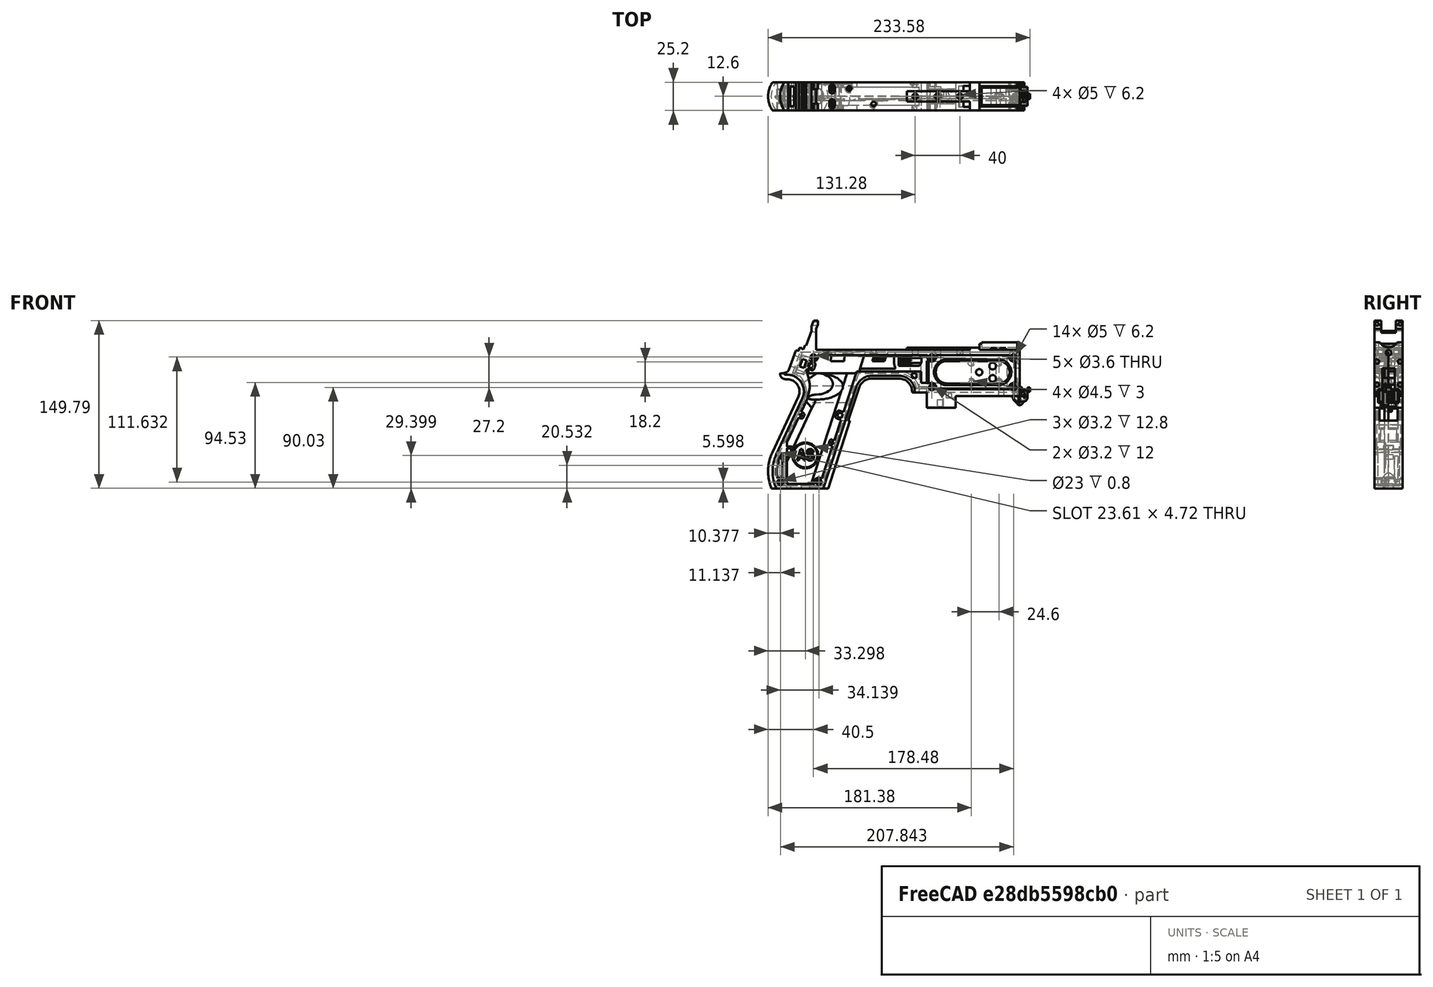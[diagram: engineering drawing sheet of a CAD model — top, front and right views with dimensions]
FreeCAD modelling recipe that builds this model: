
FCSTD DOCUMENT  (FreeCAD 1.0R39319 (Git))
Label: PICON-OF_ver_37
License: All rights reserved
LicenseURL: https://en.wikipedia.org/wiki/All_rights_reserved
objects: Sketcher::SketchObject×107, Part::Extrusion×50, Part::Cut×39, PartDesign::Pad×29, PartDesign::Pocket×18, PartDesign::Chamfer×15, PartDesign::Body×10, PartDesign::Fillet×6, PartDesign::SubtractivePipe×4, Part::Part2DObjectPython×4, PartDesign::SubtractiveLoft×4, PartDesign::Plane×2, PartDesign::SubShapeBinder×2, Part::Sweep×1, PartDesign::ShapeBinder×1, Part::MultiFuse×1, Mesh::Feature×1
note: 552 computed .brp shape members not serialized (recipe doc carries the construction recipe); baked Part::Feature solids carry a one-line shape summary decoded from their .brp

FEATURE [Sketcher::SketchObject] Sketch  label="corpo principale"
  ArcFitTolerance = 1e-06
  AttacherType = Attacher::AttachEngine3D
  AttachmentSupport = -> [XZ_Plane]
  FullyConstrained = true
  MakeInternals = false
  MapMode = 5
  Placement = pos=(0,0,0) rot=(1,0,0;1.5708rad)
  sketch-geometry (65):
    g0: LineSegment StartX=0 StartY=0 StartZ=0 EndX=-57.2 EndY=0 EndZ=0
    g1: LineSegment StartX=-57.2 StartY=0 StartZ=0 EndX=-57.2 EndY=-10.4 EndZ=0
    g2: LineSegment StartX=-57.2 StartY=-10.4 StartZ=0 EndX=-82.8 EndY=-10.4 EndZ=0
    g3: LineSegment StartX=-82.8 StartY=-10.4 StartZ=0 EndX=-82.8 EndY=3.2 EndZ=0
    g4: LineSegment StartX=-82.8 StartY=3.2 StartZ=0 EndX=-93.6 EndY=3.2 EndZ=0
    g5: LineSegment StartX=-93.6 StartY=3.2 StartZ=0 EndX=-93.6 EndY=4 EndZ=0
    g6: LineSegment StartX=-107.6 StartY=18 StartZ=0 EndX=-132.428 EndY=18 EndZ=0
    g7: LineSegment StartX=-145.743 StartY=8.32624 StartZ=0 EndX=-175.232 EndY=-82.4316 EndZ=0
    g8: LineSegment StartX=-175.232 StartY=-82.4316 StartZ=0 EndX=-217.232 EndY=-82.4316 EndZ=0
    g9: LineSegment StartX=-217.232 StartY=-52.1862 StartZ=0 EndX=-193.988 EndY=-2.33927 EndZ=0
    g10: LineSegment StartX=-206.196 StartY=23.0857 StartZ=0 EndX=-199.861 EndY=40.4914 EndZ=0
    g11: LineSegment StartX=-199.861 StartY=40.4914 StartZ=0 EndX=-197.061 EndY=40.4914 EndZ=0
    g12: LineSegment StartX=-197.061 StartY=40.4914 StartZ=0 EndX=-197.061 EndY=42.8914 EndZ=0
    g13: LineSegment StartX=-197.061 StartY=42.8914 StartZ=0 EndX=-194.261 EndY=42.8914 EndZ=0
    g14: LineSegment StartX=-194.261 StartY=42.8914 StartZ=0 EndX=-194.535 EndY=42.1397 EndZ=0
    g15: LineSegment StartX=-194.535 StartY=42.1397 StartZ=0 EndX=-193.031 EndY=41.5924 EndZ=0
    g16: LineSegment StartX=-193.031 StartY=41.5924 StartZ=0 EndX=-191.663 EndY=45.3512 EndZ=0
    g17: LineSegment StartX=-191.663 StartY=45.3512 StartZ=0 EndX=-190.536 EndY=44.9408 EndZ=0
    g18: LineSegment StartX=-190.536 StartY=44.9408 StartZ=0 EndX=-185.747 EndY=58.0965 EndZ=0
    g19: LineSegment StartX=-185.747 StartY=58.0965 StartZ=0 EndX=-185.747 EndY=62.0965 EndZ=0
    g20: LineSegment StartX=-185.747 StartY=62.0965 StartZ=0 EndX=-183.832 EndY=67.3588 EndZ=0
    g21: LineSegment StartX=-183.832 StartY=67.3588 StartZ=0 EndX=-180.232 EndY=67.3588 EndZ=0
    g22: LineSegment StartX=-180.232 StartY=67.3588 StartZ=0 EndX=-180.232 EndY=63.7588 EndZ=0
    g23: LineSegment StartX=-180.232 StartY=63.7588 StartZ=0 EndX=-181.6 EndY=60 EndZ=0
    g24: LineSegment StartX=-181.6 StartY=60 StartZ=0 EndX=-181.6 EndY=41.2 EndZ=0
    g25: LineSegment StartX=-181.6 StartY=41.2 StartZ=0 EndX=-100.8 EndY=41.2 EndZ=0
    g26: LineSegment StartX=-36 StartY=43.2 StartZ=0 EndX=-36 EndY=41.2 EndZ=0
    g27: LineSegment StartX=0 StartY=48 StartZ=0 EndX=0 EndY=0 EndZ=0
    g28: LineSegment StartX=-209.901 StartY=19.85 StartZ=0 EndX=-209.901 EndY=20.1 EndZ=0
    g29: LineSegment StartX=-208.001 StartY=22 StartZ=0 EndX=-207.747 EndY=22 EndZ=0
    g30: LineSegment StartX=-207.583 StartY=19 StartZ=0 EndX=-209.051 EndY=19 EndZ=0
    g31: ArcOfCircle CenterX=-208.001 CenterY=20.1 CenterZ=0 NormalX=0 NormalY=0 NormalZ=1 AngleXU=0 Radius=1.9 StartAngle=1.5708 EndAngle=3.14159
    g32: GeomPoint [constr] X=-209.901 Y=22 Z=0
    g33: ArcOfCircle CenterX=-209.051 CenterY=19.85 CenterZ=0 NormalX=0 NormalY=0 NormalZ=1 AngleXU=0 Radius=0.85 StartAngle=3.14159 EndAngle=4.71239
    g34: GeomPoint [constr] X=-209.901 Y=19 Z=0
    g35: ArcOfCircle CenterX=-207.747 CenterY=23.65 CenterZ=0 NormalX=0 NormalY=0 NormalZ=1 AngleXU=0 Radius=1.65 StartAngle=4.71239 EndAngle=5.93412
    g36: GeomPoint [constr] X=-206.591 Y=22 Z=0
    g37: LineSegment StartX=-4 StartY=6 StartZ=0 EndX=-4 EndY=36.4 EndZ=0
    g38: LineSegment StartX=-4 StartY=36.4 StartZ=0 EndX=-185.2 EndY=36.4 EndZ=0
    g39: LineSegment StartX=-185.2 StartY=36.4 StartZ=0 EndX=-190.441 EndY=22 EndZ=0
    g40: LineSegment StartX=-214.575 StartY=-78.4316 StartZ=0 EndX=-178.142 EndY=-78.4316 EndZ=0
    g41: LineSegment StartX=-178.142 StartY=-78.4316 StartZ=0 EndX=-145.51 EndY=22 EndZ=0
    g42: LineSegment StartX=-145.51 StartY=22 StartZ=0 EndX=-87.91 EndY=22 EndZ=0
    g43: LineSegment StartX=-87.91 StartY=22 StartZ=0 EndX=-87.91 EndY=11.6 EndZ=0
    g44: LineSegment StartX=-87.91 StartY=11.6 StartZ=0 EndX=-80.11 EndY=11.6 EndZ=0
    g45: LineSegment StartX=-80.11 StartY=11.6 StartZ=0 EndX=-80.11 EndY=6 EndZ=0
    g46: LineSegment StartX=-80.11 StartY=6 StartZ=0 EndX=-4 EndY=6 EndZ=0
    g47: LineSegment StartX=-190.363 StartY=-4.02975 StartZ=0 EndX=-213.607 EndY=-53.8767 EndZ=0
    g48: ArcOfCircle CenterX=-132.428 CenterY=4 CenterZ=0 NormalX=0 NormalY=0 NormalZ=1 AngleXU=0 Radius=14 StartAngle=1.5708 EndAngle=2.82743
    g49: GeomPoint [constr] X=-142.6 Y=18 Z=0
    g50: ArcOfCircle CenterX=-107.6 CenterY=4 CenterZ=0 NormalX=0 NormalY=0 NormalZ=1 AngleXU=0 Radius=14 StartAngle=0 EndAngle=1.5708
    g51: GeomPoint [constr] X=-93.6 Y=18 Z=0
    g52: ArcOfCircle CenterX=-184.801 CenterY=-67.3089 CenterZ=0 NormalX=0 NormalY=0 NormalZ=1 AngleXU=0 Radius=35.7833 StartAngle=2.70526 EndAngle=3.57792
    g53: ArcOfCircle CenterX=-207.583 CenterY=4 CenterZ=0 NormalX=0 NormalY=0 NormalZ=1 AngleXU=0 Radius=15 StartAngle=5.84685 EndAngle=7.85398
    g54: LineSegment [constr] StartX=-213.607 StartY=-53.8767 StartZ=0 EndX=-217.232 EndY=-52.1862 EndZ=0
    g55: ArcOfCircle CenterX=-184.801 CenterY=-67.3089 CenterZ=0 NormalX=0 NormalY=0 NormalZ=1 AngleXU=0 Radius=31.7833 StartAngle=2.70526 EndAngle=3.49911
    g56: ArcOfCircle CenterX=-218.095 CenterY=8.90192 CenterZ=0 NormalX=0 NormalY=0 NormalZ=1 AngleXU=0 Radius=30.5989 StartAngle=5.84685 EndAngle=6.72553
    g57: LineSegment StartX=-44.6 StartY=43.2 StartZ=0 EndX=-36 EndY=43.2 EndZ=0
    g58: LineSegment StartX=-100.8 StartY=41.2 StartZ=0 EndX=-44.6 EndY=41.2 EndZ=0
    g59: LineSegment StartX=-44.6 StartY=41.2 StartZ=0 EndX=-44.6 EndY=43.2 EndZ=0
    g60: LineSegment StartX=-2.4 StartY=48 StartZ=0 EndX=0 EndY=48 EndZ=0
    g61: LineSegment StartX=-36 StartY=41.2 StartZ=0 EndX=-2.4 EndY=41.2 EndZ=0
    g62: LineSegment StartX=-2.4 StartY=41.2 StartZ=0 EndX=-2.4 EndY=48 EndZ=0
    g63: LineSegment [constr] StartX=-181.6 StartY=36.4 StartZ=0 EndX=-152.209 EndY=36.4 EndZ=0
    g64: LineSegment [constr] StartX=-181.6 StartY=36.4 StartZ=0 EndX=-130.41 EndY=36.4 EndZ=0
  constraints (183):
    c: Coincident(g-1,g0)
    c: PointOnObject(g0,g-1)
    c: Coincident(g0,g1)
    c: Vertical(g1)
    c: Coincident(g1,g2)
    c: Horizontal(g2)
    c: Coincident(g2,g3)
    c: Vertical(g3)
    c: Coincident(g3,g4)
    c: Coincident(g4,g5)
    c: Vertical(g5)
    c: Horizontal(g6)
    c: Coincident(g7,g8)
    c: Horizontal(g8)
    c: Coincident(g10,g11)
    c: Horizontal(g11)
    c: Coincident(g11,g12)
    c: Vertical(g12)
    c: Coincident(g12,g13)
    c: Horizontal(g13)
    c: Coincident(g13,g14)
    c: Coincident(g14,g15)
    c: Coincident(g15,g16)
    c: Coincident(g16,g17)
    c: Coincident(g17,g18)
    c: Coincident(g18,g19)
    c: Vertical(g19)
    c: Coincident(g19,g20)
    c: Coincident(g20,g21)
    c: Horizontal(g21)
    c: Coincident(g21,g22)
    c: Vertical(g22)
    c: Coincident(g22,g23)
    c: Coincident(g23,g24)
    c: Vertical(g24)
    c: Coincident(g24,g25)
    c: Horizontal(g25)
    c: Coincident(g57,g26)
    c: Vertical(g26)
    c: Coincident(g26,g61)
    c: PointOnObject(g60,g-2)
    c: Coincident(g60,g27)
    c: Coincident(g27,g0)
    c: DistanceY(g27,g27) = 48
    c: DistanceY(g1,g1) = 10.4
    c: DistanceX(g0,g0) = 57.2
    c: DistanceX(g2,g2) = 25.6
    c: Horizontal(g4)
    c: DistanceY(g3,g3) = 13.6
    c: DistanceX(g4,g4) = 10.8
    c: DistanceY(g5,g51) = 14.8
    c: DistanceX(g49,g51) = 49
    c: Distance(g7,g49) = 105.6
    c: DistanceX(g61,g60) = 36
    c: DistanceX(g25,g25) = 80.8
    c: DistanceY(g24,g24) = 18.8
    c: DistanceY(g22,g22) = 3.6
    c: Distance(g23) = 4
    c: Angle(g-1,g23) = 1.22173
    c: DistanceX(g21,g21) = 3.6
    c: Distance(g20) = 5.6
    c: Angle(g-1,g20) = 1.22173
    c: DistanceY(g19,g19) = 4
    c: Distance(g18) = 14
    c: Angle(g-1,g18) = 1.22173
    c: Distance(g17) = 1.2
    c: Distance(g16) = 4
    c: Angle(g16) = 1.22173
    c: Perpendicular(g18,g17)
    c: Distance(g15) = 1.6
    c: Perpendicular(g16,g15)
    c: Distance(g14) = 0.8
    c: DistanceX(g13,g13) = 2.8
    c: Perpendicular(g15,g14)
    c: DistanceY(g12,g12) = 2.4
    c: DistanceX(g11,g11) = 2.8
    c: Distance(g9) = 55
    c: Angle(g9,g-1) = 2.00713
    c: Horizontal(g29)
    c: Vertical(g28)
    c: Horizontal(g30)
    c: PointOnObject(g32,g29)
    c: PointOnObject(g32,g28)
    c: Tangent(g29,g31) = 1.5708
    c: Tangent(g28,g31) = 1.5708
    c: PointOnObject(g34,g28)
    c: PointOnObject(g34,g30)
    c: Tangent(g28,g33) = 1.5708
    c: Tangent(g30,g33) = 1.5708
    c: PointOnObject(g36,g29)
    c: PointOnObject(g36,g10)
    c: Tangent(g29,g35) = -1.5708
    c: Tangent(g10,g35) = -1.5708
    c: Angle(g-1,g10) = 1.22173
    c: Radius(g35) = 1.65
    c: Vertical(g37)
    c: Coincident(g37,g38)
    c: Horizontal(g38)
    c: Coincident(g38,g39)
    c: Horizontal(g40)
    c: Coincident(g40,g41)
    c: Coincident(g41,g42)
    c: Horizontal(g42)
    c: Coincident(g42,g43)
    c: Vertical(g43)
    c: Coincident(g43,g44)
    c: Horizontal(g44)
    c: Coincident(g44,g45)
    c: Vertical(g45)
    c: Coincident(g45,g46)
    c: Coincident(g46,g37)
    c: Horizontal(g46)
    c: DistanceY(g0,g37) = 6
    c: DistanceX(g37,g0) = 4
    c: DistanceY(g37,g25) = 4.8
    c: DistanceX(g38,g38) = 181.2
    c: DistanceX(g42,g42) = 57.6
    c: DistanceY(g49,g41) = 4
    c: DistanceX(g41,g49) = 2.91
    c: DistanceY(g43,g43) = 10.4
    c: DistanceX(g44,g44) = 7.8
    c: DistanceY(g7,g40) = 4
    c: Distance(g47) = 55
    c: Angle(g-1,g39) = 1.22173
    c: PointOnObject(g49,g7)
    c: PointOnObject(g49,g6)
    c: Tangent(g7,g48) = -1.5708
    c: Tangent(g6,g48) = -1.5708
    c: PointOnObject(g51,g5)
    c: PointOnObject(g51,g6)
    c: Tangent(g5,g50) = -1.5708
    c: Tangent(g6,g50) = -1.5708
    c: Radius(g50) = 14
    c: Radius(g48) = 14
    c: DistanceX(g8,g8) = 42
    c: Angle(g7,g-1) = 1.88496
    c: Parallel(g41,g7)
    c: Parallel(g47,g9)
    c: Coincident(g52,g8)
    c: Tangent(g52,g9) = 1.5708
    c: DistanceX(g9,g8) = 0
    c: Tangent(g53,g9) = -1.5708
    c: Tangent(g53,g30) = -1.5708
    c: Diameter(g53) = 30
    c: DistanceY(g53,g0) = -4
    c: Coincident(g54,g47)
    c: Distance(g54) = 4
    c: Coincident(g54,g9)
    c: Coincident(g55,g40)
    c: Tangent(g55,g47) = -1.5708
    c: Coincident(g52,g55)
    c: Coincident(g56,g39)
    c: Tangent(g56,g47) = 1.5708
    c: Horizontal(g57)
    c: DistanceX(g57,g57) = 8.6
    c: Coincident(g58,g25)
    c: Horizontal(g58)
    c: Coincident(g59,g58)
    c: Vertical(g59)
    c: DistanceY(g58,g57) = 2
    c: DistanceX(g58,g58) = 56.2
    c: Coincident(g59,g57)
    c: DistanceY(g41,g36) = 0
    c: DistanceY(g36,g39) = 0
    c: DistanceY(g28,g28) = 0.25
    c: DistanceX(g30,g36) = 2.46
    c: DistanceX(g28,g29) = 1.9
    c: Coincident(g62,g60)
    c: Horizontal(g60)
    c: DistanceX(g62,g27) = 2.4
    c: Coincident(g61,g62)
    c: DistanceY(g26,g26) = 2
    c: Vertical(g62)
    c: DistanceY(g61,g60) = 6.8
    c: Horizontal(g61)
    c: Distance(g63) = 29.391
    c: PointOnObject(g63,g38)
    c: PointOnObject(g63,g38)
    c: Distance(g64) = 51.19
    c: PointOnObject(g64,g38)
    c: PointOnObject(g64,g38)
    c: DistanceX(g24,g63) = 0
    c: DistanceX(g24,g64) = 0
FEATURE [Part::Extrusion] Extrude  label="Extrude corpo principale"
  Base = -> Sketch
  Dir = (0,-1,2e-16)
  DirMode = 2
  FaceMakerClass = Part::FaceMakerBullseye
  FaceMakerMode = 3
  LengthFwd = 25.2
  LengthRev = 12.6
  Solid = true
  Symmetric = true
FEATURE [Sketcher::SketchObject] Sketch002  label="scavo grilletto"
  ArcFitTolerance = 1e-06
  AttachmentSupport = -> [XZ_Plane]
  ExternalGeometry = -> [Sketch]
  FullyConstrained = true
  MakeInternals = false
  MapMode = 5
  Placement = pos=(0,0,0) rot=(1,0,0;1.5708rad)
  sketch-geometry (4):
    g0: LineSegment StartX=-89.51 StartY=22 StartZ=0 EndX=-152.71 EndY=22 EndZ=0
    g1: LineSegment StartX=-152.71 StartY=22 StartZ=0 EndX=-167.006 EndY=-22 EndZ=0
    g2: LineSegment StartX=-167.006 StartY=-22 StartZ=0 EndX=-89.51 EndY=-22 EndZ=0
    g3: LineSegment StartX=-89.51 StartY=-22 StartZ=0 EndX=-89.51 EndY=22 EndZ=0
  constraints (12):
    c: Horizontal(g0)
    c: Coincident(g0,g1)
    c: Coincident(g1,g2)
    c: Horizontal(g2)
    c: Coincident(g2,g3)
    c: Coincident(g3,g0)
    c: Vertical(g3)
    c: Angle(g1,g0) = 1.88496
    c: DistanceY(g3,g3) = 44
    c: DistanceX(g0,g0) = 63.2
    c: DistanceX(g0,g-3) = 1.6
    c: DistanceY(g-3,g0) = 0
FEATURE [Sketcher::SketchObject] Sketch004  label="traiettoria arrotondamento impugnatura anteriore"
  ArcFitTolerance = 1e-06
  AttachmentSupport = -> [XZ_Plane]
  ExternalGeometry = -> [Sketch]
  FullyConstrained = true
  MakeInternals = false
  MapMode = 5
  Placement = pos=(0,0,0) rot=(1,0,0;1.5708rad)
  sketch-geometry (13):
    g0: LineSegment StartX=-175.232 StartY=-82.4316 StartZ=0 EndX=-145.743 EndY=8.32624 EndZ=0
    g1: LineSegment StartX=-93.6 StartY=3.2 StartZ=0 EndX=-93.6 EndY=4 EndZ=0
    g2: LineSegment StartX=-132.428 StartY=18 StartZ=0 EndX=-107.6 EndY=18 EndZ=0
    g3: ArcOfCircle CenterX=-132.428 CenterY=4 CenterZ=0 NormalX=0 NormalY=0 NormalZ=1 AngleXU=0 Radius=14 StartAngle=1.5708 EndAngle=2.82743
    g4: ArcOfCircle CenterX=-107.6 CenterY=4 CenterZ=0 NormalX=0 NormalY=0 NormalZ=1 AngleXU=0 Radius=14 StartAngle=0 EndAngle=1.5708
    g5: LineSegment StartX=-175.232 StartY=-82.4316 StartZ=0 EndX=-217.232 EndY=-82.4316 EndZ=0
    g6: LineSegment StartX=-217.232 StartY=-52.1862 StartZ=0 EndX=-193.988 EndY=-2.33927 EndZ=0
    g7: LineSegment StartX=-209.051 StartY=19 StartZ=0 EndX=-207.583 EndY=19 EndZ=0
    g8: LineSegment StartX=-209.901 StartY=20.1 StartZ=0 EndX=-209.901 EndY=19.85 EndZ=0
    g9: ArcOfCircle CenterX=-184.801 CenterY=-67.3089 CenterZ=0 NormalX=0 NormalY=0 NormalZ=1 AngleXU=0 Radius=35.7833 StartAngle=2.70526 EndAngle=3.57792
    g10: ArcOfCircle CenterX=-207.583 CenterY=4 CenterZ=0 NormalX=0 NormalY=0 NormalZ=1 AngleXU=0 Radius=15 StartAngle=5.84685 EndAngle=7.85398
    g11: ArcOfCircle CenterX=-209.051 CenterY=19.85 CenterZ=0 NormalX=0 NormalY=0 NormalZ=1 AngleXU=0 Radius=0.85 StartAngle=3.14159 EndAngle=4.71239
    g12: ArcOfCircle CenterX=-208.001 CenterY=20.1 CenterZ=0 NormalX=0 NormalY=0 NormalZ=1 AngleXU=0 Radius=1.9 StartAngle=1.5708 EndAngle=3.14159
  constraints (26):
    c: Coincident(g0,g-3)
    c: Coincident(g0,g-6)
    c: Coincident(g1,g-8)
    c: Coincident(g1,g-7)
    c: Coincident(g2,g-5)
    c: Coincident(g2,g-4)
    c: Coincident(g3,g2)
    c: Tangent(g3,g0) = 1.5708
    c: Coincident(g4,g1)
    c: Tangent(g4,g2) = 1.5708
    c: Coincident(g5,g0)
    c: Coincident(g5,g-9)
    c: Coincident(g6,g-12)
    c: Coincident(g6,g-11)
    c: Coincident(g7,g-15)
    c: Coincident(g7,g-14)
    c: Coincident(g8,g-16)
    c: Coincident(g8,g-17)
    c: Tangent(g9,g6) = 1.5708
    c: Coincident(g9,g5)
    c: Coincident(g10,g7)
    c: Tangent(g10,g6) = -1.5708
    c: Tangent(g11,g7) = -1.5708
    c: Coincident(g11,g8)
    c: Tangent(g12,g8) = -1.5708
    c: Coincident(g12,g-17)
FEATURE [PartDesign::Plane] DatumPlane  label="Piano per disegno arrotondamento impugnatura"
  AttachmentSupport = -> [Sketch]
  Length = 68.5841
  MapMode = 7
  Placement = pos=(-145.743,1.8e-15,8.32624) rot=(0.154555,0.154555,0.97582;1.59527rad)
  ResizeMode = 0
  Width = 191.269
FEATURE [Sketcher::SketchObject] Sketch005  label="forma arrotondamento impugnatura anteriore"
  ArcFitTolerance = 1e-06
  AttachmentSupport = -> [DatumPlane]
  FullyConstrained = true
  MakeInternals = false
  MapMode = 5
  Placement = pos=(-145.743,1.8e-15,8.32624) rot=(0.154555,0.154555,0.97582;1.59527rad)
  sketch-geometry (5):
    g0: GeomPoint [constr] X=0 Y=-4 Z=0
    g1: GeomPoint [constr] X=-12.6 Y=7.1e-15 Z=0
    g2: GeomPoint [constr] X=12.6 Y=4.97e-14 Z=0
    g3: LineSegment StartX=-12.6 StartY=7.1e-15 StartZ=0 EndX=12.6 EndY=4.97e-14 EndZ=0
    g4: ArcOfCircle CenterX=-3.88e-14 CenterY=17.845 CenterZ=0 NormalX=0 NormalY=0 NormalZ=1 AngleXU=0 Radius=21.845 StartAngle=4.09759 EndAngle=5.32718
  constraints (11):
    c: DistanceY(g0,g-1) = 4
    c: DistanceX(g-1,g0) = 0
    c: DistanceX(g1,g-1) = 12.6
    c: DistanceX(g-1,g2) = 12.6
    c: DistanceY(g-1,g2) = 0
    c: DistanceY(g-1,g1) = 0
    c: Coincident(g3,g1)
    c: Coincident(g3,g2)
    c: Coincident(g4,g1)
    c: Coincident(g4,g2)
    c: PointOnObject(g0,g4)
FEATURE [Part::Sweep] Sweep  label="Sweep impugnatura"
  Frenet = true
  Sections = -> [Sketch005]
  Solid = true
  Spine = -> Sketch [Edge32,Edge33,Edge34,Edge35,Edge36,Edge37,Edge38,Edge39,Edge40,Edge41,Edge42,Edge43,Edge44]
  Transition = 1
FEATURE [Sketcher::SketchObject] Sketch008  label="buchi e pulizie varie"
  ArcFitTolerance = 1e-06
  AttachmentSupport = -> [XZ_Plane]
  ExternalGeometry = -> [Sketch]
  FullyConstrained = true
  MakeInternals = false
  MapMode = 5
  Placement = pos=(0,0,0) rot=(1,0,0;1.5708rad)
  sketch-geometry (26):
    g0: LineSegment StartX=-96.278 StartY=20.155 StartZ=0 EndX=-92.278 EndY=20.155 EndZ=0
    g1: LineSegment StartX=-92.278 StartY=20.155 StartZ=0 EndX=-92.278 EndY=16.155 EndZ=0
    g2: LineSegment StartX=-92.278 StartY=16.155 StartZ=0 EndX=-96.278 EndY=16.155 EndZ=0
    g3: LineSegment StartX=-96.278 StartY=16.155 StartZ=0 EndX=-96.278 EndY=20.155 EndZ=0
    g4: LineSegment StartX=-222.232 StartY=-82.4316 StartZ=0 EndX=-170.232 EndY=-82.4316 EndZ=0
    g5: LineSegment StartX=-170.232 StartY=-82.4316 StartZ=0 EndX=-170.232 EndY=-86.4316 EndZ=0
    g6: LineSegment StartX=-170.232 StartY=-86.4316 StartZ=0 EndX=-222.232 EndY=-86.4316 EndZ=0
    g7: LineSegment StartX=-222.232 StartY=-86.4316 StartZ=0 EndX=-222.232 EndY=-82.4316 EndZ=0
    g8: LineSegment StartX=-213.901 StartY=20.1 StartZ=0 EndX=-213.901 EndY=26 EndZ=0
    g9: LineSegment StartX=-213.901 StartY=26 StartZ=0 EndX=-206.196 EndY=26 EndZ=0
    g10: LineSegment StartX=-17.4 StartY=42.8 StartZ=0 EndX=-12.4 EndY=42.8 EndZ=0
    g11: LineSegment StartX=-12.4 StartY=42.8 StartZ=0 EndX=-12.4 EndY=41.2 EndZ=0
    g12: LineSegment StartX=-12.4 StartY=41.2 StartZ=0 EndX=-17.4 EndY=41.2 EndZ=0
    g13: LineSegment StartX=-17.4 StartY=41.2 StartZ=0 EndX=-17.4 EndY=42.8 EndZ=0
    g14: LineSegment StartX=-25.9 StartY=42.8 StartZ=0 EndX=-20.9 EndY=42.8 EndZ=0
    g15: LineSegment StartX=-20.9 StartY=42.8 StartZ=0 EndX=-20.9 EndY=41.2 EndZ=0
    g16: LineSegment StartX=-20.9 StartY=41.2 StartZ=0 EndX=-25.9 EndY=41.2 EndZ=0
    g17: LineSegment StartX=-25.9 StartY=41.2 StartZ=0 EndX=-25.9 EndY=42.8 EndZ=0
    g18: GeomPoint [constr] X=-206.196 Y=23.0857 Z=0
    g19: GeomPoint [constr] X=-213.901 Y=20.1 Z=0
    g20: BSplineCurve PolesCount=4 KnotsCount=2 Degree=3 IsPeriodic=0
    g21-g24: Circle [constr] x4 (B-spline internal-alignment scaffolding for g20; pole/knot coordinates omitted)
    g25: LineSegment StartX=-206.196 StartY=26 StartZ=0 EndX=-206.196 EndY=23.0857 EndZ=0
  constraints (73):
    c: Horizontal(g0)
    c: Coincident(g1,g0)
    c: Vertical(g1)
    c: Coincident(g2,g1)
    c: Horizontal(g2)
    c: Coincident(g3,g2)
    c: Coincident(g3,g0)
    c: Vertical(g3)
    c: DistanceX(g0,g-4) = 4.368
    c: DistanceY(g0,g-4) = 1.845
    c: DistanceY(g1,g1) = 4
    c: DistanceX(g2,g2) = 4
    c: Horizontal(g4)
    c: Coincident(g5,g4)
    c: Vertical(g5)
    c: Coincident(g6,g5)
    c: Horizontal(g6)
    c: Coincident(g7,g6)
    c: Coincident(g7,g4)
    c: Vertical(g7)
    c: DistanceY(g7,g7) = 4
    c: DistanceX(g4,g-5) = 5
    c: DistanceX(g-5,g4) = 5
    c: DistanceY(g4,g-5) = 0
    c: Coincident(g9,g8)
    c: Parallel(g9,g-6)
    c: DistanceX(g8,g-8) = 4
    c: Horizontal(g10)
    c: Coincident(g11,g10)
    c: Vertical(g11)
    c: Coincident(g12,g11)
    c: Horizontal(g12)
    c: Coincident(g13,g12)
    c: Coincident(g13,g10)
    c: Vertical(g13)
    c: Horizontal(g14)
    c: Coincident(g15,g14)
    c: Vertical(g15)
    c: Coincident(g16,g15)
    c: Horizontal(g16)
    c: Coincident(g17,g16)
    c: Coincident(g17,g14)
    c: Vertical(g17)
    c: DistanceY(g11,g10) = 1.6
    c: DistanceX(g10,g10) = 5
    c: DistanceY(g15,g14) = 1.6
    c: DistanceX(g14,g14) = 5
    c: DistanceX(g15,g12) = 3.5
    c: DistanceX(g11,g-9) = 10
    c: DistanceY(g-9,g11) = 0
    c: DistanceY(g-9,g15) = 0
    c: Perpendicular(g8,g9)
    c: DistanceY(g-7,g9) = 4
    c: DistanceY(g8,g-8) = 0
    c: InternalAlignment(g18,g20)
    c: InternalAlignment(g19,g20)
    c: InternalAlignment(g21,g20)
    c: Weight(g21) = 1
    c: InternalAlignment(g22,g20)
    c: Equal(g22,g21)
    c: InternalAlignment(g23,g20)
    c: Equal(g23,g21)
    c: InternalAlignment(g24,g20)
    c: Equal(g24,g21)
    c: Coincident(g18,g-12)
    c: Coincident(g19,g8)
    c: Coincident(g25,g9)
    c: Coincident(g25,g20)
    c: Vertical(g25)
    c: DistanceY(g20,g23) = 0
    c: DistanceY(g22,g18) = 2.26
    c: DistanceX(g22,g18) = 0.93
    c: DistanceX(g20,g23) = 2.9
FEATURE [Part::Extrusion] Extrude004  label="Extrude Buchi e pulizie varie"
  Base = -> Sketch008
  Dir = (0,-1,2e-16)
  DirMode = 2
  FaceMakerClass = Part::FaceMakerBullseye
  FaceMakerMode = 3
  LengthFwd = 25.2
  LengthRev = 0
  Solid = true
  Symmetric = true
FEATURE [Sketcher::SketchObject] Sketch009  label="rinforzi"
  ArcFitTolerance = 1e-06
  AttachmentSupport = -> [XZ_Plane]
  ExternalGeometry = -> [Sketch]
  FullyConstrained = true
  MakeInternals = false
  MapMode = 5
  Placement = pos=(0,0,0) rot=(1,0,0;1.5708rad)
  sketch-geometry (9):
    g0: LineSegment StartX=-87.91 StartY=22 StartZ=0 EndX=-87.91 EndY=36.4 EndZ=0
    g1: LineSegment StartX=-87.91 StartY=36.4 StartZ=0 EndX=-97.91 EndY=36.4 EndZ=0
    g2: LineSegment StartX=-97.91 StartY=36.4 StartZ=0 EndX=-97.91 EndY=22 EndZ=0
    g3: LineSegment StartX=-97.91 StartY=22 StartZ=0 EndX=-87.91 EndY=22 EndZ=0
    g4: LineSegment StartX=-149.713 StartY=9.06563 StartZ=0 EndX=-154.586 EndY=-5.93437 EndZ=0
    g5: LineSegment StartX=-154.586 StartY=-5.93437 StartZ=0 EndX=-191.863 EndY=-5.93437 EndZ=0
    g6: LineSegment StartX=-191.863 StartY=-5.93437 StartZ=0 EndX=-191.863 EndY=9.06563 EndZ=0
    g7: LineSegment StartX=-191.863 StartY=9.06563 StartZ=0 EndX=-149.713 EndY=9.06563 EndZ=0
    g8: LineSegment [constr] StartX=-145.51 StartY=22 StartZ=0 EndX=-149.713 EndY=9.06563 EndZ=0
  constraints (25):
    c: Vertical(g0)
    c: Coincident(g1,g0)
    c: Horizontal(g1)
    c: Coincident(g2,g1)
    c: Vertical(g2)
    c: Coincident(g3,g2)
    c: Coincident(g3,g0)
    c: Horizontal(g3)
    c: Coincident(g0,g-4)
    c: DistanceX(g3,g3) = 10
    c: DistanceY(g0,g-3) = 0
    c: Coincident(g5,g4)
    c: Horizontal(g5)
    c: Coincident(g6,g5)
    c: Vertical(g6)
    c: Coincident(g7,g6)
    c: Coincident(g7,g4)
    c: Horizontal(g7)
    c: Distance(g8) = 13.6
    c: Parallel(g-6,g8)
    c: Coincident(g-6,g8)
    c: Parallel(g4,g-6)
    c: DistanceY(g4,g4) = 15
    c: Coincident(g4,g8)
    c: DistanceX(g-5,g5) = -1.5
FEATURE [Part::Extrusion] Extrude001  label="Extrude scavo grilletto"
  Base = -> Sketch002
  Dir = (0,-1,2e-16)
  DirMode = 2
  FaceMakerClass = Part::FaceMakerBullseye
  FaceMakerMode = 3
  LengthFwd = 16
  LengthRev = 0
  Solid = true
  Symmetric = true
FEATURE [Part::Extrusion] Extrude005  label="Extrude Rinforzi"
  Base = -> Sketch009
  Dir = (0,-1,2e-16)
  DirMode = 2
  FaceMakerClass = Part::FaceMakerBullseye
  FaceMakerMode = 3
  LengthFwd = 2
  LengthRev = 0
  Placement = pos=(0,12.6,0) rot=(0,0,1;0rad)
  Solid = true
  Symmetric = false
FEATURE [PartDesign::ShapeBinder] CopyCut
  TraceSupport = false
FEATURE [PartDesign::Plane] DatumPlane001
  AttachmentSupport = -> [CopyCut]
  Length = 60
  MapMode = 5
  Placement = pos=(0,12.6,0) rot=(0,0.707107,0.707107;3.14159rad)
  ResizeMode = 0
  Width = 60
FEATURE [Sketcher::SketchObject] Sketch010  label="buco neopixel"
  ArcFitTolerance = 1e-06
  AttachmentSupport = -> [XZ_Plane]
  ExternalGeometry = -> [Sketch]
  FullyConstrained = true
  MakeInternals = false
  MapMode = 5
  Placement = pos=(0,0,0) rot=(1,0,0;1.5708rad)
  sketch-geometry (5):
    g0: LineSegment [constr] StartX=-199.861 StartY=40.4914 StartZ=0 EndX=-201.368 EndY=36.3521 EndZ=0
    g1: LineSegment StartX=-201.368 StartY=36.3521 StartZ=0 EndX=-204.932 EndY=26.5605 EndZ=0
    g2: LineSegment StartX=-201.368 StartY=36.3521 StartZ=0 EndX=-180.2 EndY=28.6477 EndZ=0
    g3: LineSegment StartX=-180.2 StartY=28.6477 StartZ=0 EndX=-183.764 EndY=18.8561 EndZ=0
    g4: LineSegment StartX=-183.764 StartY=18.8561 StartZ=0 EndX=-204.932 EndY=26.5605 EndZ=0
  constraints (14):
    c: Parallel(g0,g-3)
    c: Distance(g0) = 4.405
    c: Coincident(g0,g-3)
    c: Coincident(g2,g1)
    c: Coincident(g3,g2)
    c: Coincident(g4,g3)
    c: Coincident(g4,g1)
    c: Parallel(g1,g-3)
    c: Distance(g1) = 10.42
    c: Coincident(g1,g0)
    c: Parallel(g2,g4)
    c: Perpendicular(g1,g2)
    c: DistanceX(g-4,g2) = 5
    c: Parallel(g3,g1)
FEATURE [Part::Extrusion] Extrude006  label="Extrude buco neopixel"
  Base = -> Sketch010
  Dir = (0,-1,2e-16)
  DirMode = 2
  FaceMakerClass = Part::FaceMakerBullseye
  FaceMakerMode = 3
  LengthFwd = 17.2
  LengthRev = 0
  Solid = true
  Symmetric = true
FEATURE [Sketcher::SketchObject] Sketch011  label="fermo grilletto"
  ArcFitTolerance = 1e-06
  AttachmentSupport = -> [XZ_Plane]
  ExternalGeometry = -> [Sketch]
  FullyConstrained = true
  MakeInternals = false
  MapMode = 5
  Placement = pos=(0,0,0) rot=(1,0,0;1.5708rad)
  sketch-geometry (18):
    g0: LineSegment [constr] StartX=-145.51 StartY=22 StartZ=0 EndX=-157.347 EndY=-14.4293 EndZ=0
    g1: LineSegment [constr] StartX=-157.347 StartY=-14.4293 StartZ=0 EndX=-157.841 EndY=-15.951 EndZ=0
    g2: LineSegment StartX=-161.151 StartY=-13.1932 StartZ=0 EndX=-155.825 EndY=-14.9237 EndZ=0
    g3: LineSegment StartX=-163.167 StartY=-14.2205 StartZ=0 EndX=-164.403 EndY=-18.0247 EndZ=0
    g4: LineSegment StartX=-163.376 StartY=-20.0408 StartZ=0 EndX=-158.05 EndY=-21.7713 EndZ=0
    g5: LineSegment StartX=-158.05 StartY=-21.7713 StartZ=0 EndX=-155.825 EndY=-14.9237 EndZ=0
    g6: LineSegment StartX=-161.645 StartY=-14.7149 StartZ=0 EndX=-157.841 EndY=-15.951 EndZ=0
    g7: LineSegment StartX=-157.841 StartY=-15.951 StartZ=0 EndX=-159.077 EndY=-19.7552 EndZ=0
    g8: LineSegment StartX=-159.077 StartY=-19.7552 StartZ=0 EndX=-162.881 EndY=-18.5191 EndZ=0
    g9: LineSegment StartX=-162.881 StartY=-18.5191 StartZ=0 EndX=-161.645 EndY=-14.7149 EndZ=0
    g10: LineSegment [constr] StartX=-161.645 StartY=-14.7149 StartZ=0 EndX=-161.151 EndY=-13.1932 EndZ=0
    g11: LineSegment [constr] StartX=-159.077 StartY=-19.7552 StartZ=0 EndX=-157.555 EndY=-20.2496 EndZ=0
    g12: LineSegment [constr] StartX=-159.077 StartY=-19.7552 StartZ=0 EndX=-159.572 EndY=-21.2769 EndZ=0
    g13: LineSegment [constr] StartX=-161.645 StartY=-14.7149 StartZ=0 EndX=-163.167 EndY=-14.2205 EndZ=0
    g14: ArcOfCircle CenterX=-161.645 CenterY=-14.7149 CenterZ=0 NormalX=0 NormalY=0 NormalZ=1 AngleXU=0 Radius=1.6 StartAngle=1.25664 EndAngle=2.82743
    g15: GeomPoint [constr] X=-162.673 Y=-12.6988 Z=0
    g16: ArcOfCircle CenterX=-162.881 CenterY=-18.5191 CenterZ=0 NormalX=0 NormalY=0 NormalZ=1 AngleXU=0 Radius=1.6 StartAngle=2.82743 EndAngle=4.39823
    g17: GeomPoint [constr] X=-164.897 Y=-19.5464 Z=0
  constraints (48):
    c: Parallel(g0,g-3)
    c: Distance(g0) = 38.304
    c: Coincident(g0,g-3)
    c: Parallel(g1,g-3)
    c: Distance(g1) = 1.6
    c: Coincident(g1,g0)
    c: Coincident(g5,g4)
    c: Coincident(g5,g2)
    c: Coincident(g7,g6)
    c: Coincident(g8,g7)
    c: Coincident(g9,g8)
    c: Coincident(g9,g6)
    c: Parallel(g7,g-3)
    c: Parallel(g9,g7)
    c: Perpendicular(g6,g7)
    c: Parallel(g6,g8)
    c: Distance(g6) = 4
    c: Distance(g9) = 4
    c: Parallel(g5,g7)
    c: Parallel(g9,g3)
    c: Parallel(g2,g6)
    c: Parallel(g4,g8)
    c: Parallel(g13,g6)
    c: Parallel(g10,g9)
    c: Parallel(g11,g8)
    c: Parallel(g12,g7)
    c: Distance(g10) = 1.6
    c: Distance(g13) = 1.6
    c: Distance(g12) = 1.6
    c: Distance(g11) = 1.6
    c: Coincident(g10,g6)
    c: Coincident(g13,g6)
    c: Coincident(g12,g7)
    c: Coincident(g11,g7)
    c: Distance(g10,g15) = 1.6
    c: Distance(g15,g13) = 1.6
    c: Distance(g4,g12) = 1.6
    c: Distance(g4,g11) = 1.6
    c: PointOnObject(g15,g2)
    c: Tangent(g3,g14) = -1.5708
    c: Tangent(g2,g14) = 1.5708
    c: PointOnObject(g17,g4)
    c: PointOnObject(g17,g3)
    c: Tangent(g4,g16) = -1.5708
    c: Tangent(g3,g16) = -1.5708
    c: Equal(g16,g14)
    c: Coincident(g16,g8)
    c: Coincident(g6,g1)
FEATURE [Part::Extrusion] Extrude007  label="Extrude fermo grilletto"
  Base = -> Sketch011
  Dir = (0,-1,2e-16)
  DirMode = 2
  FaceMakerClass = Part::FaceMakerBullseye
  FaceMakerMode = 3
  LengthFwd = 25.2
  LengthRev = 0
  Solid = true
  Symmetric = true
FEATURE [Sketcher::SketchObject] Sketch012  label="buco oled"
  ArcFitTolerance = 1e-06
  AttachmentSupport = -> [XZ_Plane]
  ExternalGeometry = -> [Sketch]
  FullyConstrained = true
  MakeInternals = false
  MapMode = 5
  Placement = pos=(0,0,0) rot=(1,0,0;1.5708rad)
  sketch-geometry (4):
    g0: LineSegment StartX=-185.747 StartY=58.0965 StartZ=0 EndX=-180.232 EndY=56.0891 EndZ=0
    g1: LineSegment StartX=-185.747 StartY=58.0965 StartZ=0 EndX=-185.747 EndY=67.3588 EndZ=0
    g2: LineSegment StartX=-185.747 StartY=67.3588 StartZ=0 EndX=-180.232 EndY=67.3588 EndZ=0
    g3: LineSegment StartX=-180.232 StartY=67.3588 StartZ=0 EndX=-180.232 EndY=56.0891 EndZ=0
  constraints (10):
    c: Coincident(g1,g0)
    c: Coincident(g2,g1)
    c: Coincident(g3,g2)
    c: Coincident(g3,g0)
    c: Parallel(g1,g-5)
    c: Perpendicular(g-3,g0)
    c: Parallel(g2,g-6)
    c: Parallel(g3,g-4)
    c: Coincident(g0,g-5)
    c: Coincident(g2,g-6)
FEATURE [Part::Extrusion] Extrude008  label="Extrude buco oled"
  Base = -> Sketch012
  Dir = (0,-1,2e-16)
  DirMode = 2
  FaceMakerClass = Part::FaceMakerBullseye
  FaceMakerMode = 3
  LengthFwd = 12.8
  LengthRev = 0
  Solid = true
  Symmetric = true
FEATURE [Sketcher::SketchObject] Sketch013  label="buco pompa"
  ArcFitTolerance = 1e-06
  AttachmentSupport = -> [XZ_Plane]
  ExternalGeometry = -> [Sketch]
  FullyConstrained = true
  MakeInternals = false
  MapMode = 5
  Placement = pos=(0,0,0) rot=(1,0,0;1.5708rad)
  sketch-geometry (8):
    g0: LineSegment StartX=-82.8 StartY=-10.4 StartZ=0 EndX=-82.8 EndY=-9.6 EndZ=0
    g1: LineSegment StartX=-82.8 StartY=-9.6 StartZ=0 EndX=-67.9 EndY=-9.6 EndZ=0
    g2: LineSegment StartX=-67.9 StartY=-9.6 StartZ=0 EndX=-67.9 EndY=6 EndZ=0
    g3: LineSegment StartX=-67.9 StartY=6 StartZ=0 EndX=-65.9 EndY=6 EndZ=0
    g4: LineSegment StartX=-65.9 StartY=6 StartZ=0 EndX=-65.9 EndY=-1.7 EndZ=0
    g5: LineSegment StartX=-65.9 StartY=-1.7 StartZ=0 EndX=-57.2 EndY=-1.7 EndZ=0
    g6: LineSegment StartX=-57.2 StartY=-1.7 StartZ=0 EndX=-57.2 EndY=-10.4 EndZ=0
    g7: LineSegment StartX=-57.2 StartY=-10.4 StartZ=0 EndX=-82.8 EndY=-10.4 EndZ=0
  constraints (22):
    c: Vertical(g0)
    c: Coincident(g1,g0)
    c: Horizontal(g1)
    c: Coincident(g2,g1)
    c: Vertical(g2)
    c: Coincident(g3,g2)
    c: Horizontal(g3)
    c: Coincident(g4,g3)
    c: Vertical(g4)
    c: Coincident(g5,g4)
    c: Horizontal(g5)
    c: Coincident(g6,g5)
    c: Vertical(g6)
    c: Coincident(g7,g6)
    c: Coincident(g7,g0)
    c: DistanceY(g0,g0) = 0.8
    c: DistanceY(g6,g6) = 8.7
    c: DistanceX(g1,g1) = 14.9
    c: DistanceX(g3,g3) = 2
    c: Coincident(g0,g-4)
    c: DistanceY(g2,g-6) = 0
    c: Coincident(g6,g-5)
FEATURE [Part::Extrusion] Extrude009  label="Extrude buco pompa"
  Base = -> Sketch013
  Dir = (0,-1,2e-16)
  DirMode = 2
  FaceMakerClass = Part::FaceMakerBullseye
  FaceMakerMode = 3
  LengthFwd = 13.2
  LengthRev = 0
  Solid = true
  Symmetric = true
FEATURE [Sketcher::SketchObject] Sketch014  label="buco frontale"
  ArcFitTolerance = 1e-06
  AttachmentSupport = -> [XZ_Plane]
  ExternalGeometry = -> [Sketch]
  FullyConstrained = true
  MakeInternals = false
  MapMode = 5
  Placement = pos=(0,0,0) rot=(1,0,0;1.5708rad)
  sketch-geometry (10):
    g0: LineSegment StartX=0 StartY=0 StartZ=0 EndX=0 EndY=24.671 EndZ=0
    g1: LineSegment StartX=0 StartY=24.671 StartZ=0 EndX=-4 EndY=24.671 EndZ=0
    g2: LineSegment StartX=-4 StartY=24.671 StartZ=0 EndX=-4 EndY=16 EndZ=0
    g3: LineSegment StartX=-4 StartY=16 StartZ=0 EndX=-2.4 EndY=16 EndZ=0
    g4: LineSegment StartX=-2.4 StartY=16 StartZ=0 EndX=-2.4 EndY=10 EndZ=0
    g5: LineSegment StartX=-2.4 StartY=10 StartZ=0 EndX=-12 EndY=10 EndZ=0
    g6: LineSegment StartX=-12 StartY=10 StartZ=0 EndX=-12 EndY=6 EndZ=0
    g7: LineSegment StartX=-12 StartY=6 StartZ=0 EndX=-2.4 EndY=6 EndZ=0
    g8: LineSegment StartX=-2.4 StartY=6 StartZ=0 EndX=-2.4 EndY=0 EndZ=0
    g9: LineSegment StartX=-2.4 StartY=0 StartZ=0 EndX=0 EndY=0 EndZ=0
  constraints (29):
    c: Vertical(g0)
    c: Coincident(g1,g0)
    c: Horizontal(g1)
    c: Coincident(g2,g1)
    c: Vertical(g2)
    c: Coincident(g3,g2)
    c: Horizontal(g3)
    c: Coincident(g4,g3)
    c: Vertical(g4)
    c: Coincident(g5,g4)
    c: Horizontal(g5)
    c: Coincident(g6,g5)
    c: Vertical(g6)
    c: Coincident(g7,g6)
    c: Coincident(g8,g7)
    c: Vertical(g8)
    c: Coincident(g9,g8)
    c: Coincident(g9,g0)
    c: Horizontal(g9)
    c: DistanceY(g0,g0) = 24.671
    c: Horizontal(g7)
    c: DistanceY(g6,g6) = 4
    c: DistanceY(g4,g4) = 6
    c: DistanceX(g9,g9) = 2.4
    c: Coincident(g0,g-1)
    c: DistanceY(g-3,g7) = 0
    c: DistanceX(g8,g4) = 0
    c: DistanceX(g-3,g1) = 0
    c: DistanceX(g6,g-3) = 8
FEATURE [Part::Extrusion] Extrude010  label="Extrude buco frontale"
  Base = -> Sketch014
  Dir = (0,-1,2e-16)
  DirMode = 2
  FaceMakerClass = Part::FaceMakerBullseye
  FaceMakerMode = 3
  LengthFwd = 11.2
  LengthRev = 0
  Solid = true
  Symmetric = true
FEATURE [Sketcher::SketchObject] Sketch015  label="guida rail"
  ArcFitTolerance = 1e-06
  AttachmentSupport = -> [XZ_Plane]
  ExternalGeometry = -> [Sketch]
  FullyConstrained = true
  MakeInternals = false
  MapMode = 5
  Placement = pos=(0,0,0) rot=(1,0,0;1.5708rad)
  sketch-geometry (4):
    g0: LineSegment StartX=-100.8 StartY=43.2 StartZ=0 EndX=-44.6 EndY=43.2 EndZ=0
    g1: LineSegment StartX=-44.6 StartY=43.2 StartZ=0 EndX=-44.6 EndY=41.2 EndZ=0
    g2: LineSegment StartX=-44.6 StartY=41.2 StartZ=0 EndX=-100.8 EndY=41.2 EndZ=0
    g3: LineSegment StartX=-100.8 StartY=41.2 StartZ=0 EndX=-100.8 EndY=43.2 EndZ=0
  constraints (9):
    c: Horizontal(g0)
    c: Coincident(g1,g0)
    c: Coincident(g2,g1)
    c: Coincident(g3,g2)
    c: Coincident(g3,g0)
    c: Vertical(g3)
    c: Coincident(g2,g-3)
    c: Coincident(g1,g-3)
    c: Coincident(g0,g-4)
FEATURE [Part::Extrusion] Extrude011  label="Extrude guida rail"
  Base = -> Sketch015
  Dir = (0,-1,2e-16)
  DirMode = 2
  FaceMakerClass = Part::FaceMakerBullseye
  FaceMakerMode = 3
  LengthFwd = 9
  LengthRev = 0
  Solid = true
  Symmetric = true
FEATURE [Sketcher::SketchObject] Sketch016  label="guide per coperture laterali"
  ArcFitTolerance = 1e-06
  AttachmentSupport = -> [XZ_Plane]
  ExternalGeometry = -> [Sketch]
  FullyConstrained = true
  MakeInternals = false
  MapMode = 5
  Placement = pos=(0,0,0) rot=(1,0,0;1.5708rad)
  sketch-geometry (14):
    g0: Circle CenterX=-5.6 CenterY=7.6 CenterZ=0 NormalX=0 NormalY=0 NormalZ=1 AngleXU=0 Radius=1.6
    g1: Circle CenterX=-5.6 CenterY=7.6 CenterZ=0 NormalX=0 NormalY=0 NormalZ=1 AngleXU=0 Radius=4
    g2: Circle CenterX=-5.6 CenterY=34.8 CenterZ=0 NormalX=0 NormalY=0 NormalZ=1 AngleXU=0 Radius=1.6
    g3: Circle CenterX=-5.6 CenterY=34.8 CenterZ=0 NormalX=0 NormalY=0 NormalZ=1 AngleXU=0 Radius=4
    g4: Circle CenterX=-184.08 CenterY=34.8 CenterZ=0 NormalX=0 NormalY=0 NormalZ=1 AngleXU=0 Radius=1.6
    g5: Circle CenterX=-184.08 CenterY=34.8 CenterZ=0 NormalX=0 NormalY=0 NormalZ=1 AngleXU=0 Radius=4
    g6: Circle CenterX=-179.305 CenterY=-76.8316 CenterZ=0 NormalX=0 NormalY=0 NormalZ=1 AngleXU=0 Radius=1.6
    g7: Circle CenterX=-179.305 CenterY=-76.8316 CenterZ=0 NormalX=0 NormalY=0 NormalZ=1 AngleXU=0 Radius=4
    g8: Circle CenterX=-213.443 CenterY=-76.8316 CenterZ=0 NormalX=0 NormalY=0 NormalZ=1 AngleXU=0 Radius=1.6
    g9: Circle CenterX=-213.443 CenterY=-76.8316 CenterZ=0 NormalX=0 NormalY=0 NormalZ=1 AngleXU=0 Radius=4
    g10: Circle CenterX=-78.51 CenterY=7.6 CenterZ=0 NormalX=0 NormalY=0 NormalZ=1 AngleXU=0 Radius=1.6
    g11: Circle CenterX=-78.51 CenterY=7.6 CenterZ=0 NormalX=0 NormalY=0 NormalZ=1 AngleXU=0 Radius=4
    g12: Circle CenterX=-78.51 CenterY=34.8 CenterZ=0 NormalX=0 NormalY=0 NormalZ=1 AngleXU=0 Radius=1.6
    g13: Circle CenterX=-78.51 CenterY=34.8 CenterZ=0 NormalX=0 NormalY=0 NormalZ=1 AngleXU=0 Radius=4
  constraints (35):
    c: Diameter(g0) = 3.2
    c: Diameter(g1) = 8
    c: Coincident(g0,g1)
    c: Diameter(g2) = 3.2
    c: Diameter(g3) = 8
    c: Coincident(g3,g2)
    c: Tangent(g2,g-7)
    c: Diameter(g4) = 3.2
    c: Diameter(g5) = 8
    c: Coincident(g5,g4)
    c: Tangent(g4,g-7)
    c: Tangent(g4,g-8)
    c: Diameter(g6) = 3.2
    c: Diameter(g7) = 8
    c: Coincident(g7,g6)
    c: Tangent(g6,g-9)
    c: Tangent(g6,g-10)
    c: Diameter(g8) = 3.2
    c: Diameter(g9) = 8
    c: Coincident(g9,g8)
    c: Tangent(g8,g-10)
    c: Tangent(g8,g-11)
    c: Diameter(g10) = 3.2
    c: Diameter(g11) = 8
    c: Diameter(g12) = 3.2
    c: Diameter(g13) = 8
    c: Coincident(g12,g13)
    c: Coincident(g10,g11)
    c: Tangent(g12,g-7)
    c: DistanceX(g12,g10) = 0
    c: Tangent(g2,g-6)
    c: Tangent(g0,g-6)
    c: Tangent(g0,g-3)
    c: Tangent(g10,g-3)
    c: Tangent(g10,g-4)
FEATURE [Part::Extrusion] Extrude012  label="extrude guide per coperture laterali"
  Base = -> Sketch016
  Dir = (0,-1,2e-16)
  DirMode = 2
  FaceMakerClass = Part::FaceMakerBullseye
  FaceMakerMode = 3
  LengthFwd = 25.2
  LengthRev = 0
  Solid = true
  Symmetric = true
FEATURE [Sketcher::SketchObject] Sketch017  label="supporto CAM"
  ArcFitTolerance = 1e-06
  AttachmentSupport = -> [XZ_Plane]
  ExternalGeometry = -> [Sketch]
  FullyConstrained = true
  MakeInternals = false
  MapMode = 5
  Placement = pos=(0,0,0) rot=(1,0,0;1.5708rad)
  sketch-geometry (6):
    g0: LineSegment StartX=-2.4 StartY=48 StartZ=0 EndX=-2.4 EndY=41.2 EndZ=0
    g1: LineSegment StartX=-2.4 StartY=48 StartZ=0 EndX=-34 EndY=48 EndZ=0
    g2: LineSegment StartX=-34 StartY=48 StartZ=0 EndX=-34 EndY=46.72 EndZ=0
    g3: LineSegment StartX=-34 StartY=46.72 StartZ=0 EndX=-36 EndY=46.72 EndZ=0
    g4: LineSegment StartX=-36 StartY=46.72 StartZ=0 EndX=-36 EndY=41.2 EndZ=0
    g5: LineSegment StartX=-36 StartY=41.2 StartZ=0 EndX=-2.4 EndY=41.2 EndZ=0
  constraints (15):
    c: Coincident(g1,g0)
    c: Horizontal(g1)
    c: Coincident(g2,g1)
    c: Vertical(g2)
    c: Coincident(g3,g2)
    c: Horizontal(g3)
    c: Coincident(g4,g3)
    c: Coincident(g5,g4)
    c: DistanceX(g1,g0) = 31.6
    c: Coincident(g5,g0)
    c: Vertical(g4)
    c: DistanceY(g2,g1) = 1.28
    c: Coincident(g0,g-3)
    c: Coincident(g0,g-3)
    c: Coincident(g4,g-4)
FEATURE [Part::Extrusion] Extrude013  label="Extrude supporto CAM"
  Base = -> Sketch017
  Dir = (0,-1,2e-16)
  DirMode = 2
  FaceMakerClass = Part::FaceMakerBullseye
  FaceMakerMode = 3
  LengthFwd = 17.8
  LengthRev = 0
  Solid = true
  Symmetric = true
FEATURE [Sketcher::SketchObject] Sketch018  label="Scavo CAM"
  ArcFitTolerance = 1e-06
  AttachmentSupport = -> [YZ_Plane]
  ExternalGeometry = -> [Sketch]
  FullyConstrained = true
  MakeInternals = false
  MapMode = 5
  Placement = pos=(0,0,0) rot=(0.57735,0.57735,0.57735;2.0944rad)
  sketch-geometry (4):
    g0: LineSegment StartX=-7.73 StartY=48 StartZ=0 EndX=7.73 EndY=48 EndZ=0
    g1: LineSegment [constr] StartX=1.07e-14 StartY=48 StartZ=0 EndX=0 EndY=43.5155 EndZ=0
    g2: ArcOfCircle CenterX=9e-15 CenterY=52.42 CenterZ=0 NormalX=0 NormalY=0 NormalZ=1 AngleXU=0 Radius=8.90445 StartAngle=3.66102 EndAngle=5.76376
    g3: Circle [constr] CenterX=9e-15 CenterY=52.42 CenterZ=0 NormalX=0 NormalY=0 NormalZ=1 AngleXU=0 Radius=8.9
  constraints (13):
    c: Horizontal(g0)
    c: DistanceY(g-3,g0) = 0
    c: DistanceX(g0,g0) = 15.46
    c: DistanceX(g0,g-3) = 7.73
    c: DistanceX(g-3) = 0
    c: Coincident(g1,g-3)
    c: PointOnObject(g1,g-2)
    c: Coincident(g2,g0)
    c: Coincident(g2,g0)
    c: PointOnObject(g1,g2)
    c: Diameter(g3) = 17.8
    c: DistanceY(g1,g3) = 4.42
    c: Coincident(g2,g3)
FEATURE [Part::Extrusion] Extrude014  label="Extrude Scavo CAM"
  Base = -> Sketch018
  Dir = (1,0,0)
  DirMode = 2
  FaceMakerClass = Part::FaceMakerBullseye
  FaceMakerMode = 3
  LengthFwd = -34
  LengthRev = 0
  Solid = true
  Symmetric = false
FEATURE [Sketcher::SketchObject] Sketch019  label="scavo rumble"
  ArcFitTolerance = 1e-06
  AttachmentSupport = -> [XZ_Plane]
  ExternalGeometry = -> [Sketch]
  FullyConstrained = true
  MakeInternals = false
  MapMode = 5
  Placement = pos=(0,0,0) rot=(1,0,0;1.5708rad)
  sketch-geometry (6):
    g0: LineSegment StartX=-164.575 StartY=-24.3786 StartZ=0 EndX=-159.439 EndY=-26.0473 EndZ=0
    g1: LineSegment StartX=-159.439 StartY=-26.0473 StartZ=0 EndX=-166.547 EndY=-47.9216 EndZ=0
    g2: LineSegment StartX=-166.547 StartY=-47.9216 StartZ=0 EndX=-171.682 EndY=-46.2529 EndZ=0
    g3: LineSegment StartX=-171.682 StartY=-46.2529 StartZ=0 EndX=-164.575 EndY=-24.3786 EndZ=0
    g4: LineSegment [constr] StartX=-145.51 StartY=22 StartZ=0 EndX=-160.961 EndY=-25.5528 EndZ=0
    g5: LineSegment [constr] StartX=-159.439 StartY=-26.0473 StartZ=0 EndX=-160.961 EndY=-25.5528 EndZ=0
  constraints (17):
    c: Coincident(g1,g0)
    c: Coincident(g2,g1)
    c: Coincident(g3,g2)
    c: Coincident(g3,g0)
    c: Parallel(g3,g-3)
    c: Parallel(g3,g1)
    c: Perpendicular(g3,g0)
    c: Perpendicular(g2,g3)
    c: Distance(g2,g0) = 23
    c: Parallel(g4,g-3)
    c: Distance(g4) = 50
    c: Coincident(g4,g-3)
    c: Parallel(g5,g0)
    c: Distance(g5) = 1.6
    c: Coincident(g5,g0)
    c: Distance(g5,g0) = 3.8
    c: Coincident(g5,g4)
FEATURE [Part::Extrusion] Extrude015  label="scavo rumble001"
  Base = -> Sketch019
  Dir = (0,-1,2e-16)
  DirMode = 2
  FaceMakerClass = Part::FaceMakerBullseye
  FaceMakerMode = 3
  LengthFwd = 21
  LengthRev = 0
  Solid = true
  Symmetric = true
FEATURE [Sketcher::SketchObject] Sketch020  label="fermo rumble"
  ArcFitTolerance = 1e-06
  AttachmentSupport = -> [XZ_Plane]
  ExternalGeometry = -> [Sketch019,Sketch]
  FullyConstrained = true
  MakeInternals = false
  MapMode = 5
  Placement = pos=(0,0,0) rot=(1,0,0;1.5708rad)
  sketch-geometry (16):
    g0: LineSegment [constr] StartX=-166.709 StartY=-43.2425 StartZ=0 EndX=-168.068 EndY=-47.4271 EndZ=0
    g1: LineSegment [constr] StartX=-168.068 StartY=-47.4271 StartZ=0 EndX=-166.547 EndY=-47.9216 EndZ=0
    g2: LineSegment StartX=-168.121 StartY=-40.4703 StartZ=0 EndX=-166.029 EndY=-41.1502 EndZ=0
    g3: LineSegment StartX=-166.029 StartY=-41.1502 StartZ=0 EndX=-166.709 EndY=-43.2425 EndZ=0
    g4: LineSegment StartX=-166.709 StartY=-43.2425 StartZ=0 EndX=-168.801 EndY=-42.5626 EndZ=0
    g5: LineSegment StartX=-168.801 StartY=-42.5626 StartZ=0 EndX=-168.121 EndY=-40.4703 EndZ=0
    g6: LineSegment StartX=-167.627 StartY=-38.9486 StartZ=0 EndX=-164.203 EndY=-40.0611 EndZ=0
    g7: LineSegment StartX=-164.203 StartY=-40.0611 StartZ=0 EndX=-165.81 EndY=-45.0066 EndZ=0
    g8: LineSegment StartX=-165.81 StartY=-45.0066 StartZ=0 EndX=-169.234 EndY=-43.8941 EndZ=0
    g9: LineSegment StartX=-170.261 StartY=-41.878 StartZ=0 EndX=-169.643 EndY=-39.9759 EndZ=0
    g10: LineSegment [constr] StartX=-169.643 StartY=-39.9759 StartZ=0 EndX=-169.148 EndY=-38.4542 EndZ=0
    g11: LineSegment [constr] StartX=-169.148 StartY=-38.4542 StartZ=0 EndX=-167.627 EndY=-38.9486 EndZ=0
    g12: ArcOfCircle CenterX=-168.739 CenterY=-42.3724 CenterZ=0 NormalX=0 NormalY=0 NormalZ=1 AngleXU=0 Radius=1.6 StartAngle=2.82743 EndAngle=4.39823
    g13: GeomPoint [constr] X=-170.755 Y=-43.3997 Z=0
    g14: ArcOfCircle CenterX=-168.121 CenterY=-40.4703 CenterZ=0 NormalX=0 NormalY=0 NormalZ=1 AngleXU=0 Radius=1.6 StartAngle=1.25664 EndAngle=2.82743
    g15: GeomPoint [constr] X=-169.148 Y=-38.4542 Z=0
  constraints (42):
    c: Parallel(g0,g-4)
    c: Distance(g0) = 4.4
    c: Coincident(g1,g0)
    c: Perpendicular(g0,g1)
    c: Distance(g1) = 1.6
    c: Coincident(g1,g-5)
    c: Coincident(g3,g2)
    c: Coincident(g4,g3)
    c: Coincident(g5,g4)
    c: Coincident(g5,g2)
    c: Parallel(g3,g-4)
    c: Parallel(g3,g5)
    c: Perpendicular(g2,g3)
    c: Parallel(g4,g2)
    c: Distance(g2) = 2.2
    c: Distance(g3) = 2.2
    c: Coincident(g7,g6)
    c: Coincident(g8,g7)
    c: Parallel(g7,g-4)
    c: Parallel(g7,g9)
    c: Perpendicular(g6,g7)
    c: Parallel(g6,g8)
    c: Distance(g6,g15) = 5.2
    c: Distance(g7) = 5.2
    c: Coincident(g11,g10)
    c: Parallel(g10,g9)
    c: Parallel(g11,g6)
    c: Distance(g10) = 1.6
    c: Distance(g11) = 1.6
    c: Coincident(g10,g15)
    c: Distance(g11,g2) = 1.6
    c: Distance(g2,g10) = 1.6
    c: PointOnObject(g13,g8)
    c: PointOnObject(g13,g9)
    c: Tangent(g8,g12) = 1.5708
    c: Tangent(g9,g12) = 1.5708
    c: PointOnObject(g15,g9)
    c: Tangent(g6,g14) = 1.5708
    c: Tangent(g9,g14) = 1.5708
    c: Equal(g12,g14)
    c: Coincident(g6,g11)
    c: Coincident(g3,g0)
FEATURE [Part::Extrusion] Extrude016  label="Extrude fermo rumble"
  Base = -> Sketch020
  Dir = (0,-1,2e-16)
  DirMode = 2
  FaceMakerClass = Part::FaceMakerBullseye
  FaceMakerMode = 3
  LengthFwd = 25.2
  LengthRev = 0
  Solid = true
  Symmetric = true
FEATURE [Sketcher::SketchObject] Sketch021  label="perno fermo rumble001"
  ArcFitTolerance = 1e-06
  AttachmentSupport = -> [XZ_Plane001]
  FullyConstrained = true
  MakeInternals = false
  MapMode = 5
  Placement = pos=(0,0,0) rot=(1,0,0;1.5708rad)
  sketch-geometry (16):
    g0: LineSegment StartX=0 StartY=0.45 StartZ=0 EndX=0 EndY=1.55 EndZ=0
    g1: LineSegment StartX=0.45 StartY=2 StartZ=0 EndX=1.55 EndY=2 EndZ=0
    g2: LineSegment StartX=2 StartY=1.55 StartZ=0 EndX=2 EndY=0.45 EndZ=0
    g3: LineSegment StartX=1.55 StartY=0 StartZ=0 EndX=0.45 EndY=0 EndZ=0
    g4: ArcOfCircle [constr] CenterX=0.45 CenterY=1.55 CenterZ=0 NormalX=0 NormalY=0 NormalZ=1 AngleXU=0 Radius=0.45 StartAngle=1.5708 EndAngle=3.14159
    g5: GeomPoint [constr] X=0 Y=2 Z=0
    g6: LineSegment StartX=0.45 StartY=2 StartZ=0 EndX=0 EndY=1.55 EndZ=0
    g7: ArcOfCircle [constr] CenterX=1.55 CenterY=1.55 CenterZ=0 NormalX=0 NormalY=0 NormalZ=1 AngleXU=0 Radius=0.45 StartAngle=0 EndAngle=1.5708
    g8: GeomPoint [constr] X=2 Y=2 Z=0
    g9: LineSegment StartX=2 StartY=1.55 StartZ=0 EndX=1.55 EndY=2 EndZ=0
    g10: ArcOfCircle [constr] CenterX=1.55 CenterY=0.45 CenterZ=0 NormalX=0 NormalY=0 NormalZ=1 AngleXU=0 Radius=0.45 StartAngle=4.71239 EndAngle=6.28319
    g11: GeomPoint [constr] X=2 Y=0 Z=0
    g12: LineSegment StartX=1.55 StartY=0 StartZ=0 EndX=2 EndY=0.45 EndZ=0
    g13: ArcOfCircle [constr] CenterX=0.45 CenterY=0.45 CenterZ=0 NormalX=0 NormalY=0 NormalZ=1 AngleXU=0 Radius=0.45 StartAngle=3.14159 EndAngle=4.71239
    g14: GeomPoint [constr] X=0 Y=0 Z=0
    g15: LineSegment StartX=0 StartY=0.45 StartZ=0 EndX=0.45 EndY=0 EndZ=0
  constraints (35):
    c: Coincident(g14,g-1)
    c: PointOnObject(g5,g-2)
    c: Horizontal(g1)
    c: Vertical(g2)
    c: Horizontal(g3)
    c: DistanceX(g5,g8) = 2
    c: DistanceY(g11,g8) = 2
    c: PointOnObject(g5,g0)
    c: PointOnObject(g5,g1)
    c: Tangent(g0,g4) = 1.5708
    c: Tangent(g1,g4) = 1.5708
    c: Coincident(g6,g0)
    c: Coincident(g6,g1)
    c: PointOnObject(g8,g2)
    c: PointOnObject(g8,g1)
    c: Tangent(g2,g7) = 1.5708
    c: Tangent(g1,g7) = 1.5708
    c: Coincident(g9,g2)
    c: Coincident(g9,g1)
    c: PointOnObject(g11,g2)
    c: PointOnObject(g11,g3)
    c: Tangent(g2,g10) = 1.5708
    c: Tangent(g3,g10) = 1.5708
    c: Coincident(g12,g2)
    c: Coincident(g12,g3)
    c: PointOnObject(g14,g0)
    c: PointOnObject(g14,g3)
    c: Tangent(g0,g13) = 1.5708
    c: Tangent(g3,g13) = 1.5708
    c: Coincident(g15,g0)
    c: Coincident(g15,g3)
    c: Equal(g6,g9)
    c: Equal(g9,g12)
    c: Equal(g12,g15)
    c: DistanceX(g14,g3) = 0.45
FEATURE [Sketcher::SketchObject] Sketch022  label="fori per M3x5(OD)x6(L)"
  ArcFitTolerance = 1e-06
  AttachmentSupport = -> [XZ_Plane]
  ExternalGeometry = -> [Sketch016]
  FullyConstrained = true
  MakeInternals = false
  MapMode = 5
  Placement = pos=(0,0,0) rot=(1,0,0;1.5708rad)
  sketch-geometry (7):
    g0: Circle CenterX=-5.6 CenterY=34.8 CenterZ=0 NormalX=0 NormalY=0 NormalZ=1 AngleXU=0 Radius=2.5
    g1: Circle CenterX=-5.6 CenterY=7.6 CenterZ=0 NormalX=0 NormalY=0 NormalZ=1 AngleXU=0 Radius=2.5
    g2: Circle CenterX=-78.51 CenterY=34.8 CenterZ=0 NormalX=0 NormalY=0 NormalZ=1 AngleXU=0 Radius=2.5
    g3: Circle CenterX=-78.51 CenterY=7.6 CenterZ=0 NormalX=0 NormalY=0 NormalZ=1 AngleXU=0 Radius=2.5
    g4: Circle CenterX=-184.08 CenterY=34.8 CenterZ=0 NormalX=0 NormalY=0 NormalZ=1 AngleXU=0 Radius=2.5
    g5: Circle CenterX=-179.305 CenterY=-76.8316 CenterZ=0 NormalX=0 NormalY=0 NormalZ=1 AngleXU=0 Radius=2.5
    g6: Circle CenterX=-213.443 CenterY=-76.8316 CenterZ=0 NormalX=0 NormalY=0 NormalZ=1 AngleXU=0 Radius=2.5
  constraints (14):
    c: Diameter(g0) = 5
    c: Diameter(g1) = 5
    c: Diameter(g2) = 5
    c: Diameter(g3) = 5
    c: Diameter(g4) = 5
    c: Diameter(g5) = 5
    c: Diameter(g6) = 5
    c: Coincident(g0,g-8)
    c: Coincident(g1,g-9)
    c: Coincident(g2,g-6)
    c: Coincident(g3,g-7)
    c: Coincident(g4,g-5)
    c: Coincident(g5,g-4)
    c: Coincident(g6,g-3)
FEATURE [Part::Extrusion] Extrude018  label="Extrude fori M3x5x6 - dx"
  Base = -> Sketch022
  Dir = (0,-1,2e-16)
  DirMode = 2
  FaceMakerClass = Part::FaceMakerBullseye
  FaceMakerMode = 3
  LengthFwd = 6.2
  LengthRev = 0
  Placement = pos=(0,-9.5,0) rot=(0,0,1;0rad)
  Solid = true
  Symmetric = true
FEATURE [Part::Extrusion] Extrude019  label="Extrude fori M3x5x6 - sx"
  Base = -> Sketch022
  Dir = (0,-1,2e-16)
  DirMode = 2
  FaceMakerClass = Part::FaceMakerBullseye
  FaceMakerMode = 3
  LengthFwd = 6.2
  LengthRev = 0
  Placement = pos=(0,9.5,0) rot=(0,0,1;0rad)
  Solid = true
  Symmetric = true
FEATURE [Sketcher::SketchObject] Sketch023  label="foro anteriore M3x5x6"
  ArcFitTolerance = 1e-06
  AttachmentSupport = -> [YZ_Plane]
  FullyConstrained = true
  MakeInternals = false
  MapMode = 5
  Placement = pos=(0,0,0) rot=(0.57735,0.57735,0.57735;2.0944rad)
  sketch-geometry (2):
    g0: LineSegment [constr] StartX=0 StartY=0 StartZ=0 EndX=0 EndY=38.6 EndZ=0
    g1: Circle CenterX=0 CenterY=38.6 CenterZ=0 NormalX=0 NormalY=0 NormalZ=1 AngleXU=0 Radius=2.5
  constraints (5):
    c: Coincident(g0,g-1)
    c: PointOnObject(g0,g-2)
    c: DistanceY(g0,g0) = 38.6
    c: Diameter(g1) = 5
    c: Coincident(g1,g0)
FEATURE [Part::Extrusion] Extrude020  label="Extrude foro anteriore M3x5x6"
  Base = -> Sketch023
  Dir = (1,0,0)
  DirMode = 2
  FaceMakerClass = Part::FaceMakerBullseye
  FaceMakerMode = 3
  LengthFwd = -6.2
  LengthRev = 0
  Solid = true
  Symmetric = false
FEATURE [Sketcher::SketchObject] Sketch024  label="fori per viti frontale"
  ArcFitTolerance = 1e-06
  AttachmentSupport = -> [YZ_Plane]
  FullyConstrained = true
  MakeInternals = false
  MapMode = 5
  Placement = pos=(0,0,0) rot=(0.57735,0.57735,0.57735;2.0944rad)
  sketch-geometry (9):
    g0: LineSegment [constr] StartX=-10.3 StartY=30.721 StartZ=0 EndX=10.3 EndY=30.721 EndZ=0
    g1: LineSegment [constr] StartX=10.3 StartY=30.721 StartZ=0 EndX=10.3 EndY=10.121 EndZ=0
    g2: LineSegment [constr] StartX=10.3 StartY=10.121 StartZ=0 EndX=-10.3 EndY=10.121 EndZ=0
    g3: LineSegment [constr] StartX=-10.3 StartY=10.121 StartZ=0 EndX=-10.3 EndY=30.721 EndZ=0
    g4: LineSegment [constr] StartX=0 StartY=0 StartZ=0 EndX=0 EndY=10.121 EndZ=0
    g5: Circle CenterX=-10.3 CenterY=30.721 CenterZ=0 NormalX=0 NormalY=0 NormalZ=1 AngleXU=0 Radius=2
    g6: Circle CenterX=10.3 CenterY=30.721 CenterZ=0 NormalX=0 NormalY=0 NormalZ=1 AngleXU=0 Radius=2
    g7: Circle CenterX=-10.3 CenterY=10.121 CenterZ=0 NormalX=0 NormalY=0 NormalZ=1 AngleXU=0 Radius=2
    g8: Circle CenterX=10.3 CenterY=10.121 CenterZ=0 NormalX=0 NormalY=0 NormalZ=1 AngleXU=0 Radius=2
  constraints (22):
    c: Horizontal(g0)
    c: Coincident(g1,g0)
    c: Vertical(g1)
    c: Coincident(g2,g1)
    c: Horizontal(g2)
    c: Coincident(g3,g2)
    c: Coincident(g3,g0)
    c: Vertical(g3)
    c: DistanceX(g0,g0) = 20.6
    c: DistanceY(g3,g3) = 20.6
    c: Coincident(g4,g-1)
    c: PointOnObject(g4,g-2)
    c: DistanceY(g4,g4) = 10.121
    c: Symmetric(g2,g2,g4)
    c: Diameter(g5) = 4
    c: Diameter(g6) = 4
    c: Diameter(g7) = 4
    c: Diameter(g8) = 4
    c: Coincident(g5,g0)
    c: Coincident(g6,g0)
    c: Coincident(g7,g2)
    c: Coincident(g8,g1)
FEATURE [Part::Extrusion] Extrude021  label="Extrude fori per viti frontale"
  Base = -> Sketch024
  Dir = (1,0,0)
  DirMode = 2
  FaceMakerClass = Part::FaceMakerBullseye
  FaceMakerMode = 3
  LengthFwd = -2.4
  LengthRev = 0
  Solid = true
  Symmetric = false
FEATURE [Sketcher::SketchObject] Sketch025  label="foro per filo CAM"
  ArcFitTolerance = 1e-06
  AttachmentSupport = -> [XZ_Plane]
  ExternalGeometry = -> [Sketch]
  FullyConstrained = true
  MakeInternals = false
  MapMode = 5
  Placement = pos=(0,0,0) rot=(1,0,0;1.5708rad)
  sketch-geometry (4):
    g0: LineSegment StartX=-44.6 StartY=41.2 StartZ=0 EndX=-44.6 EndY=36.4 EndZ=0
    g1: LineSegment StartX=-44.6 StartY=36.4 StartZ=0 EndX=-54.6 EndY=36.4 EndZ=0
    g2: LineSegment StartX=-54.6 StartY=36.4 StartZ=0 EndX=-50.4 EndY=41.2 EndZ=0
    g3: LineSegment StartX=-50.4 StartY=41.2 StartZ=0 EndX=-44.6 EndY=41.2 EndZ=0
  constraints (11):
    c: Vertical(g0)
    c: Coincident(g1,g0)
    c: Horizontal(g1)
    c: Coincident(g2,g1)
    c: Coincident(g3,g2)
    c: Coincident(g3,g0)
    c: Horizontal(g3)
    c: Coincident(g0,g-3)
    c: DistanceY(g0,g-4) = 0
    c: DistanceX(g3,g3) = 5.8
    c: DistanceX(g1,g1) = 10
FEATURE [Part::Extrusion] Extrude022  label="Extrude foro per filo CAM dx"
  Base = -> Sketch025
  Dir = (0,-1,2e-16)
  DirMode = 2
  FaceMakerClass = Part::FaceMakerBullseye
  FaceMakerMode = 3
  LengthFwd = 4.9
  LengthRev = 0
  Placement = pos=(0,6.95,0) rot=(0,0,1;0rad)
  Solid = true
  Symmetric = true
FEATURE [Part::Extrusion] Extrude023  label="Extrude foro per filo CAM sx"
  Base = -> Sketch025
  Dir = (0,-1,2e-16)
  DirMode = 2
  FaceMakerClass = Part::FaceMakerBullseye
  FaceMakerMode = 3
  LengthFwd = 4.9
  LengthRev = 0
  Placement = pos=(0,-6.95,0) rot=(0,0,1;0rad)
  Solid = true
  Symmetric = true
FEATURE [Sketcher::SketchObject] Sketch026  label="foro sotto anteriore M3x5x6"
  ArcFitTolerance = 1e-06
  AttachmentSupport = -> [XY_Plane]
  FullyConstrained = true
  MakeInternals = false
  MapMode = 5
  sketch-geometry (2):
    g0: LineSegment [constr] StartX=0 StartY=0 StartZ=0 EndX=-16.5 EndY=0 EndZ=0
    g1: Circle CenterX=-16.5 CenterY=0 CenterZ=0 NormalX=0 NormalY=0 NormalZ=1 AngleXU=0 Radius=2.5
  constraints (5):
    c: Distance(g0) = 16.5
    c: Coincident(g0,g-1)
    c: PointOnObject(g0,g-1)
    c: Diameter(g1) = 5
    c: Coincident(g0,g1)
FEATURE [Sketcher::SketchObject] Sketch027  label="foro sotto posteriore M3x5x6"
  ArcFitTolerance = 1e-06
  AttachmentSupport = -> [XY_Plane]
  ExternalGeometry = -> [Sketch]
  FullyConstrained = true
  MakeInternals = false
  MapMode = 5
  sketch-geometry (2):
    g0: LineSegment [constr] StartX=-82.8 StartY=2e-16 StartZ=0 EndX=-71.3 EndY=2e-16 EndZ=0
    g1: Circle CenterX=-71.3 CenterY=2e-16 CenterZ=0 NormalX=0 NormalY=0 NormalZ=1 AngleXU=0 Radius=2.5
  constraints (5):
    c: Distance(g0) = 11.5
    c: Coincident(g0,g-3)
    c: PointOnObject(g0,g-3)
    c: Diameter(g1) = 5
    c: Coincident(g1,g0)
FEATURE [Sketcher::SketchObject] Sketch029  label="fori sotto impugnatura"
  ArcFitTolerance = 1e-06
  AttachmentSupport = -> [XY_Plane]
  ExternalGeometry = -> [Sketch]
  FullyConstrained = true
  MakeInternals = false
  MapMode = 5
  sketch-geometry (15):
    g0: LineSegment [constr] StartX=-175.232 StartY=-1.83e-14 StartZ=0 EndX=-191.232 EndY=0 EndZ=0
    g1: Circle CenterX=-191.232 CenterY=0 CenterZ=0 NormalX=0 NormalY=0 NormalZ=1 AngleXU=0 Radius=3.95
    g2: LineSegment [constr] StartX=-175.232 StartY=-1.83e-14 StartZ=0 EndX=-204.275 EndY=0 EndZ=0
    g3: LineSegment StartX=-204.275 StartY=3.525 StartZ=0 EndX=-204.275 EndY=-3.525 EndZ=0
    g4: LineSegment StartX=-205.4 StartY=-4.65 StartZ=0 EndX=-206.65 EndY=-4.65 EndZ=0
    g5: LineSegment StartX=-207.775 StartY=-3.525 StartZ=0 EndX=-207.775 EndY=3.525 EndZ=0
    g6: LineSegment StartX=-206.65 StartY=4.65 StartZ=0 EndX=-205.4 EndY=4.65 EndZ=0
    g7: ArcOfCircle CenterX=-206.65 CenterY=3.525 CenterZ=0 NormalX=0 NormalY=0 NormalZ=1 AngleXU=0 Radius=1.125 StartAngle=1.5708 EndAngle=3.14159
    g8: GeomPoint [constr] X=-207.775 Y=4.65 Z=0
    g9: ArcOfCircle CenterX=-205.4 CenterY=3.525 CenterZ=0 NormalX=0 NormalY=0 NormalZ=1 AngleXU=0 Radius=1.125 StartAngle=0 EndAngle=1.5708
    g10: GeomPoint [constr] X=-204.275 Y=4.65 Z=0
    g11: ArcOfCircle CenterX=-205.4 CenterY=-3.525 CenterZ=0 NormalX=0 NormalY=0 NormalZ=1 AngleXU=0 Radius=1.125 StartAngle=4.71239 EndAngle=6.28319
    g12: GeomPoint [constr] X=-204.275 Y=-4.65 Z=0
    g13: ArcOfCircle CenterX=-206.65 CenterY=-3.525 CenterZ=0 NormalX=0 NormalY=0 NormalZ=1 AngleXU=0 Radius=1.125 StartAngle=3.14159 EndAngle=4.71239
    g14: GeomPoint [constr] X=-207.775 Y=-4.65 Z=0
  constraints (35):
    c: Distance(g0) = 16
    c: Coincident(g0,g-3)
    c: PointOnObject(g0,g-1)
    c: Diameter(g1) = 7.9
    c: Coincident(g1,g0)
    c: Coincident(g2,g0)
    c: PointOnObject(g2,g-1)
    c: Vertical(g3)
    c: Horizontal(g4)
    c: Vertical(g5)
    c: Horizontal(g6)
    c: DistanceY(g12,g10) = 9.3
    c: DistanceX(g8,g10) = 3.5
    c: Symmetric(g10,g12,g2)
    c: PointOnObject(g8,g5)
    c: PointOnObject(g8,g6)
    c: Tangent(g5,g7) = 1.5708
    c: Tangent(g6,g7) = 1.5708
    c: PointOnObject(g10,g3)
    c: PointOnObject(g10,g6)
    c: Tangent(g3,g9) = 1.5708
    c: Tangent(g6,g9) = 1.5708
    c: PointOnObject(g12,g3)
    c: PointOnObject(g12,g4)
    c: Tangent(g3,g11) = 1.5708
    c: Tangent(g4,g11) = 1.5708
    c: PointOnObject(g14,g4)
    c: PointOnObject(g14,g5)
    c: Tangent(g4,g13) = 1.5708
    c: Tangent(g5,g13) = 1.5708
    c: Equal(g7,g9)
    c: Equal(g9,g11)
    c: Equal(g11,g13)
    c: DistanceX(g6,g6) = 1.25
    c: DistanceX(g-5,g5) = 6.8
FEATURE [Sketcher::SketchObject] Sketch030  label="fori superiori per solenoide e oled"
  ArcFitTolerance = 1e-06
  AttachmentSupport = -> [XY_Plane]
  ExternalGeometry = -> [Sketch]
  FullyConstrained = true
  MakeInternals = false
  MapMode = 5
  sketch-geometry (33):
    g0: LineSegment [constr] StartX=-181.6 StartY=1.12e-14 StartZ=0 EndX=-169.91 EndY=0 EndZ=0
    g1: LineSegment [constr] StartX=-169.91 StartY=0 StartZ=0 EndX=-169.91 EndY=-2.6 EndZ=0
    g2: LineSegment [constr] StartX=-169.91 StartY=0 StartZ=0 EndX=-169.91 EndY=2.6 EndZ=0
    g3: LineSegment StartX=-169.91 StartY=4.975 StartZ=0 EndX=-169.91 EndY=8.225 EndZ=0
    g4: LineSegment StartX=-167.535 StartY=10.6 StartZ=0 EndX=-167.285 EndY=10.6 EndZ=0
    g5: LineSegment StartX=-164.91 StartY=8.225 StartZ=0 EndX=-164.91 EndY=4.975 EndZ=0
    g6: LineSegment StartX=-167.285 StartY=2.6 StartZ=0 EndX=-167.535 EndY=2.6 EndZ=0
    g7: LineSegment StartX=-169.91 StartY=-4.975 StartZ=0 EndX=-169.91 EndY=-8.225 EndZ=0
    g8: LineSegment StartX=-167.535 StartY=-10.6 StartZ=0 EndX=-167.285 EndY=-10.6 EndZ=0
    g9: LineSegment StartX=-164.91 StartY=-8.225 StartZ=0 EndX=-164.91 EndY=-4.975 EndZ=0
    g10: LineSegment StartX=-167.285 StartY=-2.6 StartZ=0 EndX=-167.535 EndY=-2.6 EndZ=0
    g11: ArcOfCircle CenterX=-167.535 CenterY=8.225 CenterZ=0 NormalX=0 NormalY=0 NormalZ=1 AngleXU=0 Radius=2.375 StartAngle=1.5708 EndAngle=3.14159
    g12: GeomPoint [constr] X=-169.91 Y=10.6 Z=0
    g13: ArcOfCircle CenterX=-167.285 CenterY=8.225 CenterZ=0 NormalX=0 NormalY=0 NormalZ=1 AngleXU=0 Radius=2.375 StartAngle=0 EndAngle=1.5708
    g14: GeomPoint [constr] X=-164.91 Y=10.6 Z=0
    g15: ArcOfCircle CenterX=-167.285 CenterY=4.975 CenterZ=0 NormalX=0 NormalY=0 NormalZ=1 AngleXU=0 Radius=2.375 StartAngle=4.71239 EndAngle=6.28319
    g16: GeomPoint [constr] X=-164.91 Y=2.6 Z=0
    g17: ArcOfCircle CenterX=-167.535 CenterY=4.975 CenterZ=0 NormalX=0 NormalY=0 NormalZ=1 AngleXU=0 Radius=2.375 StartAngle=3.14159 EndAngle=4.71239
    g18: GeomPoint [constr] X=-169.91 Y=2.6 Z=0
    g19: ArcOfCircle CenterX=-167.535 CenterY=-4.975 CenterZ=0 NormalX=0 NormalY=0 NormalZ=1 AngleXU=0 Radius=2.375 StartAngle=1.5708 EndAngle=3.14159
    g20: GeomPoint [constr] X=-169.91 Y=-2.6 Z=0
    g21: ArcOfCircle CenterX=-167.285 CenterY=-4.975 CenterZ=0 NormalX=0 NormalY=0 NormalZ=1 AngleXU=0 Radius=2.375 StartAngle=0 EndAngle=1.5708
    g22: GeomPoint [constr] X=-164.91 Y=-2.6 Z=0
    g23: ArcOfCircle CenterX=-167.285 CenterY=-8.225 CenterZ=0 NormalX=0 NormalY=0 NormalZ=1 AngleXU=0 Radius=2.375 StartAngle=4.71239 EndAngle=6.28319
    g24: GeomPoint [constr] X=-164.91 Y=-10.6 Z=0
    g25: ArcOfCircle CenterX=-167.535 CenterY=-8.225 CenterZ=0 NormalX=0 NormalY=0 NormalZ=1 AngleXU=0 Radius=2.375 StartAngle=3.14159 EndAngle=4.71239
    g26: GeomPoint [constr] X=-169.91 Y=-10.6 Z=0
    g27: LineSegment [constr] StartX=-181.6 StartY=1.12e-14 StartZ=0 EndX=-152.209 EndY=0 EndZ=0
    g28: LineSegment [constr] StartX=-181.6 StartY=1.12e-14 StartZ=0 EndX=-130.41 EndY=0 EndZ=0
    g29: LineSegment [constr] StartX=-152.209 StartY=0 StartZ=0 EndX=-152.209 EndY=6.95 EndZ=0
    g30: LineSegment [constr] StartX=-130.41 StartY=0 StartZ=0 EndX=-130.41 EndY=-6.95 EndZ=0
    g31: Circle CenterX=-152.209 CenterY=6.95 CenterZ=0 NormalX=0 NormalY=0 NormalZ=1 AngleXU=0 Radius=2.1
    g32: Circle CenterX=-130.41 CenterY=-6.95 CenterZ=0 NormalX=0 NormalY=0 NormalZ=1 AngleXU=0 Radius=2.1
  constraints (79):
    c: Distance(g0) = 11.69
    c: PointOnObject(g0,g-1)
    c: Coincident(g-4,g0)
    c: Distance(g1) = 2.6
    c: Coincident(g1,g0)
    c: Vertical(g1)
    c: Distance(g2) = 2.6
    c: Coincident(g2,g0)
    c: Vertical(g2)
    c: Distance(g18,g12) = 8
    c: Coincident(g18,g2)
    c: Vertical(g3)
    c: Distance(g14,g12) = 5
    c: Horizontal(g4)
    c: Distance(g16,g14) = 8
    c: Vertical(g5)
    c: Distance(g26,g20) = 8
    c: Coincident(g20,g1)
    c: Vertical(g7)
    c: Distance(g26,g24) = 5
    c: Horizontal(g8)
    c: Distance(g24,g22) = 8
    c: Vertical(g9)
    c: PointOnObject(g12,g3)
    c: PointOnObject(g12,g4)
    c: Tangent(g3,g11) = 1.5708
    c: Tangent(g4,g11) = 1.5708
    c: PointOnObject(g14,g5)
    c: PointOnObject(g14,g4)
    c: Tangent(g5,g13) = 1.5708
    c: Tangent(g4,g13) = 1.5708
    c: PointOnObject(g16,g5)
    c: PointOnObject(g16,g6)
    c: Tangent(g5,g15) = 1.5708
    c: Tangent(g6,g15) = 1.5708
    c: PointOnObject(g18,g3)
    c: PointOnObject(g18,g6)
    c: Tangent(g3,g17) = 1.5708
    c: Tangent(g6,g17) = 1.5708
    c: Equal(g11,g13)
    c: Equal(g13,g15)
    c: Equal(g15,g17)
    c: DistanceX(g4,g4) = 0.25
    c: PointOnObject(g20,g7)
    c: PointOnObject(g20,g10)
    c: Tangent(g7,g19) = -1.5708
    c: Tangent(g10,g19) = -1.5708
    c: PointOnObject(g22,g9)
    c: PointOnObject(g22,g10)
    c: Tangent(g9,g21) = -1.5708
    c: Tangent(g10,g21) = -1.5708
    c: PointOnObject(g24,g9)
    c: PointOnObject(g24,g8)
    c: Tangent(g9,g23) = -1.5708
    c: Tangent(g8,g23) = -1.5708
    c: PointOnObject(g26,g8)
    c: PointOnObject(g26,g7)
    c: Tangent(g8,g25) = -1.5708
    c: Tangent(g7,g25) = -1.5708
    c: Equal(g19,g21)
    c: Equal(g21,g23)
    c: Equal(g23,g25)
    c: DistanceX(g10,g10) = 0.25
    c: Distance(g27) = 29.391
    c: Coincident(g27,g0)
    c: PointOnObject(g27,g-1)
    c: Distance(g28) = 51.19
    c: Coincident(g28,g0)
    c: PointOnObject(g28,g-1)
    c: Distance(g29) = 6.95
    c: Coincident(g29,g27)
    c: Vertical(g29)
    c: Distance(g30) = 6.95
    c: Coincident(g30,g28)
    c: Vertical(g30)
    c: Diameter(g31) = 4.2
    c: Diameter(g32) = 4.2
    c: Coincident(g32,g30)
    c: Coincident(g31,g29)
FEATURE [Sketcher::SketchObject] Sketch031  label="fori inferiori switch pompa"
  ArcFitTolerance = 1e-06
  AttachmentSupport = -> [XY_Plane]
  ExternalGeometry = -> [Sketch]
  FullyConstrained = true
  MakeInternals = false
  MapMode = 5
  sketch-geometry (4):
    g0: LineSegment [constr] StartX=-57.2 StartY=1.9e-15 StartZ=0 EndX=-62.45 EndY=1.9e-15 EndZ=0
    g1: LineSegment [constr] StartX=-62.45 StartY=3.25 StartZ=0 EndX=-62.45 EndY=-3.25 EndZ=0
    g2: Circle CenterX=-62.45 CenterY=3.25 CenterZ=0 NormalX=0 NormalY=0 NormalZ=1 AngleXU=0 Radius=1.6
    g3: Circle CenterX=-62.45 CenterY=-3.25 CenterZ=0 NormalX=0 NormalY=0 NormalZ=1 AngleXU=0 Radius=1.6
  constraints (10):
    c: Distance(g0) = 5.25
    c: Coincident(g0,g-3)
    c: PointOnObject(g0,g-3)
    c: Vertical(g1)
    c: DistanceY(g1,g1) = 6.5
    c: Symmetric(g1,g1,g0)
    c: Diameter(g2) = 3.2
    c: Diameter(g3) = 3.2
    c: Coincident(g2,g1)
    c: Coincident(g3,g1)
FEATURE [Sketcher::SketchObject] Sketch032  label="spazio per PILA 18650"
  ArcFitTolerance = 1e-06
  AttachmentSupport = -> [XY_Plane]
  ExternalGeometry = -> [Sketch]
  FullyConstrained = true
  MakeInternals = false
  MapMode = 5
  sketch-geometry (2):
    g0: LineSegment [constr] StartX=-178.142 StartY=-1.74e-14 StartZ=0 EndX=-190.142 EndY=-1.83e-14 EndZ=0
    g1: Circle CenterX=-190.142 CenterY=-1.83e-14 CenterZ=0 NormalX=0 NormalY=0 NormalZ=1 AngleXU=0 Radius=9.25
  constraints (5):
    c: Distance(g0) = 12
    c: Coincident(g0,g-3)
    c: PointOnObject(g0,g-4)
    c: Diameter(g1) = 18.5
    c: Coincident(g1,g0)
FEATURE [Part::Extrusion] Extrude030  label="Extrude spazio per PILA 18650"
  Base = -> Sketch032
  Dir = (0,0,1)
  DirLink = -> Sketch [Edge45]
  DirMode = 2
  FaceMakerClass = Part::FaceMakerBullseye
  FaceMakerMode = 3
  LengthFwd = 68
  LengthRev = 0
  Placement = pos=(6,0,-72.7) rot=(0,0,1;0rad)
  Solid = true
  Symmetric = false
FEATURE [Sketcher::SketchObject] Sketch033  label="fermo per scheda micro"
  ArcFitTolerance = 1e-06
  AttachmentSupport = -> [XZ_Plane]
  ExternalGeometry = -> [Sketch]
  FullyConstrained = true
  MakeInternals = false
  MapMode = 5
  Placement = pos=(0,0,0) rot=(1,0,0;1.5708rad)
  sketch-geometry (12):
    g0: LineSegment StartX=-11.6 StartY=6 StartZ=0 EndX=-4 EndY=6 EndZ=0
    g1: LineSegment StartX=-4 StartY=6 StartZ=0 EndX=-4 EndY=36.4 EndZ=0
    g2: LineSegment StartX=-4 StartY=36.4 StartZ=0 EndX=-11.6 EndY=36.4 EndZ=0
    g3: LineSegment StartX=-11.6 StartY=36.4 StartZ=0 EndX=-11.6 EndY=6 EndZ=0
    g4: LineSegment StartX=-80.11 StartY=11.6 StartZ=0 EndX=-70.51 EndY=11.6 EndZ=0
    g5: LineSegment StartX=-70.51 StartY=11.6 StartZ=0 EndX=-70.51 EndY=6 EndZ=0
    g6: LineSegment StartX=-70.51 StartY=6 StartZ=0 EndX=-80.11 EndY=6 EndZ=0
    g7: LineSegment StartX=-80.11 StartY=6 StartZ=0 EndX=-80.11 EndY=11.6 EndZ=0
    g8: LineSegment StartX=-78.51 StartY=36.4 StartZ=0 EndX=-70.51 EndY=36.4 EndZ=0
    g9: LineSegment StartX=-70.51 StartY=36.4 StartZ=0 EndX=-70.51 EndY=30.8 EndZ=0
    g10: LineSegment StartX=-70.51 StartY=30.8 StartZ=0 EndX=-78.51 EndY=30.8 EndZ=0
    g11: LineSegment StartX=-78.51 StartY=30.8 StartZ=0 EndX=-78.51 EndY=36.4 EndZ=0
  constraints (33):
    c: Horizontal(g0)
    c: Coincident(g1,g0)
    c: Coincident(g2,g1)
    c: Horizontal(g2)
    c: Coincident(g3,g2)
    c: Coincident(g3,g0)
    c: Vertical(g3)
    c: DistanceX(g2,g2) = 7.6
    c: Coincident(g1,g-3)
    c: Coincident(g0,g-3)
    c: Horizontal(g4)
    c: Coincident(g5,g4)
    c: Vertical(g5)
    c: Coincident(g6,g5)
    c: Horizontal(g6)
    c: Coincident(g7,g6)
    c: Coincident(g7,g4)
    c: Vertical(g7)
    c: DistanceY(g5,g5) = 5.6
    c: DistanceX(g4,g4) = 9.6
    c: Coincident(g9,g8)
    c: Vertical(g9)
    c: Coincident(g10,g9)
    c: Horizontal(g10)
    c: Coincident(g11,g10)
    c: Coincident(g11,g8)
    c: Vertical(g11)
    c: DistanceY(g9,g9) = 5.6
    c: DistanceX(g10,g10) = 8
    c: Coincident(g4,g-4)
    c: DistanceX(g4,g10) = 1.6
    c: Horizontal(g8)
    c: DistanceY(g8,g1) = 0
FEATURE [Sketcher::SketchObject] Sketch034  label="buchi guida rail"
  ArcFitTolerance = 1e-06
  AttachmentSupport = -> [XY_Plane]
  ExternalGeometry = -> [Sketch]
  FullyConstrained = true
  MakeInternals = false
  MapMode = 5
  sketch-geometry (6):
    g0: LineSegment [constr] StartX=-100.8 StartY=9.1e-15 StartZ=0 EndX=-93.3 EndY=0 EndZ=0
    g1: LineSegment [constr] StartX=-93.3 StartY=0 StartZ=0 EndX=-73.3 EndY=0 EndZ=0
    g2: LineSegment [constr] StartX=-73.3 StartY=0 StartZ=0 EndX=-53.3 EndY=0 EndZ=0
    g3: Circle CenterX=-93.3 CenterY=0 CenterZ=0 NormalX=0 NormalY=0 NormalZ=1 AngleXU=0 Radius=2.5
    g4: Circle CenterX=-73.3 CenterY=0 CenterZ=0 NormalX=0 NormalY=0 NormalZ=1 AngleXU=0 Radius=2.5
    g5: Circle CenterX=-53.3 CenterY=0 CenterZ=0 NormalX=0 NormalY=0 NormalZ=1 AngleXU=0 Radius=2.5
  constraints (15):
    c: Distance(g0) = 7.5
    c: Coincident(g0,g-3)
    c: PointOnObject(g0,g-1)
    c: Distance(g1) = 20
    c: Coincident(g1,g0)
    c: PointOnObject(g1,g-1)
    c: Distance(g2) = 20
    c: Coincident(g2,g1)
    c: PointOnObject(g2,g-1)
    c: Diameter(g3) = 5
    c: Diameter(g4) = 5
    c: Diameter(g5) = 5
    c: Coincident(g3,g0)
    c: Coincident(g4,g1)
    c: Coincident(g5,g2)
FEATURE [Part::Extrusion] Extrude032  label="Extrude buchi guida rail"
  Base = -> Sketch034
  Dir = (0,0,1)
  DirMode = 2
  FaceMakerClass = Part::FaceMakerBullseye
  FaceMakerMode = 3
  LengthFwd = -6.2
  LengthRev = 0
  Placement = pos=(0,0,43.2) rot=(0,0,1;0rad)
  Solid = true
  Symmetric = false
FEATURE [Part::Extrusion] Extrude033  label="Extrude fori superiori per solenoide e oled001"
  Base = -> Sketch030
  Dir = (0,0,1)
  DirMode = 2
  FaceMakerClass = Part::FaceMakerBullseye
  FaceMakerMode = 3
  LengthFwd = -4.8
  LengthRev = 0
  Placement = pos=(0,0,41.2) rot=(0,0,1;0rad)
  Solid = true
  Symmetric = false
FEATURE [Part::Extrusion] Extrude034  label="Extrude fori sotto impugnatura001"
  Base = -> Sketch029
  Dir = (0,0,1)
  DirMode = 2
  FaceMakerClass = Part::FaceMakerBullseye
  FaceMakerMode = 3
  LengthFwd = 5
  LengthRev = 0
  Placement = pos=(0,0,-83) rot=(0,0,1;0rad)
  Solid = true
  Symmetric = false
FEATURE [Part::Extrusion] Extrude035  label="Extrude fori inferiori switch pompa001"
  Base = -> Sketch031
  Dir = (0,0,1)
  DirMode = 2
  FaceMakerClass = Part::FaceMakerBullseye
  FaceMakerMode = 3
  LengthFwd = 4
  LengthRev = 0
  Placement = pos=(0,0,-1.7) rot=(0,0,1;0rad)
  Solid = true
  Symmetric = false
FEATURE [Part::Extrusion] Extrude036  label="Extrude foro sotto posteriore M3x5x007"
  Base = -> Sketch027
  Dir = (0,0,1)
  DirMode = 2
  FaceMakerClass = Part::FaceMakerBullseye
  FaceMakerMode = 3
  LengthFwd = 6.2
  LengthRev = 0
  Placement = pos=(0,0,-9.6) rot=(0,0,1;0rad)
  Solid = true
  Symmetric = false
FEATURE [Part::Extrusion] Extrude037  label="Extrude foro sotto anteriore M3x5x007"
  Base = -> Sketch026
  Dir = (0,0,1)
  DirMode = 2
  FaceMakerClass = Part::FaceMakerBullseye
  FaceMakerMode = 3
  LengthFwd = 6.2
  LengthRev = 0
  Solid = true
  Symmetric = false
FEATURE [Sketcher::SketchObject] Sketch035  label="foro per fissaggio micro"
  ArcFitTolerance = 1e-06
  AttachmentSupport = -> [XZ_Plane]
  ExternalGeometry = -> [Sketch,Sketch033]
  FullyConstrained = true
  MakeInternals = false
  MapMode = 5
  Placement = pos=(0,0,0) rot=(1,0,0;1.5708rad)
  sketch-geometry (3):
    g0: Circle CenterX=-7.8 CenterY=21.2 CenterZ=0 NormalX=0 NormalY=0 NormalZ=1 AngleXU=0 Radius=1.6
    g1: GeomPoint [constr] X=-4 Y=21.2 Z=0
    g2: LineSegment [constr] StartX=-4 StartY=21.2 StartZ=0 EndX=-11.6 EndY=21.2 EndZ=0
  constraints (6):
    c: Diameter(g0) = 3.2
    c: Symmetric(g-3,g-3,g1)
    c: Coincident(g2,g1)
    c: Horizontal(g2)
    c: DistanceX(g-4,g2) = 0
    c: Symmetric(g2,g1,g0)
FEATURE [Part::Extrusion] Extrude038  label="Extrude foro per fissaggio micro"
  Base = -> Sketch035
  Dir = (0,-1,2e-16)
  DirMode = 2
  FaceMakerClass = Part::FaceMakerBullseye
  FaceMakerMode = 3
  LengthFwd = 3
  LengthRev = 0
  Placement = pos=(0,8.6,0) rot=(0,0,1;0rad)
  Solid = true
  Symmetric = false
FEATURE [Sketcher::SketchObject] Sketch036  label="supporto per alimentatore"
  ArcFitTolerance = 1e-06
  AttachmentSupport = -> [XZ_Plane]
  ExternalGeometry = -> [Sketch,Sketch016,Sketch022]
  FullyConstrained = true
  MakeInternals = false
  MapMode = 5
  Placement = pos=(0,0,0) rot=(1,0,0;1.5708rad)
  sketch-geometry (5):
    g0: LineSegment StartX=-211.843 StartY=-50.0944 StartZ=0 EndX=-211.843 EndY=-80.4316 EndZ=0
    g1: LineSegment StartX=-211.843 StartY=-50.0944 StartZ=0 EndX=-207.775 EndY=-41.3701 EndZ=0
    g2: LineSegment [constr] StartX=-209.443 StartY=-50.0944 StartZ=0 EndX=-209.443 EndY=-80.4316 EndZ=0
    g3: LineSegment StartX=-207.775 StartY=-41.3701 StartZ=0 EndX=-207.775 EndY=-80.4316 EndZ=0
    g4: LineSegment StartX=-211.843 StartY=-80.4316 StartZ=0 EndX=-207.775 EndY=-80.4316 EndZ=0
  constraints (15):
    c: Vertical(g0)
    c: Coincident(g1,g0)
    c: Vertical(g2)
    c: Tangent(g2,g-5)
    c: Coincident(g3,g1)
    c: Vertical(g3)
    c: DistanceY(g-3,g3) = -2
    c: Tangent(g1,g-8)
    c: DistanceY(g-3,g0) = -2
    c: Coincident(g4,g0)
    c: Coincident(g4,g3)
    c: Tangent(g0,g-6)
    c: DistanceY(g-3,g2) = -2
    c: DistanceY(g2,g0) = 0
    c: DistanceX(g-3,g3) = 6.8
FEATURE [Part::Extrusion] Extrude039  label="Extrude039 supporto alimentatore"
  Base = -> Sketch036
  Dir = (0,-1,2e-16)
  DirMode = 2
  FaceMakerClass = Part::FaceMakerBullseye
  FaceMakerMode = 3
  LengthFwd = 25.2
  LengthRev = 0
  Solid = true
  Symmetric = true
FEATURE [Sketcher::SketchObject] Sketch037  label="scavo per alimentatore"
  ArcFitTolerance = 1e-06
  AttachmentSupport = -> [XZ_Plane]
  ExternalGeometry = -> [Sketch036]
  FullyConstrained = true
  MakeInternals = false
  MapMode = 5
  Placement = pos=(0,0,0) rot=(1,0,0;1.5708rad)
  sketch-geometry (4):
    g0: LineSegment StartX=-209.575 StartY=-50.4316 StartZ=0 EndX=-209.575 EndY=-80.4316 EndZ=0
    g1: LineSegment StartX=-209.575 StartY=-50.4316 StartZ=0 EndX=-207.775 EndY=-50.4316 EndZ=0
    g2: LineSegment StartX=-207.775 StartY=-50.4316 StartZ=0 EndX=-207.775 EndY=-80.4316 EndZ=0
    g3: LineSegment StartX=-207.775 StartY=-80.4316 StartZ=0 EndX=-209.575 EndY=-80.4316 EndZ=0
  constraints (11):
    c: Vertical(g0)
    c: Coincident(g1,g0)
    c: Horizontal(g1)
    c: Coincident(g2,g1)
    c: Vertical(g2)
    c: Coincident(g3,g2)
    c: Coincident(g3,g0)
    c: Horizontal(g3)
    c: DistanceX(g1,g1) = 1.8
    c: Coincident(g2,g-3)
    c: DistanceY(g2,g2) = 30
FEATURE [Part::Extrusion] Extrude040  label="Extrude040 scavo alimentatore"
  Base = -> Sketch037
  Dir = (0,-1,2e-16)
  DirMode = 2
  FaceMakerClass = Part::FaceMakerBullseye
  FaceMakerMode = 3
  LengthFwd = 19.5
  LengthRev = 0
  Solid = true
  Symmetric = true
FEATURE [Part::Extrusion] Extrude031  label="Extrude fermo per scheda micro"
  Base = -> Sketch033
  Dir = (0,-1,2e-16)
  DirMode = 2
  FaceMakerClass = Part::FaceMakerBullseye
  FaceMakerMode = 3
  LengthFwd = 3
  LengthRev = 0
  Placement = pos=(0,8.6,0) rot=(0,0,1;0rad)
  Solid = true
  Symmetric = false
FEATURE [Sketcher::SketchObject] Sketch038  label="scavo driver solenoide"
  ArcFitTolerance = 1e-06
  AttachmentSupport = -> [XZ_Plane]
  ExternalGeometry = -> [Sketch,Sketch036]
  FullyConstrained = true
  MakeInternals = false
  MapMode = 5
  Placement = pos=(0,0,0) rot=(1,0,0;1.5708rad)
  sketch-geometry (7):
    g0: LineSegment StartX=-193.66 StartY=-11.0994 StartZ=0 EndX=-195.11 EndY=-10.4232 EndZ=0
    g1: LineSegment StartX=-195.11 StartY=-10.4232 StartZ=0 EndX=-209.225 EndY=-40.6939 EndZ=0
    g2: LineSegment StartX=-193.66 StartY=-11.0994 StartZ=0 EndX=-190.216 EndY=-12.7054 EndZ=0
    g3: LineSegment StartX=-190.216 StartY=-12.7054 StartZ=0 EndX=-204.331 EndY=-42.9761 EndZ=0
    g4: LineSegment StartX=-204.331 StartY=-42.9761 StartZ=0 EndX=-207.775 EndY=-41.3701 EndZ=0
    g5: LineSegment [constr] StartX=-209.225 StartY=-40.6939 StartZ=0 EndX=-207.775 EndY=-41.3701 EndZ=0
    g6: LineSegment StartX=-209.225 StartY=-40.6939 StartZ=0 EndX=-207.775 EndY=-41.3701 EndZ=0
  constraints (19):
    c: Coincident(g1,g0)
    c: Coincident(g3,g2)
    c: Coincident(g4,g3)
    c: Distance(g2) = 3.8
    c: Distance(g1) = 33.4
    c: Coincident(g5,g1)
    c: Distance(g5) = 1.6
    c: Coincident(g-4,g5)
    c: Perpendicular(g5,g-3)
    c: Parallel(g1,g-3)
    c: Perpendicular(g1,g0)
    c: Distance(g0) = 1.6
    c: Coincident(g6,g1)
    c: Coincident(g6,g5)
    c: Parallel(g3,g-3)
    c: Perpendicular(g3,g4)
    c: Perpendicular(g2,g3)
    c: Coincident(g2,g0)
    c: Coincident(g4,g5)
FEATURE [Part::Extrusion] Extrude041  label="Extrude scavo driver solenoide"
  Base = -> Sketch038
  Dir = (0,-1,2e-16)
  DirMode = 2
  FaceMakerClass = Part::FaceMakerBullseye
  FaceMakerMode = 3
  LengthFwd = 17
  LengthRev = 0
  Solid = true
  Symmetric = true
FEATURE [Sketcher::SketchObject] Sketch039  label="scavo per cavo usb per micro"
  ArcFitTolerance = 1e-06
  AttachmentSupport = -> [XZ_Plane]
  ExternalGeometry = -> [Sketch,Sketch016]
  FullyConstrained = true
  MakeInternals = false
  MapMode = 5
  Placement = pos=(0,0,0) rot=(1,0,0;1.5708rad)
  sketch-geometry (4):
    g0: LineSegment StartX=-82.51 StartY=36.4 StartZ=0 EndX=-74.51 EndY=36.4 EndZ=0
    g1: LineSegment StartX=-74.51 StartY=36.4 StartZ=0 EndX=-74.51 EndY=30.8 EndZ=0
    g2: LineSegment StartX=-74.51 StartY=30.8 StartZ=0 EndX=-82.51 EndY=30.8 EndZ=0
    g3: LineSegment StartX=-82.51 StartY=30.8 StartZ=0 EndX=-82.51 EndY=36.4 EndZ=0
  constraints (11):
    c: Coincident(g1,g0)
    c: Vertical(g1)
    c: Coincident(g2,g1)
    c: Horizontal(g2)
    c: Coincident(g3,g2)
    c: Coincident(g3,g0)
    c: Vertical(g3)
    c: Tangent(g0,g-3)
    c: Tangent(g2,g-4)
    c: Tangent(g3,g-4)
    c: Tangent(g1,g-4)
FEATURE [Part::Extrusion] Extrude042  label="Extrude scavo per cavo usb per micro"
  Base = -> Sketch039
  Dir = (0,-1,2e-16)
  DirMode = 2
  FaceMakerClass = Part::FaceMakerBullseye
  FaceMakerMode = 3
  LengthFwd = 11.2
  LengthRev = 0
  Solid = true
  Symmetric = true
FEATURE [Sketcher::SketchObject] Sketch040  label="scavo saldature alimentatore connettore 5v"
  ArcFitTolerance = 1e-06
  AttachmentSupport = -> [XZ_Plane]
  ExternalGeometry = -> [Sketch037]
  FullyConstrained = true
  MakeInternals = false
  MapMode = 5
  Placement = pos=(0,0,0) rot=(1,0,0;1.5708rad)
  sketch-geometry (4):
    g0: LineSegment StartX=-211.175 StartY=-52.4316 StartZ=0 EndX=-211.175 EndY=-56.4316 EndZ=0
    g1: LineSegment StartX=-211.175 StartY=-52.4316 StartZ=0 EndX=-209.575 EndY=-52.4316 EndZ=0
    g2: LineSegment StartX=-209.575 StartY=-52.4316 StartZ=0 EndX=-209.575 EndY=-56.4316 EndZ=0
    g3: LineSegment StartX=-209.575 StartY=-56.4316 StartZ=0 EndX=-211.175 EndY=-56.4316 EndZ=0
  constraints (11):
    c: Vertical(g0)
    c: Coincident(g1,g0)
    c: Horizontal(g1)
    c: Coincident(g2,g1)
    c: Coincident(g3,g2)
    c: Coincident(g3,g0)
    c: Horizontal(g3)
    c: DistanceX(g1,g1) = 1.6
    c: DistanceY(g2,g2) = 4
    c: Tangent(g2,g-3)
    c: DistanceY(g1,g-3) = 2
FEATURE [Part::Extrusion] Extrude043  label="Extrude scavo saldature alimentatore connettore 5v"
  Base = -> Sketch040
  Dir = (0,-1,2e-16)
  DirMode = 2
  FaceMakerClass = Part::FaceMakerBullseye
  FaceMakerMode = 3
  LengthFwd = 8
  LengthRev = 0
  Solid = true
  Symmetric = true
FEATURE [Sketcher::SketchObject] Sketch041  label="scavo saldature alimentatore connettore 5v verticali"
  ArcFitTolerance = 1e-06
  AttachmentSupport = -> [XZ_Plane]
  ExternalGeometry = -> [Sketch037]
  FullyConstrained = true
  MakeInternals = false
  MapMode = 5
  Placement = pos=(0,0,0) rot=(1,0,0;1.5708rad)
  sketch-geometry (4):
    g0: LineSegment StartX=-211.175 StartY=-53.6316 StartZ=0 EndX=-209.575 EndY=-53.6316 EndZ=0
    g1: LineSegment StartX=-209.575 StartY=-53.6316 StartZ=0 EndX=-209.575 EndY=-76.6316 EndZ=0
    g2: LineSegment StartX=-209.575 StartY=-76.6316 StartZ=0 EndX=-211.175 EndY=-76.6316 EndZ=0
    g3: LineSegment StartX=-211.175 StartY=-76.6316 StartZ=0 EndX=-211.175 EndY=-53.6316 EndZ=0
  constraints (11):
    c: Horizontal(g0)
    c: Coincident(g1,g0)
    c: Coincident(g2,g1)
    c: Horizontal(g2)
    c: Coincident(g3,g2)
    c: Coincident(g3,g0)
    c: Vertical(g3)
    c: DistanceY(g3,g3) = 23
    c: DistanceX(g0,g0) = 1.6
    c: Tangent(g1,g-3)
    c: DistanceY(g0,g-3) = 3.2
FEATURE [Part::Extrusion] Extrude044  label="Extrude scavo saldature alimentatore connettore 5v verticali"
  Base = -> Sketch041
  Dir = (0,-1,2e-16)
  DirMode = 2
  FaceMakerClass = Part::FaceMakerBullseye
  FaceMakerMode = 3
  LengthFwd = 3.2
  LengthRev = 0
  Placement = pos=(0,8.3,0) rot=(0,0,1;0rad)
  Solid = true
  Symmetric = false
FEATURE [Sketcher::SketchObject] Sketch042  label="fermi per driver solenoide e alimentatore"
  ArcFitTolerance = 1e-06
  AttachmentSupport = -> [XZ_Plane]
  ExternalGeometry = -> [Sketch036,Sketch037,Sketch,Sketch038]
  FullyConstrained = true
  MakeInternals = false
  MapMode = 5
  Placement = pos=(0,0,0) rot=(1,0,0;1.5708rad)
  sketch-geometry (27):
    g0: LineSegment StartX=-195.773 StartY=-15.631 StartZ=0 EndX=-196.702 EndY=-17.6249 EndZ=0
    g1: LineSegment StartX=-196.702 StartY=-17.6249 StartZ=0 EndX=-194.709 EndY=-18.5546 EndZ=0
    g2: LineSegment StartX=-194.709 StartY=-18.5546 StartZ=0 EndX=-193.779 EndY=-16.5607 EndZ=0
    g3: LineSegment StartX=-193.779 StartY=-16.5607 StartZ=0 EndX=-195.773 EndY=-15.631 EndZ=0
    g4: LineSegment StartX=-196.547 StartY=-13.5047 StartZ=0 EndX=-198.829 EndY=-18.3988 EndZ=0
    g5: LineSegment StartX=-198.829 StartY=-18.3988 StartZ=0 EndX=-195.385 EndY=-20.0047 EndZ=0
    g6: LineSegment StartX=-193.258 StartY=-19.2308 StartZ=0 EndX=-192.329 EndY=-17.2369 EndZ=0
    g7: LineSegment StartX=-193.103 StartY=-15.1106 StartZ=0 EndX=-196.547 EndY=-13.5047 EndZ=0
    g8: LineSegment [constr] StartX=-193.935 StartY=-20.6809 StartZ=0 EndX=-193.258 EndY=-19.2308 EndZ=0
    g9: LineSegment [constr] StartX=-193.935 StartY=-20.6809 StartZ=0 EndX=-195.385 EndY=-20.0047 EndZ=0
    g10: ArcOfCircle CenterX=-193.779 CenterY=-16.5607 CenterZ=0 NormalX=0 NormalY=0 NormalZ=1 AngleXU=0 Radius=1.6 StartAngle=5.84685 EndAngle=7.41765
    g11: GeomPoint [constr] X=-191.653 Y=-15.7868 Z=0
    g12: ArcOfCircle CenterX=-194.709 CenterY=-18.5546 CenterZ=0 NormalX=0 NormalY=0 NormalZ=1 AngleXU=0 Radius=1.6 StartAngle=4.27606 EndAngle=5.84685
    g13: GeomPoint [constr] X=-193.935 Y=-20.6809 Z=0
    g14: LineSegment StartX=-207.775 StartY=-46.8316 StartZ=0 EndX=-207.775 EndY=-50.8316 EndZ=0
    g15: LineSegment StartX=-207.775 StartY=-46.8316 StartZ=0 EndX=-203.775 EndY=-46.8316 EndZ=0
    g16: LineSegment StartX=-203.775 StartY=-46.8316 StartZ=0 EndX=-203.775 EndY=-50.8316 EndZ=0
    g17: LineSegment StartX=-207.775 StartY=-50.8316 StartZ=0 EndX=-203.775 EndY=-50.8316 EndZ=0
    g18: LineSegment StartX=-209.375 StartY=-52.4316 StartZ=0 EndX=-203.775 EndY=-52.4316 EndZ=0
    g19: LineSegment StartX=-202.175 StartY=-50.8316 StartZ=0 EndX=-202.175 EndY=-46.8316 EndZ=0
    g20: LineSegment StartX=-203.775 StartY=-45.2316 StartZ=0 EndX=-209.375 EndY=-45.2316 EndZ=0
    g21: LineSegment StartX=-209.375 StartY=-45.2316 StartZ=0 EndX=-209.375 EndY=-52.4316 EndZ=0
    g22: ArcOfCircle CenterX=-203.775 CenterY=-46.8316 CenterZ=0 NormalX=0 NormalY=0 NormalZ=1 AngleXU=0 Radius=1.6 StartAngle=1.8e-15 EndAngle=1.5708
    g23: GeomPoint [constr] X=-202.175 Y=-45.2316 Z=0
    g24: ArcOfCircle CenterX=-203.775 CenterY=-50.8316 CenterZ=0 NormalX=0 NormalY=0 NormalZ=1 AngleXU=0 Radius=1.6 StartAngle=4.71239 EndAngle=6.28319
    g25: GeomPoint [constr] X=-202.175 Y=-52.4316 Z=0
    g26: LineSegment [constr] StartX=-207.775 StartY=-50.4316 StartZ=0 EndX=-207.775 EndY=-50.8316 EndZ=0
  constraints (69):
    c: Coincident(g1,g0)
    c: Coincident(g2,g1)
    c: Coincident(g3,g2)
    c: Coincident(g3,g0)
    c: Parallel(g0,g2)
    c: Perpendicular(g3,g0)
    c: Perpendicular(g1,g0)
    c: Coincident(g5,g4)
    c: Coincident(g7,g4)
    c: Distance(g3) = 2.2
    c: Distance(g2) = 2.2
    c: Parallel(g6,g2)
    c: Parallel(g6,g4)
    c: Perpendicular(g5,g6)
    c: Perpendicular(g7,g6)
    c: Distance(g13,g11) = 5.4
    c: Distance(g5,g13) = 5.4
    c: Coincident(g9,g8)
    c: Distance(g8) = 1.6
    c: Distance(g9) = 1.6
    c: Perpendicular(g9,g8)
    c: Parallel(g8,g6)
    c: Coincident(g8,g13)
    c: Distance(g8,g1) = 1.6
    c: Distance(g9,g1) = 1.6
    c: Tangent(g0,g-5)
    c: Distance(g0,g-6) = 26.2
    c: PointOnObject(g11,g7)
    c: PointOnObject(g11,g6)
    c: Tangent(g7,g10) = -1.5708
    c: Tangent(g6,g10) = -1.5708
    c: PointOnObject(g13,g5)
    c: Tangent(g5,g12) = -1.5708
    c: Tangent(g6,g12) = -1.5708
    c: Equal(g10,g12)
    c: Coincident(g10,g2)
    c: Vertical(g14)
    c: Coincident(g15,g14)
    c: Horizontal(g15)
    c: Coincident(g16,g15)
    c: Vertical(g16)
    c: Coincident(g17,g14)
    c: Coincident(g17,g16)
    c: Horizontal(g17)
    c: Distance(g16) = 4
    c: Distance(g15) = 4
    c: Horizontal(g18)
    c: Vertical(g19)
    c: Horizontal(g20)
    c: Coincident(g21,g20)
    c: Coincident(g21,g18)
    c: Vertical(g21)
    c: Distance(g20,g23) = 7.2
    c: Distance(g25,g23) = 7.2
    c: DistanceY(g18,g14) = 1.6
    c: DistanceX(g18,g14) = 1.6
    c: PointOnObject(g23,g20)
    c: PointOnObject(g23,g19)
    c: Tangent(g20,g22) = -1.5708
    c: Tangent(g19,g22) = -1.5708
    c: PointOnObject(g25,g19)
    c: Tangent(g18,g24) = -1.5708
    c: Tangent(g19,g24) = -1.5708
    c: Equal(g22,g24)
    c: Coincident(g22,g15)
    c: Vertical(g26)
    c: Distance(g26) = 0.4
    c: Coincident(g26,g-4)
    c: Coincident(g14,g26)
FEATURE [Part::Extrusion] Extrude045  label="Extrude fermi per driver solenoide e alimentatore"
  Base = -> Sketch042
  Dir = (0,-1,2e-16)
  DirMode = 2
  FaceMakerClass = Part::FaceMakerBullseye
  FaceMakerMode = 3
  LengthFwd = 25.2
  LengthRev = 0
  Solid = true
  Symmetric = true
FEATURE [Sketcher::SketchObject] Sketch043  label="scavo pulizia fermo alimentatore"
  ArcFitTolerance = 1e-06
  AttachmentSupport = -> [XZ_Plane]
  ExternalGeometry = -> [Sketch042,Sketch036,Sketch037]
  FullyConstrained = true
  MakeInternals = false
  MapMode = 5
  Placement = pos=(0,0,0) rot=(1,0,0;1.5708rad)
  sketch-geometry (6):
    g0: LineSegment StartX=-209.375 StartY=-52.4316 StartZ=0 EndX=-209.375 EndY=-50.4316 EndZ=0
    g1: LineSegment StartX=-209.375 StartY=-50.4316 StartZ=0 EndX=-207.775 EndY=-50.4316 EndZ=0
    g2: LineSegment StartX=-207.775 StartY=-50.4316 StartZ=0 EndX=-207.775 EndY=-45.2316 EndZ=0
    g3: LineSegment StartX=-207.775 StartY=-45.2316 StartZ=0 EndX=-202.175 EndY=-45.2316 EndZ=0
    g4: LineSegment StartX=-202.175 StartY=-45.2316 StartZ=0 EndX=-202.175 EndY=-52.4316 EndZ=0
    g5: LineSegment StartX=-202.175 StartY=-52.4316 StartZ=0 EndX=-209.375 EndY=-52.4316 EndZ=0
  constraints (13):
    c: Vertical(g0)
    c: Coincident(g1,g0)
    c: Coincident(g2,g1)
    c: Coincident(g3,g2)
    c: Coincident(g4,g3)
    c: Coincident(g5,g4)
    c: Coincident(g5,g0)
    c: Horizontal(g5)
    c: Coincident(g0,g-6)
    c: Tangent(g1,g-8)
    c: Tangent(g2,g-4)
    c: Tangent(g3,g-7)
    c: Tangent(g4,g-3)
FEATURE [Part::Extrusion] Extrude046  label="Extrude scavo pulizia fermo alimentatore"
  Base = -> Sketch043
  Dir = (0,-1,2e-16)
  DirMode = 2
  FaceMakerClass = Part::FaceMakerBullseye
  FaceMakerMode = 3
  LengthFwd = 19.5
  LengthRev = 0
  Solid = true
  Symmetric = true
FEATURE [Sketcher::SketchObject] Sketch044  label="buchini per fissaggio oled"
  ArcFitTolerance = 1e-06
  AttachmentSupport = -> [YZ_Plane]
  ExternalGeometry = -> [Sketch]
  FullyConstrained = true
  MakeInternals = false
  MapMode = 5
  Placement = pos=(0,0,0) rot=(0.57735,0.57735,0.57735;2.0944rad)
  sketch-geometry (5):
    g0: LineSegment [constr] StartX=1.5e-14 StartY=67.3588 StartZ=0 EndX=0 EndY=64.3588 EndZ=0
    g1: LineSegment [constr] StartX=0 StartY=64.3588 StartZ=0 EndX=10.4 EndY=64.3588 EndZ=0
    g2: LineSegment [constr] StartX=0 StartY=64.3588 StartZ=0 EndX=-10.4 EndY=64.3588 EndZ=0
    g3: Circle CenterX=10.4 CenterY=64.3588 CenterZ=0 NormalX=0 NormalY=0 NormalZ=1 AngleXU=0 Radius=1.5
    g4: Circle CenterX=-10.4 CenterY=64.3588 CenterZ=0 NormalX=0 NormalY=0 NormalZ=1 AngleXU=0 Radius=1.5
  constraints (13):
    c: Distance(g0) = 3
    c: PointOnObject(g0,g-2)
    c: Coincident(g1,g0)
    c: Horizontal(g1)
    c: Coincident(g2,g0)
    c: Horizontal(g2)
    c: DistanceX(g1,g1) = 10.4
    c: Coincident(g3,g1)
    c: Diameter(g4) = 3
    c: Coincident(g4,g2)
    c: Coincident(g0,g-7)
    c: Equal(g1,g2)
    c: Equal(g4,g3)
FEATURE [Part::Extrusion] Extrude047  label="Extrude buchini per fissaggio oled"
  Base = -> Sketch044
  Dir = (1,0,0)
  DirMode = 2
  FaceMakerClass = Part::FaceMakerBullseye
  FaceMakerMode = 3
  LengthFwd = 10
  LengthRev = 0
  Placement = pos=(-186,0,0) rot=(0,0,1;0rad)
  Solid = true
  Symmetric = false
FEATURE [Sketcher::SketchObject] Sketch046  label="scavo 5x5 neopixel"
  ArcFitTolerance = 1e-06
  AttachmentSupport = -> [YZ_Plane002]
  FullyConstrained = true
  MakeInternals = false
  MapMode = 5
  Placement = pos=(0,0,0) rot=(0.57735,0.57735,0.57735;2.0944rad)
  sketch-geometry (4):
    g0: LineSegment StartX=-2.7 StartY=2.7 StartZ=0 EndX=2.7 EndY=2.7 EndZ=0
    g1: LineSegment StartX=2.7 StartY=2.7 StartZ=0 EndX=2.7 EndY=-2.7 EndZ=0
    g2: LineSegment StartX=2.7 StartY=-2.7 StartZ=0 EndX=-2.7 EndY=-2.7 EndZ=0
    g3: LineSegment StartX=-2.7 StartY=-2.7 StartZ=0 EndX=-2.7 EndY=2.7 EndZ=0
  constraints (11):
    c: Horizontal(g0)
    c: Coincident(g1,g0)
    c: Vertical(g1)
    c: Coincident(g2,g1)
    c: Horizontal(g2)
    c: Coincident(g3,g2)
    c: Coincident(g3,g0)
    c: Vertical(g3)
    c: DistanceX(g0,g0) = 5.4
    c: DistanceY(g1,g1) = 5.4
    c: Symmetric(g0,g1,g-1)
FEATURE [Sketcher::SketchObject] Sketch047  label="scavo 10x10 neopixel corpo"
  ArcFitTolerance = 1e-06
  AttachmentOffset = pos=(0,0,1) rot=(0,0,1;0rad)
  AttachmentSupport = -> [YZ_Plane002]
  FullyConstrained = true
  MakeInternals = false
  MapMode = 5
  Placement = pos=(1,0,0) rot=(0.57735,0.57735,0.57735;2.0944rad)
  sketch-geometry (4):
    g0: LineSegment StartX=-5 StartY=5.1 StartZ=0 EndX=5 EndY=5.1 EndZ=0
    g1: LineSegment StartX=5 StartY=5.1 StartZ=0 EndX=5 EndY=-5.1 EndZ=0
    g2: LineSegment StartX=5 StartY=-5.1 StartZ=0 EndX=-5 EndY=-5.1 EndZ=0
    g3: LineSegment StartX=-5 StartY=-5.1 StartZ=0 EndX=-5 EndY=5.1 EndZ=0
  constraints (11):
    c: Horizontal(g0)
    c: Coincident(g1,g0)
    c: Vertical(g1)
    c: Coincident(g2,g1)
    c: Horizontal(g2)
    c: Coincident(g3,g2)
    c: Coincident(g3,g0)
    c: Vertical(g3)
    c: DistanceX(g0,g0) = 10
    c: DistanceY(g1,g1) = 10.2
    c: Symmetric(g0,g2,g-1)
FEATURE [Sketcher::SketchObject] Sketch048  label="buco per perno blocco neopixel"
  ArcFitTolerance = 1e-06
  AttachmentSupport = -> [XZ_Plane002]
  FullyConstrained = true
  MakeInternals = false
  MapMode = 5
  Placement = pos=(0,0,0) rot=(1,0,0;1.5708rad)
  sketch-geometry (4):
    g0: LineSegment StartX=3 StartY=1.2 StartZ=0 EndX=3 EndY=-1.2 EndZ=0
    g1: LineSegment StartX=3 StartY=-1.2 StartZ=0 EndX=5.4 EndY=-1.2 EndZ=0
    g2: LineSegment StartX=5.4 StartY=-1.2 StartZ=0 EndX=5.4 EndY=1.2 EndZ=0
    g3: LineSegment StartX=5.4 StartY=1.2 StartZ=0 EndX=3 EndY=1.2 EndZ=0
  constraints (11):
    c: Coincident(g1,g0)
    c: Horizontal(g1)
    c: Coincident(g2,g1)
    c: Vertical(g2)
    c: Coincident(g3,g2)
    c: Coincident(g3,g0)
    c: Horizontal(g3)
    c: DistanceX(g1,g1) = 2.4
    c: DistanceY(g2,g2) = 2.4
    c: Symmetric(g0,g0,g-1)
    c: DistanceX(g-1,g0) = 3
FEATURE [Sketcher::SketchObject] Sketch045  label="blocco principale per neopixel"
  ArcFitTolerance = 1e-06
  AttachmentSupport = -> [XZ_Plane002]
  ExternalGeometry = -> [Sketch048]
  FullyConstrained = true
  MakeInternals = false
  MapMode = 5
  Placement = pos=(0,0,0) rot=(1,0,0;1.5708rad)
  sketch-geometry (6):
    g0: LineSegment StartX=0 StartY=5.1 StartZ=0 EndX=0 EndY=-5.1 EndZ=0
    g1: LineSegment StartX=0 StartY=-5.1 StartZ=0 EndX=3 EndY=-5.1 EndZ=0
    g2: LineSegment StartX=7 StartY=-1.1 StartZ=0 EndX=7 EndY=5.1 EndZ=0
    g3: LineSegment StartX=7 StartY=5.1 StartZ=0 EndX=0 EndY=5.1 EndZ=0
    g4: ArcOfCircle CenterX=3 CenterY=-1.1 CenterZ=0 NormalX=0 NormalY=0 NormalZ=1 AngleXU=0 Radius=4 StartAngle=4.71239 EndAngle=6.28319
    g5: GeomPoint [constr] X=7 Y=-5.1 Z=0
  constraints (15):
    c: Vertical(g0)
    c: Coincident(g1,g0)
    c: Horizontal(g1)
    c: Vertical(g2)
    c: Coincident(g3,g2)
    c: Coincident(g3,g0)
    c: Horizontal(g3)
    c: DistanceY(g0,g0) = 10.2
    c: Symmetric(g0,g0,g-1)
    c: DistanceX(g3,g3) = 7
    c: PointOnObject(g5,g2)
    c: PointOnObject(g5,g1)
    c: Tangent(g2,g4) = -1.5708
    c: Tangent(g1,g4) = -1.5708
    c: DistanceX(g-3,g1) = 0
FEATURE [Sketcher::SketchObject] Sketch049  label="rinforzi esterni per corpo neopoixel"
  ArcFitTolerance = 1e-06
  AttachmentSupport = -> [XZ_Plane002]
  ExternalGeometry = -> [Sketch045]
  FullyConstrained = true
  MakeInternals = false
  MapMode = 5
  Placement = pos=(0,0,0) rot=(1,0,0;1.5708rad)
  sketch-geometry (8):
    g0: LineSegment StartX=1 StartY=-4.1 StartZ=0 EndX=2 EndY=-4.1 EndZ=0
    g1: LineSegment StartX=2 StartY=-4.1 StartZ=0 EndX=2 EndY=-5.1 EndZ=0
    g2: LineSegment StartX=2 StartY=-5.1 StartZ=0 EndX=1 EndY=-5.1 EndZ=0
    g3: LineSegment StartX=1 StartY=-5.1 StartZ=0 EndX=1 EndY=-4.1 EndZ=0
    g4: LineSegment StartX=1 StartY=5.1 StartZ=0 EndX=2 EndY=5.1 EndZ=0
    g5: LineSegment StartX=2 StartY=5.1 StartZ=0 EndX=2 EndY=4.1 EndZ=0
    g6: LineSegment StartX=2 StartY=4.1 StartZ=0 EndX=1 EndY=4.1 EndZ=0
    g7: LineSegment StartX=1 StartY=4.1 StartZ=0 EndX=1 EndY=5.1 EndZ=0
  constraints (24):
    c: Horizontal(g0)
    c: Coincident(g1,g0)
    c: Vertical(g1)
    c: Coincident(g2,g1)
    c: Horizontal(g2)
    c: Coincident(g3,g2)
    c: Coincident(g3,g0)
    c: Vertical(g3)
    c: Horizontal(g4)
    c: Coincident(g5,g4)
    c: Vertical(g5)
    c: Coincident(g6,g5)
    c: Horizontal(g6)
    c: Coincident(g7,g6)
    c: Coincident(g7,g4)
    c: Vertical(g7)
    c: DistanceX(g4,g4) = 1
    c: DistanceY(g5,g5) = 1
    c: DistanceX(g0,g0) = 1
    c: DistanceY(g1,g1) = 1
    c: DistanceX(g-3,g4) = 1
    c: DistanceY(g-3,g4) = 0
    c: DistanceX(g-4,g2) = 1
    c: DistanceY(g2,g-4) = 0
FEATURE [Sketcher::SketchObject] Sketch052  label="scavo saldature driver solenoide"
  ArcFitTolerance = 1e-06
  AttachmentSupport = -> [XZ_Plane]
  ExternalGeometry = -> [Sketch038]
  FullyConstrained = true
  MakeInternals = false
  MapMode = 5
  Placement = pos=(0,0,0) rot=(1,0,0;1.5708rad)
  sketch-geometry (4):
    g0: LineSegment StartX=-196.56 StartY=-9.74706 StartZ=0 EndX=-198.25 EndY=-13.3723 EndZ=0
    g1: LineSegment StartX=-198.25 StartY=-13.3723 StartZ=0 EndX=-196.8 EndY=-14.0485 EndZ=0
    g2: LineSegment StartX=-196.8 StartY=-14.0485 StartZ=0 EndX=-195.11 EndY=-10.4232 EndZ=0
    g3: LineSegment StartX=-195.11 StartY=-10.4232 StartZ=0 EndX=-196.56 EndY=-9.74706 EndZ=0
  constraints (11):
    c: Coincident(g1,g0)
    c: Coincident(g2,g1)
    c: Coincident(g3,g2)
    c: Coincident(g3,g0)
    c: Parallel(g2,g0)
    c: Perpendicular(g2,g3)
    c: Perpendicular(g1,g2,g1) = 1.5708
    c: Parallel(g2,g-3)
    c: Distance(g2) = 4
    c: Distance(g3) = 1.6
    c: Coincident(g2,g-3)
FEATURE [Part::Extrusion] Extrude055  label="Extrude scavo saldature driver solenoide"
  Base = -> Sketch052
  Dir = (0,-1,2e-16)
  DirMode = 2
  FaceMakerClass = Part::FaceMakerBullseye
  FaceMakerMode = 3
  LengthFwd = 6
  LengthRev = 0
  Solid = true
  Symmetric = true
FEATURE [Sketcher::SketchObject] Sketch053  label="scavo saldature rumble"
  ArcFitTolerance = 1e-06
  AttachmentSupport = -> [XZ_Plane]
  ExternalGeometry = -> [Sketch019]
  FullyConstrained = true
  MakeInternals = false
  MapMode = 5
  Placement = pos=(0,0,0) rot=(1,0,0;1.5708rad)
  sketch-geometry (4):
    g0: LineSegment StartX=-165.31 StartY=-44.1173 StartZ=0 EndX=-166.547 EndY=-47.9216 EndZ=0
    g1: LineSegment StartX=-166.547 StartY=-47.9216 StartZ=0 EndX=-165.405 EndY=-48.2924 EndZ=0
    g2: LineSegment StartX=-165.405 StartY=-48.2924 StartZ=0 EndX=-164.169 EndY=-44.4881 EndZ=0
    g3: LineSegment StartX=-164.169 StartY=-44.4881 StartZ=0 EndX=-165.31 EndY=-44.1173 EndZ=0
  constraints (11):
    c: Coincident(g1,g0)
    c: Coincident(g2,g1)
    c: Coincident(g3,g2)
    c: Coincident(g3,g0)
    c: Parallel(g0,g2)
    c: Perpendicular(g3,g0)
    c: Perpendicular(g1,g0)
    c: Parallel(g0,g-3)
    c: Distance(g0) = 4
    c: Distance(g1) = 1.2
    c: Coincident(g0,g-3)
FEATURE [Part::Extrusion] Extrude056  label="Extrude scavo saldature rumble"
  Base = -> Sketch053
  Dir = (0,-1,2e-16)
  DirMode = 2
  FaceMakerClass = Part::FaceMakerBullseye
  FaceMakerMode = 3
  LengthFwd = 8.4
  LengthRev = 0
  Solid = true
  Symmetric = true
FEATURE [Sketcher::SketchObject] Sketch054  label="scavo saldature alimentatore connettore USB"
  ArcFitTolerance = 1e-06
  AttachmentSupport = -> [XZ_Plane]
  ExternalGeometry = -> [Sketch037]
  FullyConstrained = true
  MakeInternals = false
  MapMode = 5
  Placement = pos=(0,0,0) rot=(1,0,0;1.5708rad)
  sketch-geometry (4):
    g0: LineSegment StartX=-209.575 StartY=-80.4316 StartZ=0 EndX=-210.375 EndY=-80.4316 EndZ=0
    g1: LineSegment StartX=-210.375 StartY=-80.4316 StartZ=0 EndX=-210.375 EndY=-72.4316 EndZ=0
    g2: LineSegment StartX=-210.375 StartY=-72.4316 StartZ=0 EndX=-209.575 EndY=-72.4316 EndZ=0
    g3: LineSegment StartX=-209.575 StartY=-72.4316 StartZ=0 EndX=-209.575 EndY=-80.4316 EndZ=0
  constraints (11):
    c: Horizontal(g0)
    c: Coincident(g1,g0)
    c: Vertical(g1)
    c: Coincident(g2,g1)
    c: Horizontal(g2)
    c: Coincident(g3,g2)
    c: Coincident(g3,g0)
    c: Vertical(g3)
    c: DistanceX(g0,g0) = 0.8
    c: DistanceY(g3,g3) = 8
    c: Coincident(g0,g-4)
FEATURE [Part::Extrusion] Extrude057  label="Extrude scavo saldature alimentatore connettore USB"
  Base = -> Sketch054
  Dir = (0,-1,2e-16)
  DirMode = 2
  FaceMakerClass = Part::FaceMakerBullseye
  FaceMakerMode = 3
  LengthFwd = 11
  LengthRev = 0
  Solid = true
  Symmetric = true
FEATURE [Sketcher::SketchObject] Sketch055  label="buco interno per micro switch"
  ArcFitTolerance = 1e-06
  AttachmentSupport = -> [XZ_Plane]
  ExternalGeometry = -> [Sketch]
  FullyConstrained = true
  MakeInternals = false
  MapMode = 5
  Placement = pos=(0,0,0) rot=(1,0,0;1.5708rad)
  sketch-geometry (11):
    g0: LineSegment [constr] StartX=-194.483 StartY=34.2854 StartZ=0 EndX=-196.022 EndY=30.0568 EndZ=0
    g1: LineSegment [constr] StartX=-196.022 StartY=30.0568 StartZ=0 EndX=-197.561 EndY=25.8282 EndZ=0
    g2: LineSegment [constr] StartX=-196.022 StartY=30.0568 StartZ=0 EndX=-194.143 EndY=29.3727 EndZ=0
    g3: LineSegment [constr] StartX=-196.022 StartY=30.0568 StartZ=0 EndX=-197.902 EndY=30.7408 EndZ=0
    g4: LineSegment StartX=-196.362 StartY=34.9694 StartZ=0 EndX=-192.604 EndY=33.6014 EndZ=0
    g5: LineSegment StartX=-199.441 StartY=26.5122 StartZ=0 EndX=-195.682 EndY=25.1441 EndZ=0
    g6: LineSegment StartX=-192.604 StartY=33.6014 StartZ=0 EndX=-195.682 EndY=25.1441 EndZ=0
    g7: LineSegment StartX=-196.362 StartY=34.9694 StartZ=0 EndX=-199.441 EndY=26.5122 EndZ=0
    g8: GeomPoint [constr] X=-187.821 Y=29.2 Z=0
    g9: LineSegment [constr] StartX=-188.505 StartY=27.3206 StartZ=0 EndX=-196.022 EndY=30.0568 EndZ=0
    g10: LineSegment [constr] StartX=-187.821 StartY=29.2 StartZ=0 EndX=-188.505 EndY=27.3206 EndZ=0
  constraints (27):
    c: Coincident(g2,g0)
    c: Parallel(g0,g-3)
    c: Tangent(g1,g0) = -1.5708
    c: Perpendicular(g0,g2)
    c: Tangent(g2,g3)
    c: Distance(g0,g1) = 9
    c: Equal(g0,g1)
    c: Distance(g3,g2) = 4
    c: Equal(g2,g3)
    c: Parallel(g3,g4)
    c: Symmetric(g4,g4,g0)
    c: Parallel(g6,g1)
    c: Parallel(g7,g1)
    c: Symmetric(g6,g6,g2)
    c: Symmetric(g5,g5,g1)
    c: Symmetric(g7,g7,g3)
    c: Coincident(g7,g4)
    c: Coincident(g6,g4)
    c: Coincident(g5,g6)
    c: Symmetric(g-3,g-3,g8)
    c: Perpendicular(g-3,g9)
    c: Distance(g9) = 8
    c: Coincident(g3,g9)
    c: Coincident(g10,g8)
    c: Parallel(g10,g-3)
    c: Distance(g10) = 2
    c: Coincident(g10,g9)
FEATURE [Sketcher::SketchObject] Sketch056  label="buco esterno per micro switch"
  ArcFitTolerance = 1e-06
  AttachmentSupport = -> [XZ_Plane]
  ExternalGeometry = -> [Sketch055]
  FullyConstrained = true
  MakeInternals = false
  MapMode = 5
  Placement = pos=(0,0,0) rot=(1,0,0;1.5708rad)
  sketch-geometry (17):
    g0: GeomPoint [constr] X=-194.143 Y=29.3727 Z=0
    g1: GeomPoint [constr] X=-194.483 Y=34.2854 Z=0
    g2: GeomPoint [constr] X=-197.902 Y=30.7408 Z=0
    g3: GeomPoint [constr] X=-197.561 Y=25.8282 Z=0
    g4: GeomPoint [constr] X=-196.022 Y=30.0568 Z=0
    g5: LineSegment [constr] StartX=-194.483 StartY=34.2854 StartZ=0 EndX=-196.022 EndY=30.0568 EndZ=0
    g6: LineSegment [constr] StartX=-196.022 StartY=30.0568 StartZ=0 EndX=-197.561 EndY=25.8282 EndZ=0
    g7: LineSegment [constr] StartX=-197.902 StartY=30.7408 StartZ=0 EndX=-196.022 EndY=30.0568 EndZ=0
    g8: LineSegment [constr] StartX=-196.022 StartY=30.0568 StartZ=0 EndX=-194.143 EndY=29.3727 EndZ=0
    g9: LineSegment [constr] StartX=-195.338 StartY=31.9362 StartZ=0 EndX=-196.022 EndY=30.0568 EndZ=0
    g10: LineSegment [constr] StartX=-196.022 StartY=30.0568 StartZ=0 EndX=-196.706 EndY=28.1774 EndZ=0
    g11: LineSegment [constr] StartX=-196.022 StartY=30.0568 StartZ=0 EndX=-196.821 EndY=30.3475 EndZ=0
    g12: LineSegment [constr] StartX=-196.022 StartY=30.0568 StartZ=0 EndX=-195.223 EndY=29.7661 EndZ=0
    g13: LineSegment StartX=-194.539 StartY=31.6454 StartZ=0 EndX=-195.907 EndY=27.8867 EndZ=0
    g14: LineSegment StartX=-196.137 StartY=32.2269 StartZ=0 EndX=-197.505 EndY=28.4681 EndZ=0
    g15: LineSegment StartX=-196.137 StartY=32.2269 StartZ=0 EndX=-194.539 EndY=31.6454 EndZ=0
    g16: LineSegment StartX=-197.505 StartY=28.4681 StartZ=0 EndX=-195.907 EndY=27.8867 EndZ=0
  constraints (34):
    c: Symmetric(g-5,g-5,g1)
    c: Symmetric(g-5,g-6,g0)
    c: Symmetric(g-6,g-6,g3)
    c: Symmetric(g-5,g-6,g2)
    c: Coincident(g5,g1)
    c: Coincident(g5,g4)
    c: Coincident(g6,g4)
    c: Coincident(g6,g3)
    c: Equal(g5,g6)
    c: Coincident(g7,g2)
    c: Coincident(g7,g4)
    c: Coincident(g8,g4)
    c: Coincident(g8,g0)
    c: Equal(g7,g8)
    c: Coincident(g11,g9)
    c: Coincident(g12,g9)
    c: Tangent(g10,g9) = -1.5708
    c: Perpendicular(g11,g9)
    c: Parallel(g9,g-4)
    c: Equal(g9,g10)
    c: Parallel(g12,g11)
    c: Equal(g11,g12)
    c: Distance(g11,g12) = 1.7
    c: Distance(g9,g10) = 4
    c: Symmetric(g13,g13,g12)
    c: Parallel(g13,g9)
    c: Symmetric(g14,g14,g11)
    c: Symmetric(g15,g15,g9)
    c: Parallel(g15,g11)
    c: Symmetric(g16,g16,g10)
    c: Coincident(g16,g14)
    c: Coincident(g15,g14)
    c: Coincident(g13,g15)
    c: Coincident(g9,g4)
FEATURE [Sketcher::SketchObject] Sketch057  label="buco interno per SWITCH"
  ArcFitTolerance = 1e-06
  AttachmentSupport = -> [XZ_Plane]
  ExternalGeometry = -> [Sketch]
  FullyConstrained = true
  MakeInternals = false
  MapMode = 5
  Placement = pos=(0,0,0) rot=(1,0,0;1.5708rad)
  sketch-geometry (10):
    g0: GeomPoint [constr] X=-187.821 Y=29.2 Z=0
    g1: LineSegment [constr] StartX=-188.505 StartY=27.3206 StartZ=0 EndX=-193.203 EndY=29.0307 EndZ=0
    g2: LineSegment [constr] StartX=-190.809 StartY=35.6086 StartZ=0 EndX=-195.597 EndY=22.4529 EndZ=0
    g3: GeomPoint [constr] X=-193.203 Y=29.0307 Z=0
    g4: LineSegment [constr] StartX=-196.492 StartY=30.2278 StartZ=0 EndX=-189.914 EndY=27.8336 EndZ=0
    g5: LineSegment StartX=-194.098 StartY=36.8056 StartZ=0 EndX=-187.52 EndY=34.4115 EndZ=0
    g6: LineSegment StartX=-194.098 StartY=36.8056 StartZ=0 EndX=-198.886 EndY=23.6499 EndZ=0
    g7: LineSegment StartX=-187.52 StartY=34.4115 StartZ=0 EndX=-192.308 EndY=21.2558 EndZ=0
    g8: LineSegment StartX=-198.886 StartY=23.6499 StartZ=0 EndX=-192.308 EndY=21.2558 EndZ=0
    g9: LineSegment [constr] StartX=-187.821 StartY=29.2 StartZ=0 EndX=-188.505 EndY=27.3206 EndZ=0
  constraints (23):
    c: Symmetric(g-3,g-3,g0)
    c: Perpendicular(g1,g-3)
    c: Parallel(g2,g-3)
    c: Symmetric(g2,g2,g3)
    c: Perpendicular(g2,g4)
    c: Symmetric(g4,g4,g3)
    c: Distance(g2) = 14
    c: Distance(g4) = 7
    c: Distance(g1) = 5
    c: Parallel(g5,g4)
    c: Parallel(g7,g2)
    c: Symmetric(g5,g5,g2)
    c: Symmetric(g6,g6,g4)
    c: Symmetric(g7,g7,g4)
    c: Symmetric(g8,g8,g2)
    c: Coincident(g6,g5)
    c: Coincident(g7,g5)
    c: Coincident(g8,g7)
    c: Coincident(g3,g1)
    c: Coincident(g9,g0)
    c: Parallel(g9,g-3)
    c: Distance(g9) = 2
    c: Coincident(g1,g9)
FEATURE [Sketcher::SketchObject] Sketch058  label="buco esterno per SWITCH"
  ArcFitTolerance = 1e-06
  AttachmentSupport = -> [XZ_Plane]
  ExternalGeometry = -> [Sketch057]
  FullyConstrained = true
  MakeInternals = false
  MapMode = 5
  Placement = pos=(0,0,0) rot=(1,0,0;1.5708rad)
  sketch-geometry (12):
    g0: GeomPoint [constr] X=-190.809 Y=35.6086 Z=0
    g1: GeomPoint [constr] X=-196.492 Y=30.2278 Z=0
    g2: GeomPoint [constr] X=-189.914 Y=27.8336 Z=0
    g3: GeomPoint [constr] X=-195.597 Y=22.4529 Z=0
    g4: GeomPoint [constr] X=-193.203 Y=29.0307 Z=0
    g5: LineSegment [constr] StartX=-192.006 StartY=32.3196 StartZ=0 EndX=-194.4 EndY=25.7418 EndZ=0
    g6: GeomPoint [constr] X=-193.203 Y=29.0307 Z=0
    g7: LineSegment [constr] StartX=-195.082 StartY=29.7148 StartZ=0 EndX=-191.324 EndY=28.3467 EndZ=0
    g8: LineSegment StartX=-193.885 StartY=33.0037 StartZ=0 EndX=-190.127 EndY=31.6356 EndZ=0
    g9: LineSegment StartX=-190.127 StartY=31.6356 StartZ=0 EndX=-192.521 EndY=25.0578 EndZ=0
    g10: LineSegment StartX=-196.28 StartY=26.4258 StartZ=0 EndX=-192.521 EndY=25.0578 EndZ=0
    g11: LineSegment StartX=-193.885 StartY=33.0037 StartZ=0 EndX=-196.28 EndY=26.4258 EndZ=0
  constraints (21):
    c: Symmetric(g-6,g-6,g3)
    c: Symmetric(g-4,g-6,g2)
    c: Symmetric(g-5,g-4,g0)
    c: Symmetric(g-5,g-6,g1)
    c: Symmetric(g1,g2,g4)
    c: Parallel(g5,g-4)
    c: Symmetric(g5,g5,g6)
    c: Perpendicular(g7,g5)
    c: Symmetric(g7,g7,g6)
    c: Distance(g5) = 7
    c: Distance(g7) = 4
    c: Parallel(g8,g7)
    c: Parallel(g11,g5)
    c: Symmetric(g8,g8,g5)
    c: Symmetric(g9,g9,g7)
    c: Symmetric(g10,g10,g5)
    c: Symmetric(g11,g11,g7)
    c: Coincident(g11,g8)
    c: Coincident(g9,g8)
    c: Coincident(g9,g10)
    c: Coincident(g6,g4)
FEATURE [Part::Extrusion] Extrude060  label="Extrude buco interno per SWITCH destro"
  Base = -> Sketch057
  Dir = (0,-1,2e-16)
  DirMode = 2
  FaceMakerClass = Part::FaceMakerBullseye
  FaceMakerMode = 3
  LengthFwd = 13.2
  LengthRev = 0
  Placement = pos=(0,2.6,0) rot=(0,0,1;0rad)
  Solid = true
  Symmetric = false
FEATURE [Part::Extrusion] Extrude061  label="Extrude buco esterno per SWITCH destro"
  Base = -> Sketch058
  Dir = (0,-1,2e-16)
  DirMode = 2
  FaceMakerClass = Part::FaceMakerBullseye
  FaceMakerMode = 3
  LengthFwd = 2
  LengthRev = 0
  Placement = pos=(0,-10.6,0) rot=(0,0,1;0rad)
  Solid = true
  Symmetric = false
FEATURE [Sketcher::SketchObject] Sketch059  label="buco per spazio introduzione SWITCH"
  ArcFitTolerance = 1e-06
  AttachmentSupport = -> [XZ_Plane]
  ExternalGeometry = -> [Sketch057,Sketch010]
  FullyConstrained = true
  MakeInternals = false
  MapMode = 5
  Placement = pos=(0,0,0) rot=(1,0,0;1.5708rad)
  sketch-geometry (8):
    g0: LineSegment [constr] StartX=-201.368 StartY=36.3521 StartZ=0 EndX=-195.094 EndY=34.0687 EndZ=0
    g1: LineSegment [constr] StartX=-194.098 StartY=36.8056 StartZ=0 EndX=-195.094 EndY=34.0687 EndZ=0
    g2: LineSegment StartX=-198.658 StartY=24.2771 StartZ=0 EndX=-199.654 EndY=21.5401 EndZ=0
    g3: LineSegment StartX=-199.654 StartY=21.5401 StartZ=0 EndX=-181.196 EndY=14.822 EndZ=0
    g4: LineSegment StartX=-181.196 StartY=14.822 StartZ=0 EndX=-180.2 EndY=17.559 EndZ=0
    g5: LineSegment StartX=-180.2 StartY=17.559 StartZ=0 EndX=-198.658 EndY=24.2771 EndZ=0
    g6: LineSegment [constr] StartX=-204.932 StartY=26.5605 StartZ=0 EndX=-198.658 EndY=24.2771 EndZ=0
    g7: LineSegment [constr] StartX=-198.658 StartY=24.2771 StartZ=0 EndX=-199.654 EndY=21.5401 EndZ=0
  constraints (20):
    c: Parallel(g1,g-3)
    c: Parallel(g0,g-4)
    c: Coincident(g0,g-4)
    c: Coincident(g1,g-3)
    c: Coincident(g0,g1)
    c: Coincident(g3,g2)
    c: Coincident(g4,g3)
    c: Coincident(g5,g4)
    c: Coincident(g5,g2)
    c: Parallel(g5,g-5)
    c: Parallel(g3,g-5)
    c: Parallel(g4,g-6)
    c: DistanceX(g-6,g4) = 0
    c: Coincident(g6,g-5)
    c: Equal(g6,g0)
    c: Coincident(g7,g6)
    c: Equal(g7,g1)
    c: Tangent(g7,g-3)
    c: Coincident(g2,g6)
    c: Coincident(g2,g7)
FEATURE [Part::Extrusion] Extrude062  label="Extrude buco per spazio introduzione SWITCH"
  Base = -> Sketch059
  Dir = (0,-1,2e-16)
  DirMode = 2
  FaceMakerClass = Part::FaceMakerBullseye
  FaceMakerMode = 3
  LengthFwd = 13.2
  LengthRev = 0
  Solid = true
  Symmetric = true
FEATURE [Part::Extrusion] Extrude063  label="Extrude buco interno per SWITCH sinistro"
  Base = -> Sketch057
  Dir = (0,-1,2e-16)
  DirMode = 2
  FaceMakerClass = Part::FaceMakerBullseye
  FaceMakerMode = 3
  LengthFwd = 13.2
  LengthRev = 0
  Placement = pos=(0,10.6,0) rot=(0,0,1;0rad)
  Solid = true
  Symmetric = false
FEATURE [Part::Extrusion] Extrude064  label="Extrude buco esterno per SWITCH sinistro"
  Base = -> Sketch058
  Dir = (0,-1,2e-16)
  DirMode = 2
  FaceMakerClass = Part::FaceMakerBullseye
  FaceMakerMode = 3
  LengthFwd = 2
  LengthRev = 0
  Placement = pos=(0,12.6,0) rot=(0,0,1;0rad)
  Solid = true
  Symmetric = false
FEATURE [Sketcher::SketchObject] Sketch061  label="struttura esterna blocco switch"
  ArcFitTolerance = 1e-06
  AttachmentSupport = -> [XZ_Plane003]
  FullyConstrained = true
  MakeInternals = false
  MapMode = 5
  Placement = pos=(0,0,0) rot=(1,0,0;1.5708rad)
  sketch-geometry (5):
    g0: LineSegment StartX=-1 StartY=-5.1 StartZ=0 EndX=1 EndY=-5.1 EndZ=0
    g1: LineSegment StartX=1 StartY=-5.1 StartZ=0 EndX=1 EndY=5.1 EndZ=0
    g2: LineSegment StartX=1 StartY=5.1 StartZ=0 EndX=-1 EndY=5.1 EndZ=0
    g3: LineSegment StartX=-1 StartY=5.1 StartZ=0 EndX=-1 EndY=-5.1 EndZ=0
    g4: GeomPoint [constr] X=0 Y=0 Z=0
  constraints (12):
    c: Coincident(g0,g1)
    c: Coincident(g1,g2)
    c: Coincident(g2,g3)
    c: Coincident(g3,g0)
    c: Horizontal(g0)
    c: Horizontal(g2)
    c: Vertical(g1)
    c: Vertical(g3)
    c: Symmetric(g2,g0,g4)
    c: Distance(g1,g3) = 2
    c: Distance(g0,g2) = 10.2
    c: Coincident(g4,g-1)
FEATURE [Sketcher::SketchObject] Sketch062  label="struttura interna blocco switch"
  ArcFitTolerance = 1e-06
  AttachmentSupport = -> [XZ_Plane003]
  ExternalGeometry = -> [Sketch061]
  FullyConstrained = true
  MakeInternals = false
  MapMode = 5
  Placement = pos=(0,0,0) rot=(1,0,0;1.5708rad)
  sketch-geometry (5):
    g0: LineSegment StartX=-1 StartY=3.1 StartZ=0 EndX=-1 EndY=-3.1 EndZ=0
    g1: LineSegment StartX=-1 StartY=-3.1 StartZ=0 EndX=1 EndY=-3.1 EndZ=0
    g2: LineSegment StartX=1 StartY=-3.1 StartZ=0 EndX=1 EndY=3.1 EndZ=0
    g3: LineSegment StartX=1 StartY=3.1 StartZ=0 EndX=-1 EndY=3.1 EndZ=0
    g4: GeomPoint [constr] X=0 Y=0 Z=0
  constraints (12):
    c: Coincident(g0,g1)
    c: Coincident(g1,g2)
    c: Coincident(g2,g3)
    c: Coincident(g3,g0)
    c: Vertical(g0)
    c: Vertical(g2)
    c: Horizontal(g1)
    c: Horizontal(g3)
    c: Symmetric(g2,g0,g4)
    c: Coincident(g4,g-1)
    c: Distance(g0) = 6.2
    c: Equal(g3,g-3)
FEATURE [Sketcher::SketchObject] Sketch063  label="blocchi tra switch"
  ArcFitTolerance = 1e-06
  AttachmentSupport = -> [XZ_Plane003]
  ExternalGeometry = -> [Sketch061,Sketch062]
  FullyConstrained = true
  MakeInternals = false
  MapMode = 5
  Placement = pos=(0,0,0) rot=(1,0,0;1.5708rad)
  sketch-geometry (8):
    g0: LineSegment StartX=-3 StartY=5.1 StartZ=0 EndX=-1 EndY=5.1 EndZ=0
    g1: LineSegment StartX=-1 StartY=5.1 StartZ=0 EndX=-1 EndY=3.1 EndZ=0
    g2: LineSegment StartX=-1 StartY=3.1 StartZ=0 EndX=-3 EndY=3.1 EndZ=0
    g3: LineSegment StartX=-3 StartY=3.1 StartZ=0 EndX=-3 EndY=5.1 EndZ=0
    g4: LineSegment StartX=-3 StartY=-3.1 StartZ=0 EndX=-1 EndY=-3.1 EndZ=0
    g5: LineSegment StartX=-1 StartY=-3.1 StartZ=0 EndX=-1 EndY=-5.1 EndZ=0
    g6: LineSegment StartX=-1 StartY=-5.1 StartZ=0 EndX=-3 EndY=-5.1 EndZ=0
    g7: LineSegment StartX=-3 StartY=-5.1 StartZ=0 EndX=-3 EndY=-3.1 EndZ=0
  constraints (20):
    c: Horizontal(g0)
    c: Coincident(g1,g0)
    c: Coincident(g2,g1)
    c: Horizontal(g2)
    c: Coincident(g3,g2)
    c: Coincident(g3,g0)
    c: Vertical(g3)
    c: Horizontal(g4)
    c: Coincident(g5,g4)
    c: Coincident(g6,g5)
    c: Horizontal(g6)
    c: Coincident(g7,g6)
    c: Coincident(g7,g4)
    c: Vertical(g7)
    c: Coincident(g0,g-4)
    c: Coincident(g1,g-5)
    c: Coincident(g4,g-6)
    c: Coincident(g5,g-7)
    c: Distance(g0) = 2
    c: Distance(g4) = 2
FEATURE [Sketcher::SketchObject] Sketch066  label="piano per rampino"
  ArcFitTolerance = 1e-06
  AttachmentSupport = -> [XZ_Plane002]
  ExternalGeometry = -> [Sketch045]
  FullyConstrained = true
  MakeInternals = false
  MapMode = 5
  Placement = pos=(0,0,0) rot=(1,0,0;1.5708rad)
  sketch-geometry (4):
    g0: LineSegment StartX=5.4 StartY=5.1 StartZ=0 EndX=5.4 EndY=3.9 EndZ=0
    g1: LineSegment StartX=5.4 StartY=3.9 StartZ=0 EndX=7 EndY=3.9 EndZ=0
    g2: LineSegment StartX=7 StartY=3.9 StartZ=0 EndX=7 EndY=5.1 EndZ=0
    g3: LineSegment StartX=7 StartY=5.1 StartZ=0 EndX=5.4 EndY=5.1 EndZ=0
  constraints (11):
    c: Coincident(g0,g1)
    c: Coincident(g1,g2)
    c: Coincident(g2,g3)
    c: Coincident(g3,g0)
    c: Vertical(g0)
    c: Vertical(g2)
    c: Horizontal(g1)
    c: Horizontal(g3)
    c: Distance(g0,g2) = 1.6
    c: Distance(g1,g3) = 1.2
    c: Coincident(g2,g-3)
FEATURE [Sketcher::SketchObject] Sketch064  label="rampini_per_serraggio_struttura"
  ArcFitTolerance = 1e-06
  AttachmentSupport = -> [XZ_Plane002]
  ExternalGeometry = -> [Sketch066,Sketch045]
  FullyConstrained = true
  MakeInternals = false
  MapMode = 5
  Placement = pos=(0,0,0) rot=(1,0,0;1.5708rad)
  sketch-geometry (7):
    g0: LineSegment StartX=7 StartY=5.1 StartZ=0 EndX=7 EndY=3.9 EndZ=0
    g1: LineSegment StartX=7 StartY=3.9 StartZ=0 EndX=9 EndY=3.9 EndZ=0
    g2: LineSegment StartX=7 StartY=5.1 StartZ=0 EndX=7 EndY=5.1 EndZ=0
    g3: LineSegment StartX=7 StartY=5.1 StartZ=0 EndX=7 EndY=7.5 EndZ=0
    g4: LineSegment StartX=9 StartY=5.1 StartZ=0 EndX=9 EndY=3.9 EndZ=0
    g5: LineSegment StartX=7 StartY=7.5 StartZ=0 EndX=9 EndY=7.5 EndZ=0
    g6: LineSegment StartX=9 StartY=7.5 StartZ=0 EndX=9 EndY=5.1 EndZ=0
  constraints (20):
    c: Vertical(g0)
    c: Coincident(g1,g0)
    c: Horizontal(g1)
    c: Coincident(g2,g0)
    c: Horizontal(g2)
    c: Coincident(g3,g2)
    c: Vertical(g3)
    c: Coincident(g5,g3)
    c: Coincident(g4,g6)
    c: Coincident(g4,g1)
    c: Vertical(g4)
    c: Coincident(g0,g-3)
    c: DistanceY(g-4,g3) = 2.4
    c: DistanceX(g1,g1) = 2
    c: DistanceY(g2,g6) = 0
    c: DistanceX(g2,g2) = 0
    c: DistanceY(g0,g0) = 1.2
    c: Coincident(g5,g6)
    c: Horizontal(g5)
    c: Vertical(g6)
FEATURE [Sketcher::SketchObject] Sketch067  label="perno per blocco switch"
  ArcFitTolerance = 1e-06
  AttachmentSupport = -> [XZ_Plane]
  ExternalGeometry = -> [Sketch,Sketch010]
  FullyConstrained = true
  MakeInternals = false
  MapMode = 5
  Placement = pos=(0,0,0) rot=(1,0,0;1.5708rad)
  sketch-geometry (14):
    g0: LineSegment StartX=-191.073 StartY=24.9429 StartZ=0 EndX=-185.81 EndY=23.0276 EndZ=0
    g1: LineSegment StartX=-183.76 StartY=23.9839 StartZ=0 EndX=-182.392 EndY=27.7427 EndZ=0
    g2: LineSegment StartX=-183.348 StartY=29.7934 StartZ=0 EndX=-188.61 EndY=31.7087 EndZ=0
    g3: LineSegment StartX=-188.61 StartY=31.7087 StartZ=0 EndX=-191.073 EndY=24.9429 EndZ=0
    g4: GeomPoint [constr] X=-186.459 Y=27.0946 Z=0
    g5: LineSegment StartX=-189.022 StartY=25.8992 StartZ=0 EndX=-185.263 EndY=24.5311 EndZ=0
    g6: LineSegment StartX=-185.263 StartY=24.5311 StartZ=0 EndX=-183.895 EndY=28.2899 EndZ=0
    g7: LineSegment StartX=-183.895 StartY=28.2899 StartZ=0 EndX=-187.654 EndY=29.658 EndZ=0
    g8: LineSegment StartX=-187.654 StartY=29.658 StartZ=0 EndX=-189.022 EndY=25.8992 EndZ=0
    g9: GeomPoint [constr] X=-186.459 Y=27.0946 Z=0
    g10: ArcOfCircle CenterX=-185.263 CenterY=24.5311 CenterZ=0 NormalX=0 NormalY=0 NormalZ=1 AngleXU=0 Radius=1.6 StartAngle=4.36332 EndAngle=5.93412
    g11: GeomPoint [constr] X=-184.307 Y=22.4804 Z=0
    g12: ArcOfCircle CenterX=-183.895 CenterY=28.2899 CenterZ=0 NormalX=0 NormalY=0 NormalZ=1 AngleXU=0 Radius=1.6 StartAngle=5.93412 EndAngle=7.50492
    g13: GeomPoint [constr] X=-181.844 Y=29.2462 Z=0
  constraints (30):
    c: Coincident(g2,g3)
    c: Coincident(g3,g0)
    c: Symmetric(g13,g0,g4)
    c: Distance(g11,g3) = 7.2
    c: Distance(g0,g2) = 7.2
    c: Parallel(g3,g1)
    c: Parallel(g2,g0)
    c: Perpendicular(g2,g3)
    c: Coincident(g5,g6)
    c: Coincident(g6,g7)
    c: Coincident(g7,g8)
    c: Coincident(g8,g5)
    c: Symmetric(g7,g5,g9)
    c: Distance(g6,g8) = 4
    c: Distance(g5,g7) = 4
    c: Coincident(g9,g4)
    c: Parallel(g8,g6)
    c: Parallel(g7,g5)
    c: Perpendicular(g7,g8)
    c: Tangent(g8,g-3)
    c: Tangent(g2,g-4)
    c: PointOnObject(g11,g1)
    c: PointOnObject(g11,g0)
    c: Tangent(g1,g10) = -1.5708
    c: Tangent(g0,g10) = -1.5708
    c: PointOnObject(g13,g1)
    c: Tangent(g1,g12) = -1.5708
    c: Tangent(g2,g12) = -1.5708
    c: Equal(g10,g12)
    c: Coincident(g10,g5)
FEATURE [Part::Extrusion] Extrude072  label="Extrude perno per blocco switch"
  Base = -> Sketch067
  Dir = (0,-1,2e-16)
  DirMode = 2
  FaceMakerClass = Part::FaceMakerBullseye
  FaceMakerMode = 3
  LengthFwd = 25.2
  LengthRev = 0
  Solid = true
  Symmetric = true
FEATURE [Part::MultiFuse] Fusion
  Refine = true
  Shapes = -> [Extrude,Sweep,Extrude007,Extrude011,Extrude005,Extrude012,Extrude013,Extrude016,Extrude031,Extrude039,Extrude045,Extrude072]
FEATURE [Part::Cut] Cut
  Base = -> Fusion
  Refine = true
  Tool = -> Extrude001
FEATURE [Part::Cut] Cut001
  Base = -> Cut
  Refine = true
  Tool = -> Extrude004
FEATURE [Part::Cut] Cut002
  Base = -> Cut001
  Refine = true
  Tool = -> Extrude006
FEATURE [Part::Cut] Cut003
  Base = -> Cut002
  Refine = true
  Tool = -> Extrude008
FEATURE [Part::Cut] Cut004
  Base = -> Cut003
  Refine = true
  Tool = -> Extrude009
FEATURE [Part::Cut] Cut005
  Base = -> Cut004
  Refine = true
  Tool = -> Extrude010
FEATURE [Part::Cut] Cut006
  Base = -> Cut005
  Refine = true
  Tool = -> Extrude014
FEATURE [Part::Cut] Cut007
  Base = -> Cut006
  Refine = true
  Tool = -> Extrude015
FEATURE [Part::Cut] Cut008
  Base = -> Cut007
  Refine = true
  Tool = -> Extrude018
FEATURE [Part::Cut] Cut009
  Base = -> Cut008
  Refine = true
  Tool = -> Extrude019
FEATURE [Part::Cut] Cut010
  Base = -> Cut009
  Refine = true
  Tool = -> Extrude020
FEATURE [Part::Cut] Cut011
  Base = -> Cut010
  Refine = true
  Tool = -> Extrude021
FEATURE [Part::Cut] Cut012
  Base = -> Cut011
  Refine = true
  Tool = -> Extrude022
FEATURE [Part::Cut] Cut013
  Base = -> Cut012
  Refine = true
  Tool = -> Extrude023
FEATURE [Part::Cut] Cut014
  Base = -> Cut013
  Refine = true
  Tool = -> Extrude032
FEATURE [Part::Cut] Cut015
  Base = -> Cut014
  Refine = true
  Tool = -> Extrude033
FEATURE [Part::Cut] Cut016
  Base = -> Cut015
  Refine = true
  Tool = -> Extrude034
FEATURE [Part::Cut] Cut017
  Base = -> Cut016
  Refine = true
  Tool = -> Extrude035
FEATURE [Part::Cut] Cut018
  Base = -> Cut017
  Refine = true
  Tool = -> Extrude036
FEATURE [Part::Cut] Cut019
  Base = -> Cut018
  Refine = true
  Tool = -> Extrude037
FEATURE [Part::Cut] Cut020
  Base = -> Cut019
  Refine = true
  Tool = -> Extrude030
FEATURE [Part::Cut] Cut022
  Base = -> Cut020
  Refine = true
  Tool = -> Extrude038
FEATURE [Part::Cut] Cut023
  Base = -> Cut022
  Refine = true
  Tool = -> Extrude041
FEATURE [Part::Cut] Cut024
  Base = -> Cut023
  Refine = true
  Tool = -> Extrude040
FEATURE [Part::Cut] Cut025
  Base = -> Cut024
  Refine = true
  Tool = -> Extrude042
FEATURE [Part::Cut] Cut026
  Base = -> Cut025
  Refine = true
  Tool = -> Extrude043
FEATURE [Part::Cut] Cut027
  Base = -> Cut026
  Refine = true
  Tool = -> Extrude044
FEATURE [Part::Cut] Cut028
  Base = -> Cut027
  Refine = true
  Tool = -> Extrude046
FEATURE [Part::Cut] Cut029
  Base = -> Cut028
  Refine = true
  Tool = -> Extrude047
FEATURE [Part::Cut] Cut033
  Base = -> Cut029
  Refine = true
  Tool = -> Extrude055
FEATURE [Part::Cut] Cut034
  Base = -> Cut033
  Refine = true
  Tool = -> Extrude056
FEATURE [Part::Cut] Cut035
  Base = -> Cut034
  Refine = true
  Tool = -> Extrude057
FEATURE [Part::Cut] Cut037
  Base = -> Cut035
  Refine = true
  Tool = -> Extrude060
FEATURE [Part::Cut] Cut038
  Base = -> Cut037
  Refine = true
  Tool = -> Extrude061
FEATURE [Part::Cut] Cut039
  Base = -> Cut038
  Refine = true
  Tool = -> Extrude063
FEATURE [Part::Cut] Cut040
  Base = -> Cut039
  Refine = true
  Tool = -> Extrude064
FEATURE [Part::Cut] Cut041
  Base = -> Cut040
  Refine = true
  Tool = -> Extrude062
FEATURE [Sketcher::SketchObject] Sketch068  label="base con smusso sopra neopixel"
  ArcFitTolerance = 1e-06
  AttachmentSupport = -> [YZ_Plane002]
  FullyConstrained = true
  MakeInternals = false
  MapMode = 5
  Placement = pos=(0,0,0) rot=(0.57735,0.57735,0.57735;2.0944rad)
  sketch-geometry (5):
    g0: LineSegment StartX=-9.5 StartY=-6.1 StartZ=0 EndX=9.5 EndY=-6.1 EndZ=0
    g1: LineSegment StartX=9.5 StartY=-6.1 StartZ=0 EndX=9.5 EndY=6.1 EndZ=0
    g2: LineSegment StartX=9.5 StartY=6.1 StartZ=0 EndX=-9.5 EndY=6.1 EndZ=0
    g3: LineSegment StartX=-9.5 StartY=6.1 StartZ=0 EndX=-9.5 EndY=-6.1 EndZ=0
    g4: GeomPoint [constr] X=0 Y=0 Z=0
  constraints (12):
    c: Coincident(g0,g1)
    c: Coincident(g1,g2)
    c: Coincident(g2,g3)
    c: Coincident(g3,g0)
    c: Horizontal(g0)
    c: Horizontal(g2)
    c: Vertical(g1)
    c: Vertical(g3)
    c: Symmetric(g2,g0,g4)
    c: Distance(g1,g3) = 19
    c: Distance(g0,g2) = 12.2
    c: Coincident(g4,g-1)
FEATURE [Sketcher::SketchObject] Sketch069  label="cilindro minore"
  ArcFitTolerance = 1e-06
  AttachmentSupport = -> [XZ_Plane004]
  FullyConstrained = true
  MakeInternals = false
  MapMode = 5
  Placement = pos=(0,0,0) rot=(1,0,0;1.5708rad)
  sketch-geometry (1):
    g0: Circle CenterX=0 CenterY=0 CenterZ=0 NormalX=0 NormalY=0 NormalZ=1 AngleXU=0 Radius=5.8
  constraints (2):
    c: Diameter(g0) = 11.6
    c: Coincident(g0,g-1)
FEATURE [Sketcher::SketchObject] Sketch070  label="cilindro maggiore"
  ArcFitTolerance = 1e-06
  AttachmentSupport = -> [XZ_Plane004]
  ExternalGeometry = -> [Sketch069]
  FullyConstrained = true
  MakeInternals = false
  MapMode = 5
  Placement = pos=(0,0,0) rot=(1,0,0;1.5708rad)
  sketch-geometry (1):
    g0: Circle CenterX=0 CenterY=0 CenterZ=0 NormalX=0 NormalY=0 NormalZ=1 AngleXU=0 Radius=6.5
  constraints (2):
    c: Coincident(g0,g-1)
    c: Diameter(g0) = 13
FEATURE [Sketcher::SketchObject] Sketch071  label="buco interno"
  ArcFitTolerance = 1e-06
  AttachmentSupport = -> [XZ_Plane004]
  ExternalGeometry = -> [Sketch069]
  FullyConstrained = true
  MakeInternals = false
  MapMode = 5
  Placement = pos=(0,0,0) rot=(1,0,0;1.5708rad)
  sketch-geometry (1):
    g0: Circle CenterX=0 CenterY=0 CenterZ=0 NormalX=0 NormalY=0 NormalZ=1 AngleXU=0 Radius=5
  constraints (2):
    c: Coincident(g0,g-1)
    c: Diameter(g0) = 10
FEATURE [PartDesign::Pad] Pad
  Direction = (0,-1,2e-16)
  Length = 1.2
  Length2 = 10
  Placement = pos=(0,0,0) rot=(1,0,0;1.5708rad)
  Profile = -> Sketch070
  ReferenceAxis = -> Sketch070 [N_Axis]
  Refine = true
  Suppressed = false
  Type = 0
FEATURE [PartDesign::Pad] Pad001
  BaseFeature = -> Pad
  Direction = (0,-1,2e-16)
  Length = 5.6
  Length2 = 10
  Placement = pos=(0,0,0) rot=(1,0,0;1.5708rad)
  Profile = -> Sketch069
  ReferenceAxis = -> Sketch069 [N_Axis]
  Refine = true
  Suppressed = false
  Type = 0
FEATURE [PartDesign::Pocket] Pocket
  BaseFeature = -> Pad001
  Direction = (0,1,-2e-16)
  Length = 7
  Length2 = 5
  Midplane = true
  Placement = pos=(0,0,0) rot=(1,0,0;1.5708rad)
  Profile = -> Sketch071
  ReferenceAxis = -> Sketch071 [N_Axis]
  Refine = true
  Suppressed = false
  Type = 0
FEATURE [PartDesign::Fillet] Fillet
  Base = -> Pocket [Face7]
  BaseFeature = -> Pocket
  Placement = pos=(0,0,0) rot=(1,0,0;1.5708rad)
  Radius = 1
  Refine = true
  SupportTransform = false
  Suppressed = false
  UseAllEdges = false
FEATURE [PartDesign::Body] Body004  label="pulsanti lato sinistro"
  AllowCompound = false
  Group = -> [Sketch069,Sketch070,Sketch071,Pad,Pad001,Pocket,Fillet]
  Origin = -> Origin004
  Tip = -> Fillet
FEATURE [Sketcher::SketchObject] Sketch072  label="buco per saldature e diodo driver solenoide"
  ArcFitTolerance = 1e-06
  AttachmentSupport = -> [XZ_Plane]
  ExternalGeometry = -> [Sketch038]
  FullyConstrained = true
  MakeInternals = false
  MapMode = 5
  Placement = pos=(0,0,0) rot=(1,0,0;1.5708rad)
  sketch-geometry (4):
    g0: LineSegment StartX=-209.225 StartY=-40.6939 StartZ=0 EndX=-204.154 EndY=-29.8182 EndZ=0
    g1: LineSegment StartX=-204.154 StartY=-29.8182 StartZ=0 EndX=-206.51 EndY=-28.7194 EndZ=0
    g2: LineSegment StartX=-206.51 StartY=-28.7194 StartZ=0 EndX=-211.582 EndY=-39.5951 EndZ=0
    g3: LineSegment StartX=-211.582 StartY=-39.5951 StartZ=0 EndX=-209.225 EndY=-40.6939 EndZ=0
  constraints (11):
    c: Coincident(g1,g0)
    c: Coincident(g2,g1)
    c: Coincident(g3,g2)
    c: Coincident(g3,g0)
    c: Parallel(g-3,g0)
    c: Parallel(g0,g2)
    c: Perpendicular(g0,g3)
    c: Perpendicular(g1,g0)
    c: Distance(g3) = 2.6
    c: Distance(g2) = 12
    c: Coincident(g0,g-3)
FEATURE [Part::Extrusion] Extrude074  label="Extrude buco per saldature e diodo driver solenoide"
  Base = -> Sketch072
  Dir = (0,-1,2e-16)
  DirMode = 2
  FaceMakerClass = Part::FaceMakerBullseye
  FaceMakerMode = 3
  LengthFwd = 14.6
  LengthRev = 0
  Solid = true
  Symmetric = true
FEATURE [Part::Cut] Cut042
  Base = -> Cut041
  Refine = true
  Tool = -> Extrude074
FEATURE [Sketcher::SketchObject] Sketch073  label="fori slargati blocco solenoide"
  ArcFitTolerance = 1e-06
  AttachmentSupport = -> [XY_Plane]
  ExternalGeometry = -> [Sketch030]
  FullyConstrained = true
  MakeInternals = false
  MapMode = 5
  sketch-geometry (2):
    g0: Circle CenterX=-152.209 CenterY=6.95 CenterZ=0 NormalX=0 NormalY=0 NormalZ=1 AngleXU=0 Radius=3.7
    g1: Circle CenterX=-130.41 CenterY=-6.95 CenterZ=0 NormalX=0 NormalY=0 NormalZ=1 AngleXU=0 Radius=3.7
  constraints (4):
    c: Diameter(g0) = 7.4
    c: Coincident(g0,g-3)
    c: Diameter(g1) = 7.4
    c: Coincident(g1,g-4)
FEATURE [Part::Extrusion] Extrude075  label="Extrude fori slargati blocco solenoide"
  Base = -> Sketch073
  Dir = (0,0,1)
  DirMode = 2
  FaceMakerClass = Part::FaceMakerBullseye
  FaceMakerMode = 3
  LengthFwd = 1.5
  LengthRev = 0
  Placement = pos=(0,0,36.4) rot=(0,0,1;0rad)
  Solid = true
  Symmetric = false
FEATURE [Part::Cut] Cut043
  Base = -> Cut042
  Refine = true
  Tool = -> Extrude075
FEATURE [Sketcher::SketchObject] Sketch074  label="lato sx pistola"
  ArcFitTolerance = 1e-06
  AttachmentSupport = -> [XZ_Plane]
  ExternalGeometry = -> [Sketch016,Sketch,Sketch058]
  FullyConstrained = true
  MakeInternals = false
  MapMode = 5
  Placement = pos=(0,0,0) rot=(1,0,0;1.5708rad)
  sketch-geometry (37):
    g0: LineSegment StartX=-82.8 StartY=3.2 StartZ=0 EndX=0 EndY=3.2 EndZ=0
    g1: LineSegment StartX=-82.8 StartY=3.2 StartZ=0 EndX=-82.8 EndY=6.2 EndZ=0
    g2: LineSegment [constr] StartX=-107.6 StartY=18 StartZ=0 EndX=-107.6 EndY=20 EndZ=0
    g3: LineSegment [constr] StartX=-132.428 StartY=18 StartZ=0 EndX=-132.428 EndY=20 EndZ=0
    g4: LineSegment StartX=-132.428 StartY=20 StartZ=0 EndX=-107.6 EndY=20 EndZ=0
    g5: ArcOfCircle CenterX=-107.6 CenterY=4 CenterZ=0 NormalX=0 NormalY=0 NormalZ=1 AngleXU=0 Radius=16 StartAngle=0.137937 EndAngle=1.5708
    g6: LineSegment StartX=-82.8 StartY=6.2 StartZ=0 EndX=-91.752 EndY=6.2 EndZ=0
    g7: LineSegment [constr] StartX=-145.743 StartY=8.32624 StartZ=0 EndX=-147.645 EndY=8.94427 EndZ=0
    g8: ArcOfCircle CenterX=-132.428 CenterY=4 CenterZ=0 NormalX=0 NormalY=0 NormalZ=1 AngleXU=0 Radius=16 StartAngle=1.5708 EndAngle=2.82743
    g9: LineSegment StartX=-215.932 StartY=-80.4316 StartZ=0 EndX=-176.685 EndY=-80.4316 EndZ=0
    g10: LineSegment StartX=-147.645 StartY=8.94427 StartZ=0 EndX=-176.685 EndY=-80.4316 EndZ=0
    g11: LineSegment [constr] StartX=-193.988 StartY=-2.33927 StartZ=0 EndX=-192.176 EndY=-3.18451 EndZ=0
    g12: LineSegment [constr] StartX=-217.232 StartY=-52.1862 StartZ=0 EndX=-215.42 EndY=-53.0314 EndZ=0
    g13: LineSegment StartX=-192.176 StartY=-3.18451 StartZ=0 EndX=-215.42 EndY=-53.0314 EndZ=0
    g14: ArcOfCircle CenterX=-184.801 CenterY=-67.3089 CenterZ=0 NormalX=0 NormalY=0 NormalZ=1 AngleXU=0 Radius=33.7833 StartAngle=2.70526 EndAngle=3.54053
    g15: ArcOfCircle CenterX=-207.583 CenterY=4 CenterZ=0 NormalX=0 NormalY=0 NormalZ=1 AngleXU=0 Radius=17 StartAngle=5.84685 EndAngle=7.56663
    g16: LineSegment StartX=-202.765 StartY=20.303 StartZ=0 EndX=-195.887 EndY=39.2 EndZ=0
    g17: LineSegment [constr] StartX=-193.885 StartY=33.0037 StartZ=0 EndX=-197.644 EndY=34.3718 EndZ=0
    g18: LineSegment StartX=-195.887 StartY=39.2 StartZ=0 EndX=0 EndY=39.2 EndZ=0
    g19: LineSegment StartX=0 StartY=3.2 StartZ=0 EndX=0 EndY=39.2 EndZ=0
    g20: LineSegment StartX=-189.939 StartY=31.5672 StartZ=0 EndX=-192.333 EndY=24.9893 EndZ=0
    g21: LineSegment StartX=-196.467 StartY=26.4942 StartZ=0 EndX=-194.073 EndY=33.0721 EndZ=0
    g22: Circle CenterX=-213.443 CenterY=-76.8316 CenterZ=0 NormalX=0 NormalY=0 NormalZ=1 AngleXU=0 Radius=1.8
    g23: Circle CenterX=-179.305 CenterY=-76.8316 CenterZ=0 NormalX=0 NormalY=0 NormalZ=1 AngleXU=0 Radius=1.8
    g24: Circle CenterX=-184.08 CenterY=34.8 CenterZ=0 NormalX=0 NormalY=0 NormalZ=1 AngleXU=0 Radius=1.8
    g25: Circle CenterX=-78.51 CenterY=34.8 CenterZ=0 NormalX=0 NormalY=0 NormalZ=1 AngleXU=0 Radius=1.8
    g26: Circle CenterX=-78.51 CenterY=7.6 CenterZ=0 NormalX=0 NormalY=0 NormalZ=1 AngleXU=0 Radius=1.8
    g27: Circle CenterX=-5.6 CenterY=34.8 CenterZ=0 NormalX=0 NormalY=0 NormalZ=1 AngleXU=0 Radius=1.8
    g28: Circle CenterX=-5.6 CenterY=7.6 CenterZ=0 NormalX=0 NormalY=0 NormalZ=1 AngleXU=0 Radius=1.8
    g29: LineSegment StartX=-190.127 StartY=31.6356 StartZ=0 EndX=-189.939 EndY=31.5672 EndZ=0
    g30: LineSegment StartX=-194.073 StartY=33.0721 StartZ=0 EndX=-193.885 EndY=33.0037 EndZ=0
    g31: LineSegment StartX=-193.885 StartY=33.0037 StartZ=0 EndX=-190.127 EndY=31.6356 EndZ=0
    g32: LineSegment StartX=-196.467 StartY=26.4942 StartZ=0 EndX=-192.333 EndY=24.9893 EndZ=0
    g33: Circle CenterX=-19 CenterY=21.2 CenterZ=0 NormalX=0 NormalY=0 NormalZ=1 AngleXU=0 Radius=6.3
    g34: Circle CenterX=-42 CenterY=21.2 CenterZ=0 NormalX=0 NormalY=0 NormalZ=1 AngleXU=0 Radius=6.3
    g35: Circle CenterX=-65 CenterY=21.2 CenterZ=0 NormalX=0 NormalY=0 NormalZ=1 AngleXU=0 Radius=6.3
    g36: LineSegment [constr] StartX=-4 StartY=21.2 StartZ=0 EndX=-65 EndY=21.2 EndZ=0
  constraints (96):
    c: Coincident(g0,g-41)
    c: Horizontal(g0)
    c: PointOnObject(g0,g-39)
    c: Coincident(g1,g0)
    c: Vertical(g1)
    c: DistanceY(g1,g1) = 3
    c: Coincident(g2,g-17)
    c: Vertical(g2)
    c: Coincident(g3,g-16)
    c: Vertical(g3)
    c: DistanceY(g2,g2) = 2
    c: DistanceY(g3,g3) = 2
    c: Coincident(g4,g3)
    c: Coincident(g4,g2)
    c: Coincident(g5,g-17)
    c: Coincident(g5,g2)
    c: Coincident(g6,g1)
    c: Horizontal(g6)
    c: Coincident(g6,g5)
    c: Coincident(g7,g-15)
    c: Coincident(g8,g7)
    c: Coincident(g8,g3)
    c: Coincident(g8,g-15)
    c: Horizontal(g9)
    c: DistanceY(g-13,g9) = 2
    c: Coincident(g10,g7)
    c: Parallel(g10,g-14)
    c: Coincident(g9,g10)
    c: Distance(g11) = 2
    c: Coincident(g11,g-11)
    c: Perpendicular(g-11,g11)
    c: Distance(g12) = 2
    c: Coincident(g12,g-12)
    c: Perpendicular(g-11,g12)
    c: Coincident(g13,g11)
    c: Coincident(g13,g12)
    c: Coincident(g14,g-32)
    c: Coincident(g14,g12)
    c: Coincident(g14,g9)
    c: Coincident(g15,g-10)
    c: Coincident(g15,g11)
    c: Parallel(g16,g-22)
    c: Distance(g17) = 4
    c: PointOnObject(g17,g16)
    c: Coincident(g15,g16)
    c: Horizontal(g18)
    c: Coincident(g18,g16)
    c: Coincident(g19,g0)
    c: PointOnObject(g19,g-39)
    c: DistanceY(g19,g-36) = 2
    c: Coincident(g18,g19)
    c: Diameter(g22) = 3.6
    c: Coincident(g22,g-9)
    c: Diameter(g23) = 3.6
    c: Coincident(g23,g-8)
    c: Diameter(g24) = 3.6
    c: Diameter(g25) = 3.6
    c: Diameter(g26) = 3.6
    c: Diameter(g27) = 3.6
    c: Diameter(g28) = 3.6
    c: Coincident(g27,g-4)
    c: Coincident(g28,g-3)
    c: Coincident(g25,g-6)
    c: Coincident(g26,g-5)
    c: Coincident(g24,g-7)
    c: Parallel(g20,g-21)
    c: Equal(g20,g-21)
    c: Parallel(g21,g-19)
    c: Equal(g21,g-19)
    c: Distance(g29) = 0.2
    c: Distance(g30) = 0.2
    c: Parallel(g29,g-20)
    c: Parallel(g31,g-20)
    c: Equal(g31,g-20)
    c: Coincident(g30,g31)
    c: Coincident(g31,g29)
    c: Coincident(g29,g-21)
    c: Parallel(g30,g31)
    c: Coincident(g17,g30)
    c: Coincident(g20,g29)
    c: Coincident(g21,g30)
    c: Perpendicular(g16,g17)
    c: Coincident(g32,g21)
    c: Coincident(g32,g20)
    c: Perpendicular(g10,g7)
    c: Diameter(g33) = 12.6
    c: Diameter(g34) = 12.6
    c: Diameter(g35) = 12.6
    c: Horizontal(g36)
    c: PointOnObject(g33,g36)
    c: PointOnObject(g34,g36)
    c: DistanceX(g34,g33) = 23
    c: DistanceX(g35,g34) = 23
    c: DistanceX(g33,g36) = 15
    c: Symmetric(g-24,g-24,g36)
    c: Coincident(g36,g35)
FEATURE [Sketcher::SketchObject] Sketch075  label="lato dx pistola"
  ArcFitTolerance = 1e-06
  AttachmentSupport = -> [XZ_Plane]
  ExternalGeometry = -> [Sketch016,Sketch,Sketch058,Sketch074]
  FullyConstrained = true
  MakeInternals = false
  MapMode = 5
  Placement = pos=(0,0,0) rot=(1,0,0;1.5708rad)
  sketch-geometry (61):
    g0: LineSegment StartX=-82.8 StartY=3.2 StartZ=0 EndX=0 EndY=3.2 EndZ=0
    g1: LineSegment StartX=-82.8 StartY=3.2 StartZ=0 EndX=-82.8 EndY=6.2 EndZ=0
    g2: LineSegment [constr] StartX=-107.6 StartY=18 StartZ=0 EndX=-107.6 EndY=20 EndZ=0
    g3: LineSegment [constr] StartX=-132.428 StartY=18 StartZ=0 EndX=-132.428 EndY=20 EndZ=0
    g4: LineSegment StartX=-132.428 StartY=20 StartZ=0 EndX=-107.6 EndY=20 EndZ=0
    g5: ArcOfCircle CenterX=-107.6 CenterY=4 CenterZ=0 NormalX=0 NormalY=0 NormalZ=1 AngleXU=0 Radius=16 StartAngle=0.137937 EndAngle=1.5708
    g6: LineSegment StartX=-82.8 StartY=6.2 StartZ=0 EndX=-91.752 EndY=6.2 EndZ=0
    g7: LineSegment [constr] StartX=-145.743 StartY=8.32624 StartZ=0 EndX=-147.645 EndY=8.94427 EndZ=0
    g8: ArcOfCircle CenterX=-132.428 CenterY=4 CenterZ=0 NormalX=0 NormalY=0 NormalZ=1 AngleXU=0 Radius=16 StartAngle=1.5708 EndAngle=2.82743
    g9: LineSegment StartX=-215.932 StartY=-80.4316 StartZ=0 EndX=-176.685 EndY=-80.4316 EndZ=0
    g10: LineSegment StartX=-147.645 StartY=8.94427 StartZ=0 EndX=-176.685 EndY=-80.4316 EndZ=0
    g11: LineSegment [constr] StartX=-193.988 StartY=-2.33927 StartZ=0 EndX=-192.176 EndY=-3.18451 EndZ=0
    g12: LineSegment [constr] StartX=-217.232 StartY=-52.1862 StartZ=0 EndX=-215.42 EndY=-53.0314 EndZ=0
    g13: LineSegment StartX=-192.176 StartY=-3.18451 StartZ=0 EndX=-215.42 EndY=-53.0314 EndZ=0
    g14: ArcOfCircle CenterX=-184.801 CenterY=-67.3089 CenterZ=0 NormalX=0 NormalY=0 NormalZ=1 AngleXU=0 Radius=33.7833 StartAngle=2.70526 EndAngle=3.54053
    g15: ArcOfCircle CenterX=-207.583 CenterY=4 CenterZ=0 NormalX=0 NormalY=0 NormalZ=1 AngleXU=0 Radius=17 StartAngle=5.84685 EndAngle=7.56663
    g16: LineSegment StartX=-202.765 StartY=20.303 StartZ=0 EndX=-195.887 EndY=39.2 EndZ=0
    g17: LineSegment [constr] StartX=-193.885 StartY=33.0037 StartZ=0 EndX=-197.644 EndY=34.3718 EndZ=0
    g18: LineSegment StartX=-195.887 StartY=39.2 StartZ=0 EndX=0 EndY=39.2 EndZ=0
    g19: LineSegment StartX=0 StartY=3.2 StartZ=0 EndX=0 EndY=39.2 EndZ=0
    g20: LineSegment StartX=-189.939 StartY=31.5672 StartZ=0 EndX=-192.333 EndY=24.9893 EndZ=0
    g21: LineSegment StartX=-196.467 StartY=26.4942 StartZ=0 EndX=-194.073 EndY=33.0721 EndZ=0
    g22: Circle CenterX=-213.443 CenterY=-76.8316 CenterZ=0 NormalX=0 NormalY=0 NormalZ=1 AngleXU=0 Radius=1.8
    g23: Circle CenterX=-179.305 CenterY=-76.8316 CenterZ=0 NormalX=0 NormalY=0 NormalZ=1 AngleXU=0 Radius=1.8
    g24: Circle CenterX=-184.08 CenterY=34.8 CenterZ=0 NormalX=0 NormalY=0 NormalZ=1 AngleXU=0 Radius=1.8
    g25: Circle CenterX=-78.51 CenterY=34.8 CenterZ=0 NormalX=0 NormalY=0 NormalZ=1 AngleXU=0 Radius=1.8
    g26: Circle CenterX=-78.51 CenterY=7.6 CenterZ=0 NormalX=0 NormalY=0 NormalZ=1 AngleXU=0 Radius=1.8
    g27: Circle CenterX=-5.6 CenterY=34.8 CenterZ=0 NormalX=0 NormalY=0 NormalZ=1 AngleXU=0 Radius=1.8
    g28: Circle CenterX=-5.6 CenterY=7.6 CenterZ=0 NormalX=0 NormalY=0 NormalZ=1 AngleXU=0 Radius=1.8
    g29: LineSegment StartX=-190.127 StartY=31.6356 StartZ=0 EndX=-189.939 EndY=31.5672 EndZ=0
    g30: LineSegment StartX=-194.073 StartY=33.0721 StartZ=0 EndX=-193.885 EndY=33.0037 EndZ=0
    g31: LineSegment StartX=-193.885 StartY=33.0037 StartZ=0 EndX=-190.127 EndY=31.6356 EndZ=0
    g32: LineSegment StartX=-196.467 StartY=26.4942 StartZ=0 EndX=-192.333 EndY=24.9893 EndZ=0
    g33: LineSegment [constr] StartX=-4 StartY=21.2 StartZ=0 EndX=-87.91 EndY=21.2 EndZ=0
    g34: GeomPoint [constr] X=-4 Y=21.2 Z=0
    g35: LineSegment [constr] StartX=-15.2 StartY=33.7 StartZ=0 EndX=-15.2 EndY=8.7 EndZ=0
    g36: LineSegment [constr] StartX=-15.2 StartY=33.7 StartZ=0 EndX=-56.2 EndY=33.7 EndZ=0
    g37: LineSegment [constr] StartX=-15.2 StartY=8.7 StartZ=0 EndX=-56.2 EndY=8.7 EndZ=0
    g38: LineSegment [constr] StartX=-56.2 StartY=33.7 StartZ=0 EndX=-56.2 EndY=8.7 EndZ=0
    g39: Circle CenterX=-18.6 CenterY=30.3 CenterZ=0 NormalX=0 NormalY=0 NormalZ=1 AngleXU=0 Radius=3.4
    g40: Circle CenterX=-18.6 CenterY=12.1 CenterZ=0 NormalX=0 NormalY=0 NormalZ=1 AngleXU=0 Radius=3.4
    g41: Circle CenterX=-43.2 CenterY=30.3 CenterZ=0 NormalX=0 NormalY=0 NormalZ=1 AngleXU=0 Radius=3.4
    g42: Circle CenterX=-43.2 CenterY=12.1 CenterZ=0 NormalX=0 NormalY=0 NormalZ=1 AngleXU=0 Radius=3.4
    g43: LineSegment [constr] StartX=-4 StartY=21.2 StartZ=0 EndX=-15.2 EndY=21.2 EndZ=0
    g44: LineSegment [constr] StartX=-15.2 StartY=21.2 StartZ=0 EndX=-36.2 EndY=21.2 EndZ=0
    g45: LineSegment [constr] StartX=-41.5 StartY=16.2 StartZ=0 EndX=-30.9 EndY=16.2 EndZ=0
    g46: LineSegment [constr] StartX=-30.9 StartY=16.2 StartZ=0 EndX=-30.9 EndY=26.2 EndZ=0
    g47: LineSegment [constr] StartX=-30.9 StartY=26.2 StartZ=0 EndX=-41.5 EndY=26.2 EndZ=0
    g48: LineSegment [constr] StartX=-41.5 StartY=26.2 StartZ=0 EndX=-41.5 EndY=16.2 EndZ=0
    g49: GeomPoint [constr] X=-36.2 Y=21.2 Z=0
    g50: Circle CenterX=-36.2 CenterY=21.2 CenterZ=0 NormalX=0 NormalY=0 NormalZ=1 AngleXU=0 Radius=2.8
    g51: LineSegment [constr] StartX=-24.2 StartY=26.7 StartZ=0 EndX=-24.2 EndY=15.7 EndZ=0
    g52: Circle CenterX=-24.2 CenterY=26.7 CenterZ=0 NormalX=0 NormalY=0 NormalZ=1 AngleXU=0 Radius=3
    g53: Circle CenterX=-24.2 CenterY=15.7 CenterZ=0 NormalX=0 NormalY=0 NormalZ=1 AngleXU=0 Radius=3
    g54: GeomPoint X=-18.6 Y=30.3 Z=0
    g55: GeomPoint X=-18.6 Y=12.1 Z=0
    g56: GeomPoint X=-43.2 Y=12.1 Z=0
    g57: GeomPoint X=-43.2 Y=30.3 Z=0
    g58: Circle CenterX=-65 CenterY=21.2 CenterZ=0 NormalX=0 NormalY=0 NormalZ=1 AngleXU=0 Radius=1.5
    g59: Circle CenterX=-42 CenterY=21.2 CenterZ=0 NormalX=0 NormalY=0 NormalZ=1 AngleXU=0 Radius=1.5
    g60: Circle CenterX=-19 CenterY=21.2 CenterZ=0 NormalX=0 NormalY=0 NormalZ=1 AngleXU=0 Radius=1.5
  constraints (149):
    c: Coincident(g0,g-41)
    c: Horizontal(g0)
    c: PointOnObject(g0,g-39)
    c: Coincident(g1,g0)
    c: Vertical(g1)
    c: DistanceY(g1,g1) = 3
    c: Coincident(g2,g-17)
    c: Vertical(g2)
    c: Coincident(g3,g-16)
    c: Vertical(g3)
    c: DistanceY(g2,g2) = 2
    c: DistanceY(g3,g3) = 2
    c: Coincident(g4,g3)
    c: Coincident(g4,g2)
    c: Coincident(g5,g-17)
    c: Coincident(g5,g2)
    c: Coincident(g6,g1)
    c: Horizontal(g6)
    c: Coincident(g6,g5)
    c: Coincident(g7,g-15)
    c: Coincident(g8,g7)
    c: Coincident(g8,g3)
    c: Coincident(g8,g-15)
    c: Horizontal(g9)
    c: DistanceY(g-13,g9) = 2
    c: Coincident(g10,g7)
    c: Parallel(g10,g-14)
    c: Coincident(g9,g10)
    c: Distance(g11) = 2
    c: Coincident(g11,g-11)
    c: Perpendicular(g-11,g11)
    c: Distance(g12) = 2
    c: Coincident(g12,g-12)
    c: Perpendicular(g-11,g12)
    c: Coincident(g13,g11)
    c: Coincident(g13,g12)
    c: Coincident(g14,g-32)
    c: Coincident(g14,g12)
    c: Coincident(g14,g9)
    c: Coincident(g15,g-10)
    c: Coincident(g15,g11)
    c: Parallel(g16,g-22)
    c: Distance(g17) = 4
    c: PointOnObject(g17,g16)
    c: Coincident(g15,g16)
    c: Horizontal(g18)
    c: Coincident(g18,g16)
    c: Coincident(g19,g0)
    c: PointOnObject(g19,g-39)
    c: DistanceY(g19,g-36) = 2
    c: Coincident(g18,g19)
    c: Diameter(g22) = 3.6
    c: Coincident(g22,g-9)
    c: Diameter(g23) = 3.6
    c: Coincident(g23,g-8)
    c: Diameter(g24) = 3.6
    c: Diameter(g25) = 3.6
    c: Diameter(g26) = 3.6
    c: Diameter(g27) = 3.6
    c: Diameter(g28) = 3.6
    c: Coincident(g27,g-4)
    c: Coincident(g28,g-3)
    c: Coincident(g25,g-6)
    c: Coincident(g26,g-5)
    c: Coincident(g24,g-7)
    c: Parallel(g20,g-21)
    c: Equal(g20,g-21)
    c: Parallel(g21,g-19)
    c: Equal(g21,g-19)
    c: Distance(g29) = 0.2
    c: Distance(g30) = 0.2
    c: Parallel(g29,g-20)
    c: Parallel(g31,g-20)
    c: Equal(g31,g-20)
    c: Coincident(g30,g31)
    c: Coincident(g31,g29)
    c: Coincident(g29,g-21)
    c: Parallel(g30,g31)
    c: Coincident(g17,g30)
    c: Coincident(g20,g29)
    c: Coincident(g21,g30)
    c: Perpendicular(g16,g17)
    c: Coincident(g32,g21)
    c: Coincident(g32,g20)
    c: Perpendicular(g10,g7)
    c: Horizontal(g33)
    c: Symmetric(g-24,g-24,g33)
    c: PointOnObject(g33,g-28)
    c: Symmetric(g-24,g-24,g34)
    c: DistanceY(g35,g35) = 25
    c: Symmetric(g35,g35,g33)
    c: Distance(g36) = 41
    c: Coincident(g36,g35)
    c: Horizontal(g36)
    c: Coincident(g37,g35)
    c: Horizontal(g37)
    c: Coincident(g38,g36)
    c: Vertical(g38)
    c: Coincident(g37,g38)
    c: Diameter(g39) = 6.8
    c: Diameter(g40) = 6.8
    c: Tangent(g39,g36)
    c: Tangent(g40,g37)
    c: Tangent(g39,g35)
    c: Tangent(g40,g35)
    c: Diameter(g41) = 6.8
    c: Diameter(g42) = 6.8
    c: Tangent(g41,g36)
    c: Tangent(g42,g37)
    c: DistanceX(g41,g39) = 24.6
    c: DistanceX(g42,g40) = 24.6
    c: Distance(g43) = 11.2
    c: Coincident(g43,g33)
    c: PointOnObject(g43,g33)
    c: PointOnObject(g43,g35)
    c: Distance(g44) = 21
    c: Coincident(g44,g43)
    c: PointOnObject(g44,g33)
    c: Coincident(g45,g46)
    c: Coincident(g46,g47)
    c: Coincident(g47,g48)
    c: Coincident(g48,g45)
    c: Horizontal(g45)
    c: Horizontal(g47)
    c: Vertical(g46)
    c: Vertical(g48)
    c: Symmetric(g47,g45,g49)
    c: Distance(g46,g48) = 10.6
    c: Distance(g45,g47) = 10
    c: Coincident(g49,g44)
    c: Diameter(g50) = 5.6
    c: Coincident(g50,g44)
    c: Distance(g51) = 11
    c: Symmetric(g51,g51,g33)
    c: DistanceX(g51,g43) = 9
    c: Diameter(g52) = 6
    c: Coincident(g52,g51)
    c: Diameter(g53) = 6
    c: Coincident(g53,g51)
    c: Coincident(g40,g55)
    c: Coincident(g39,g54)
    c: Coincident(g41,g57)
    c: Coincident(g42,g56)
    c: Diameter(g58) = 3
    c: Diameter(g59) = 3
    c: Diameter(g60) = 3
    c: Coincident(g58,g-44)
    c: Coincident(g59,g-46)
    c: Coincident(g60,g-45)
FEATURE [PartDesign::Body] Body  label="Struttura pistola"
  AllowCompound = false
  Group = -> [Sketch,Sketch002,Sketch004,DatumPlane,Sketch005,DatumPlane001,CopyCut,Sketch008,Sketch009,Sketch010,Sketch011,Sketch012,Sketch013,Sketch014,Sketch015,Sketch016,Sketch017,Sketch018,Sketch019,Sketch020,Sketch022,Sketch023,Sketch024,Sketch025,Sketch026,Sketch027,Sketch029,Sketch030,Sketch031,Sketch032,Sketch033,Sketch034,Sketch035,Sketch036,Sketch037,Sketch038,Sketch039,Sketch040,Sketch041,Sketch042,+15 more]
  Origin = -> Origin
FEATURE [Sketcher::SketchObject] Sketch078
  ArcFitTolerance = 1e-06
  AttachmentSupport = -> [XZ_Plane005]
  FullyConstrained = true
  MakeInternals = false
  MapMode = 5
  Placement = pos=(0,0,0) rot=(1,0,0;1.5708rad)
  sketch-geometry (5):
    g0: LineSegment [constr] StartX=0 StartY=5.5 StartZ=0 EndX=0 EndY=-5.5 EndZ=0
    g1: ArcOfCircle CenterX=0 CenterY=5.5 CenterZ=0 NormalX=0 NormalY=0 NormalZ=1 AngleXU=0 Radius=2.7 StartAngle=0 EndAngle=3.14159
    g2: ArcOfCircle CenterX=0 CenterY=-5.5 CenterZ=0 NormalX=0 NormalY=0 NormalZ=1 AngleXU=0 Radius=2.7 StartAngle=3.1416 EndAngle=6.28318
    g3: LineSegment StartX=-2.7 StartY=5.5 StartZ=0 EndX=-2.7 EndY=-5.50001 EndZ=0
    g4: LineSegment StartX=2.7 StartY=5.5 StartZ=0 EndX=2.7 EndY=-5.50001 EndZ=0
  constraints (13):
    c: Distance(g0) = 11
    c: Vertical(g0)
    c: Symmetric(g0,g0,g-1)
    c: Radius(g1) = 2.7
    c: Coincident(g1,g0)
    c: Radius(g2) = 2.7
    c: Coincident(g2,g0)
    c: Vertical(g3)
    c: Vertical(g4)
    c: Coincident(g2,g4)
    c: Coincident(g2,g3)
    c: Tangent(g3,g1) = -1.5708
    c: Tangent(g4,g1) = 1.5708
FEATURE [PartDesign::Pad] Pad002
  Direction = (0,-1,2e-16)
  Length = 0.8
  Length2 = 10
  Placement = pos=(0,0,0) rot=(1,0,0;1.5708rad)
  Profile = -> Sketch078
  ReferenceAxis = -> Sketch078 [N_Axis]
  Refine = true
  Suppressed = false
  Type = 0
FEATURE [Sketcher::SketchObject] Sketch079
  ArcFitTolerance = 1e-06
  AttachmentSupport = -> [XZ_Plane005]
  ExternalGeometry = -> [Sketch078]
  FullyConstrained = true
  MakeInternals = false
  MapMode = 5
  Placement = pos=(0,0,0) rot=(1,0,0;1.5708rad)
  sketch-geometry (2):
    g0: Circle CenterX=-1e-16 CenterY=5.5 CenterZ=0 NormalX=0 NormalY=0 NormalZ=1 AngleXU=0 Radius=2.7
    g1: Circle CenterX=0 CenterY=-5.5 CenterZ=0 NormalX=0 NormalY=0 NormalZ=1 AngleXU=0 Radius=2.7
  constraints (4):
    c: Coincident(g0,g-3)
    c: PointOnObject(g-3,g0)
    c: Coincident(g1,g-4)
    c: Equal(g1,g-4)
FEATURE [PartDesign::Pad] Pad003
  BaseFeature = -> Pad002
  Direction = (0,-1,2e-16)
  Length = 5
  Length2 = 10
  Placement = pos=(0,0,0) rot=(1,0,0;1.5708rad)
  Profile = -> Sketch079
  ReferenceAxis = -> Sketch079 [N_Axis]
  Refine = true
  Suppressed = false
  Type = 0
FEATURE [PartDesign::Fillet] Fillet001
  Base = -> Pad003 [Edge16,Edge14]
  BaseFeature = -> Pad003
  Placement = pos=(0,0,0) rot=(1,0,0;1.5708rad)
  Radius = 0.4
  Refine = true
  SupportTransform = false
  Suppressed = false
  UseAllEdges = false
FEATURE [PartDesign::Body] Body005  label="pulsanti lato destro"
  AllowCompound = false
  Group = -> [Sketch078,Pad002,Sketch079,Pad003,Fillet001]
  Origin = -> Origin005
  Tip = -> Fillet001
FEATURE [PartDesign::SubShapeBinder] Binder
  BindCopyOnChange = 0
  BindMode = 0
  ClaimChildren = false
  Context = -> Body006 [Binder.]
  Fuse = false
  MakeFace = true
  OffsetFill = false
  OffsetIntersection = false
  OffsetJoinType = 0
  OffsetOpenResult = false
  PartialLoad = false
  Refine = true
  Relative = true
  Support = -> [Body[Sketch074.]]
  _Version = 2
FEATURE [PartDesign::SubShapeBinder] Binder001
  BindCopyOnChange = 0
  BindMode = 0
  ClaimChildren = false
  Context = -> Body007 [Binder001.]
  Fuse = false
  MakeFace = true
  OffsetFill = false
  OffsetIntersection = false
  OffsetJoinType = 0
  OffsetOpenResult = false
  PartialLoad = false
  Refine = true
  Relative = true
  Support = -> [Body[Sketch075.]]
  _Version = 2
FEATURE [Mesh::Feature] logo_per_PCB_definitivo_positivo
  Placement = pos=(-191,17,-66) rot=(0,1,1;0rad)
FEATURE [Sketcher::SketchObject] Sketch114  label="Sketch114 - base lato DX"
  ArcFitTolerance = 1e-06
  AttachmentSupport = -> [Binder001]
  ExternalGeometry = -> [Binder001]
  FullyConstrained = true
  MakeInternals = false
  MapMode = 5
  Placement = pos=(0,1e-15,0) rot=(0,0.707107,0.707107;3.14159rad)
  sketch-geometry (30):
    g0: Circle CenterX=5.6 CenterY=34.8 CenterZ=0 NormalX=0 NormalY=0 NormalZ=1 AngleXU=0 Radius=1.8
    g1: Circle CenterX=5.6 CenterY=7.6 CenterZ=0 NormalX=0 NormalY=0 NormalZ=1 AngleXU=0 Radius=1.8
    g2: Circle CenterX=24.2 CenterY=26.7 CenterZ=0 NormalX=0 NormalY=0 NormalZ=1 AngleXU=0 Radius=3
    g3: Circle CenterX=24.2 CenterY=15.7 CenterZ=0 NormalX=0 NormalY=0 NormalZ=1 AngleXU=0 Radius=3
    g4: Circle CenterX=36.2 CenterY=21.2 CenterZ=0 NormalX=0 NormalY=0 NormalZ=1 AngleXU=0 Radius=2.8
    g5: Circle CenterX=78.51 CenterY=34.8 CenterZ=0 NormalX=0 NormalY=0 NormalZ=1 AngleXU=0 Radius=1.8
    g6: Circle CenterX=78.51 CenterY=7.6 CenterZ=0 NormalX=0 NormalY=0 NormalZ=1 AngleXU=0 Radius=1.8
    g7: Circle CenterX=184.08 CenterY=34.8 CenterZ=0 NormalX=0 NormalY=0 NormalZ=1 AngleXU=0 Radius=1.8
    g8: Circle CenterX=213.443 CenterY=-76.8316 CenterZ=0 NormalX=0 NormalY=0 NormalZ=1 AngleXU=0 Radius=1.8
    g9: Circle CenterX=179.305 CenterY=-76.8316 CenterZ=0 NormalX=0 NormalY=0 NormalZ=1 AngleXU=0 Radius=1.8
    g10: ArcOfCircle [constr] CenterX=132.428 CenterY=4 CenterZ=0 NormalX=0 NormalY=0 NormalZ=1 AngleXU=0 Radius=16 StartAngle=0.314159 EndAngle=1.5708
    g11: ArcOfCircle CenterX=107.6 CenterY=4 CenterZ=0 NormalX=0 NormalY=0 NormalZ=1 AngleXU=0 Radius=16 StartAngle=1.5708 EndAngle=3.00366
    g12: ArcOfCircle CenterX=207.583 CenterY=4 CenterZ=0 NormalX=0 NormalY=0 NormalZ=1 AngleXU=0 Radius=17 StartAngle=1.85815 EndAngle=3.57792
    g13: ArcOfCircle CenterX=184.801 CenterY=-67.3089 CenterZ=0 NormalX=0 NormalY=0 NormalZ=1 AngleXU=0 Radius=33.7833 StartAngle=5.88425 EndAngle=6.71952
    g14: LineSegment StartX=0 StartY=39.2 StartZ=0 EndX=0 EndY=3.2 EndZ=0
    g15: LineSegment StartX=0 StartY=3.2 StartZ=0 EndX=82.8 EndY=3.2 EndZ=0
    g16: LineSegment StartX=82.8 StartY=3.2 StartZ=0 EndX=82.8 EndY=6.2 EndZ=0
    g17: LineSegment StartX=82.8 StartY=6.2 StartZ=0 EndX=91.752 EndY=6.2 EndZ=0
    g18: LineSegment StartX=107.6 StartY=20 StartZ=0 EndX=132.428 EndY=20 EndZ=0
    g19: LineSegment StartX=147.645 StartY=8.94427 StartZ=0 EndX=176.685 EndY=-80.4316 EndZ=0
    g20: LineSegment StartX=176.685 StartY=-80.4316 StartZ=0 EndX=215.932 EndY=-80.4316 EndZ=0
    g21: LineSegment StartX=215.42 StartY=-53.0314 StartZ=0 EndX=192.176 EndY=-3.18451 EndZ=0
    g22: LineSegment StartX=202.765 StartY=20.303 StartZ=0 EndX=195.887 EndY=39.2 EndZ=0
    g23: LineSegment StartX=195.887 StartY=39.2 StartZ=0 EndX=0 EndY=39.2 EndZ=0
    g24: LineSegment StartX=196.467 StartY=26.4942 StartZ=0 EndX=194.073 EndY=33.0721 EndZ=0
    g25: LineSegment StartX=194.073 StartY=33.0721 StartZ=0 EndX=189.939 EndY=31.5672 EndZ=0
    g26: LineSegment StartX=189.939 StartY=31.5672 StartZ=0 EndX=192.333 EndY=24.9893 EndZ=0
    g27: LineSegment StartX=192.333 StartY=24.9893 StartZ=0 EndX=196.467 EndY=26.4942 EndZ=0
    g28: LineSegment StartX=132.428 StartY=20 StartZ=0 EndX=144.053 EndY=20 EndZ=0
    g29: LineSegment StartX=144.053 StartY=20 StartZ=0 EndX=147.645 EndY=8.94427 EndZ=0
  constraints (65):
    c: Equal(g0,g-25)
    c: Equal(g2,g-29)
    c: Equal(g3,g-30)
    c: Equal(g4,g-28)
    c: Equal(g1,g-26)
    c: Coincident(g0,g-25)
    c: Coincident(g1,g-26)
    c: Coincident(g2,g-29)
    c: Coincident(g3,g-30)
    c: Coincident(g4,g-28)
    c: Equal(g5,g-23)
    c: Equal(g6,g-24)
    c: Coincident(g5,g-23)
    c: Coincident(g6,g-24)
    c: Equal(g7,g-20)
    c: Coincident(g7,g-20)
    c: Equal(g9,g-22)
    c: Coincident(g9,g-22)
    c: Equal(g8,g-21)
    c: Coincident(g8,g-21)
    c: Equal(g13,g-12)
    c: Equal(g12,g-14)
    c: Equal(g10,g-9)
    c: Equal(g11,g-7)
    c: Coincident(g14,g-27)
    c: Coincident(g14,g-27)
    c: Coincident(g15,g14)
    c: Coincident(g15,g-5)
    c: Coincident(g16,g15)
    c: Coincident(g16,g-6)
    c: Coincident(g17,g16)
    c: Coincident(g17,g-7)
    c: Coincident(g11,g17)
    c: Coincident(g11,g-8)
    c: Coincident(g18,g11)
    c: Coincident(g18,g-9)
    c: Coincident(g10,g18)
    c: Coincident(g10,g-10)
    c: Coincident(g19,g10)
    c: Coincident(g19,g-11)
    c: Coincident(g20,g19)
    c: Coincident(g20,g-12)
    c: Coincident(g13,g20)
    c: Coincident(g13,g-13)
    c: Coincident(g21,g13)
    c: Coincident(g21,g-14)
    c: Coincident(g12,g21)
    c: Coincident(g12,g-15)
    c: Coincident(g22,g12)
    c: Coincident(g22,g-15)
    c: Coincident(g23,g22)
    c: Coincident(g23,g14)
    c: Coincident(g24,g-18)
    c: Coincident(g24,g-16)
    c: Coincident(g25,g24)
    c: Coincident(g25,g-19)
    c: Coincident(g26,g25)
    c: Coincident(g26,g-19)
    c: Coincident(g27,g26)
    c: Coincident(g27,g24)
    c: Coincident(g29,g10)
    c: Coincident(g28,g10)
    c: Coincident(g29,g28)
    c: Parallel(g28,g18)
    c: Parallel(g29,g19)
FEATURE [PartDesign::Pad] Pad011
  Direction = (0,1,-2e-16)
  Length = 2
  Length2 = 10
  Profile = -> Sketch114
  ReferenceAxis = -> Sketch114 [N_Axis]
  Refine = true
  Reversed = true
  Suppressed = false
  Type = 0
FEATURE [Sketcher::SketchObject] Sketch115
  ArcFitTolerance = 1e-06
  AttachmentSupport = -> [Pad011]
  ExternalGeometry = -> [Binder001]
  FullyConstrained = true
  MakeInternals = false
  MapMode = 5
  Placement = pos=(0,1.7e-15,0) rot=(0,0.707107,0.707107;3.14159rad)
  sketch-geometry (4):
    g0: ArcOfCircle CenterX=24.2 CenterY=26.7 CenterZ=0 NormalX=0 NormalY=0 NormalZ=1 AngleXU=0 Radius=3 StartAngle=4.48384e-08 EndAngle=3.14159
    g1: ArcOfCircle CenterX=24.2 CenterY=15.7 CenterZ=0 NormalX=0 NormalY=0 NormalZ=1 AngleXU=0 Radius=3 StartAngle=3.14159 EndAngle=6.28318
    g2: LineSegment StartX=21.2 StartY=26.7 StartZ=0 EndX=21.2 EndY=15.7 EndZ=0
    g3: LineSegment StartX=27.2 StartY=26.7 StartZ=0 EndX=27.2 EndY=15.7 EndZ=0
  constraints (12):
    c: Equal(g1,g-4)
    c: Equal(g0,g-3)
    c: Coincident(g0,g-3)
    c: Coincident(g1,g-4)
    c: Vertical(g2)
    c: Vertical(g3)
    c: Tangent(g3,g-3)
    c: Tangent(g2,g-3)
    c: Coincident(g0,g2)
    c: Coincident(g0,g3)
    c: Coincident(g1,g2)
    c: Coincident(g3,g1)
FEATURE [Sketcher::SketchObject] Sketch117  label="Sketch117 - fori per inserto M3 x 3 x 4.5"
  ArcFitTolerance = 1e-06
  AttachmentSupport = -> [Pad011]
  ExternalGeometry = -> [Binder001]
  FullyConstrained = true
  MakeInternals = false
  MapMode = 5
  Placement = pos=(0,1.7e-15,0) rot=(0,0.707107,0.707107;3.14159rad)
  sketch-geometry (4):
    g0: Circle CenterX=43.2 CenterY=30.3 CenterZ=0 NormalX=0 NormalY=0 NormalZ=1 AngleXU=0 Radius=2.25
    g1: Circle CenterX=43.2 CenterY=12.1 CenterZ=0 NormalX=0 NormalY=0 NormalZ=1 AngleXU=0 Radius=2.25
    g2: Circle CenterX=18.6 CenterY=30.3 CenterZ=0 NormalX=0 NormalY=0 NormalZ=1 AngleXU=0 Radius=2.25
    g3: Circle CenterX=18.6 CenterY=12.1 CenterZ=0 NormalX=0 NormalY=0 NormalZ=1 AngleXU=0 Radius=2.25
  constraints (8):
    c: Diameter(g0) = 4.5
    c: Diameter(g1) = 4.5
    c: Diameter(g2) = 4.5
    c: Diameter(g3) = 4.5
    c: Coincident(g2,g-3)
    c: Coincident(g3,g-6)
    c: Coincident(g0,g-4)
    c: Coincident(g1,g-5)
FEATURE [Sketcher::SketchObject] Sketch118
  ArcFitTolerance = 1e-06
  AttachmentSupport = -> [Pad011]
  ExternalGeometry = -> [Binder001]
  FullyConstrained = true
  MakeInternals = false
  MapMode = 5
  Placement = pos=(0,-2,0) rot=(1,0,0;1.5708rad)
  sketch-geometry (12):
    g0: Circle CenterX=-78.51 CenterY=34.8 CenterZ=0 NormalX=0 NormalY=0 NormalZ=1 AngleXU=0 Radius=1.8
    g1: Circle CenterX=-78.51 CenterY=7.6 CenterZ=0 NormalX=0 NormalY=0 NormalZ=1 AngleXU=0 Radius=1.8
    g2: Circle CenterX=-5.6 CenterY=34.8 CenterZ=0 NormalX=0 NormalY=0 NormalZ=1 AngleXU=0 Radius=1.8
    g3: Circle CenterX=-5.6 CenterY=7.6 CenterZ=0 NormalX=0 NormalY=0 NormalZ=1 AngleXU=0 Radius=1.8
    g4: LineSegment StartX=0 StartY=39.2 StartZ=0 EndX=0 EndY=3.2 EndZ=0
    g5: LineSegment StartX=0 StartY=3.2 StartZ=0 EndX=-82.8 EndY=3.2 EndZ=0
    g6: LineSegment StartX=-82.8 StartY=3.2 StartZ=0 EndX=-82.8 EndY=39.2 EndZ=0
    g7: LineSegment StartX=-82.8 StartY=39.2 StartZ=0 EndX=0 EndY=39.2 EndZ=0
    g8: ArcOfCircle CenterX=-65 CenterY=21.2 CenterZ=0 NormalX=0 NormalY=0 NormalZ=1 AngleXU=0 Radius=10 StartAngle=1.5708 EndAngle=4.71239
    g9: ArcOfCircle CenterX=-19 CenterY=21.2 CenterZ=0 NormalX=0 NormalY=0 NormalZ=1 AngleXU=0 Radius=10 StartAngle=4.71239 EndAngle=7.85398
    g10: LineSegment StartX=-65 StartY=31.2 StartZ=0 EndX=-19 EndY=31.2 EndZ=0
    g11: LineSegment StartX=-65 StartY=11.2 StartZ=0 EndX=-19 EndY=11.2 EndZ=0
  constraints (25):
    c: Equal(g2,g-5)
    c: Equal(g3,g-7)
    c: Equal(g1,g-6)
    c: Equal(g0,g-4)
    c: Coincident(g0,g-4)
    c: Coincident(g1,g-6)
    c: Coincident(g3,g-7)
    c: Coincident(g2,g-5)
    c: Coincident(g4,g-8)
    c: Coincident(g4,g-9)
    c: Coincident(g5,g4)
    c: Coincident(g5,g-10)
    c: Coincident(g6,g5)
    c: PointOnObject(g6,g-3)
    c: Vertical(g6)
    c: Coincident(g7,g6)
    c: Coincident(g7,g4)
    c: Tangent(g8,g10) = 1.5708
    c: Tangent(g8,g11) = -1.5708
    c: Tangent(g9,g10) = 1.5708
    c: Tangent(g9,g11) = -1.5708
    c: Equal(g8,g9)
    c: Radius(g8) = 10
    c: Coincident(g8,g-11)
    c: Coincident(g9,g-12)
FEATURE [Sketcher::SketchObject] Sketch120
  ArcFitTolerance = 1e-06
  AttachmentSupport = -> [Pad011]
  ExternalGeometry = -> [Binder001]
  FullyConstrained = true
  MakeInternals = false
  MapMode = 5
  Placement = pos=(0,-2,0) rot=(1,0,0;1.5708rad)
  sketch-geometry (4):
    g0: LineSegment StartX=-137.815 StartY=39.2 StartZ=0 EndX=-142.655 EndY=24.303 EndZ=0
    g1: LineSegment StartX=-137.815 StartY=39.2 StartZ=0 EndX=-110.815 EndY=39.2 EndZ=0
    g2: LineSegment StartX=-142.655 StartY=24.303 StartZ=0 EndX=-110.815 EndY=24.303 EndZ=0
    g3: ArcOfCircle CenterX=-92.2534 CenterY=31.7515 CenterZ=0 NormalX=0 NormalY=0 NormalZ=1 AngleXU=0 Radius=20 StartAngle=2.75997 EndAngle=3.52321
  constraints (12):
    c: PointOnObject(g0,g-3)
    c: Coincident(g1,g0)
    c: PointOnObject(g1,g-3)
    c: Coincident(g2,g0)
    c: Horizontal(g2)
    c: Tangent(g0,g-4)
    c: Vertical(g2,g1)
    c: DistanceX(g1,g1) = 27
    c: DistanceY(g-6,g0) = 4
    c: Radius(g3) = 20
    c: Coincident(g3,g1)
    c: Coincident(g3,g2)
FEATURE [Sketcher::SketchObject] Sketch121
  ArcFitTolerance = 1e-06
  AttachmentSupport = -> [Pad011]
  ExternalGeometry = -> [Binder001]
  FullyConstrained = true
  MakeInternals = false
  MapMode = 5
  Placement = pos=(0,-2,0) rot=(1,0,0;1.5708rad)
  sketch-geometry (15):
    g0: LineSegment StartX=-137.815 StartY=39.2 StartZ=0 EndX=-143.955 EndY=20.303 EndZ=0
    g1: LineSegment StartX=-143.955 StartY=20.303 StartZ=0 EndX=-190.141 EndY=20.303 EndZ=0
    g2: LineSegment StartX=-190.141 StartY=20.303 StartZ=0 EndX=-186.139 EndY=31.3 EndZ=0
    g3: LineSegment StartX=-178.754 StartY=39.2 StartZ=0 EndX=-180.791 EndY=33.6029 EndZ=0
    g4: ArcOfCircle CenterX=-184.08 CenterY=34.8 CenterZ=0 NormalX=0 NormalY=0 NormalZ=1 AngleXU=0 Radius=3.5 StartAngle=4.71239 EndAngle=5.93412
    g5: LineSegment StartX=-184.08 StartY=31.3 StartZ=0 EndX=-186.139 EndY=31.3 EndZ=0
    g6: LineSegment StartX=-137.815 StartY=39.2 StartZ=0 EndX=-156.815 EndY=39.2 EndZ=0
    g7: LineSegment StartX=-168.815 StartY=39.2 StartZ=0 EndX=-178.754 EndY=39.2 EndZ=0
    g8: LineSegment StartX=-157.815 StartY=39.2 StartZ=0 EndX=-167.815 EndY=39.2 EndZ=0
    g9: LineSegment StartX=-168.815 StartY=31.2 StartZ=0 EndX=-156.815 EndY=31.2 EndZ=0
    g10: LineSegment StartX=-167.436 StartY=36.2 StartZ=0 EndX=-157.436 EndY=36.2 EndZ=0
    g11: ArcOfCircle CenterX=-176.411 CenterY=35.2 CenterZ=0 NormalX=0 NormalY=0 NormalZ=1 AngleXU=0 Radius=20 StartAngle=6.08183 EndAngle=6.48454
    g12: ArcOfCircle CenterX=-188.411 CenterY=35.2 CenterZ=0 NormalX=0 NormalY=0 NormalZ=1 AngleXU=0 Radius=20 StartAngle=6.08183 EndAngle=6.48454
    g13: ArcOfCircle CenterX=-177.411 CenterY=35.2 CenterZ=0 NormalX=0 NormalY=0 NormalZ=1 AngleXU=0 Radius=20 StartAngle=0.0500209 EndAngle=0.201358
    g14: ArcOfCircle CenterX=-187.411 CenterY=35.2 CenterZ=0 NormalX=0 NormalY=0 NormalZ=1 AngleXU=0 Radius=20 StartAngle=0.0500209 EndAngle=0.201358
  constraints (46):
    c: PointOnObject(g0,g-3)
    c: Tangent(g0,g-5)
    c: Coincident(g1,g0)
    c: Horizontal(g1)
    c: Coincident(g2,g1)
    c: PointOnObject(g3,g-3)
    c: Parallel(g3,g-6)
    c: Parallel(g2,g-6)
    c: Radius(g4) = 3.5
    c: Coincident(g4,g-7)
    c: Tangent(g3,g4) = 1.5708
    c: Horizontal(g5)
    c: Tangent(g5,g4) = 1.5708
    c: DistanceX(g-8,g5) = 3.8
    c: Coincident(g2,g5)
    c: Coincident(g6,g0)
    c: PointOnObject(g6,g-3)
    c: DistanceX(g6,g6) = 19
    c: PointOnObject(g7,g-3)
    c: DistanceX(g7,g6) = 12
    c: Coincident(g7,g3)
    c: PointOnObject(g8,g-3)
    c: PointOnObject(g8,g-3)
    c: DistanceX(g8,g8) = 10
    c: DistanceX(g8,g6) = 1
    c: Horizontal(g9)
    c: Vertical(g7,g9)
    c: Vertical(g6,g9)
    c: DistanceY(g9,g7) = 8
    c: Horizontal(g10)
    c: Equal(g8,g10)
    c: DistanceY(g10,g8) = 3
    c: Radius(g11) = 20
    c: Coincident(g11,g6)
    c: Coincident(g11,g9)
    c: Radius(g12) = 20
    c: Coincident(g12,g7)
    c: Coincident(g12,g9)
    c: Equal(g13,g11)
    c: Coincident(g13,g8)
    c: Coincident(g13,g10)
    c: Horizontal(g13,g11)
    c: Equal(g14,g12)
    c: Coincident(g14,g8)
    c: Coincident(g14,g10)
    c: Horizontal(g1,g-6)
FEATURE [Sketcher::SketchObject] Sketch122
  ArcFitTolerance = 1e-06
  AttachmentSupport = -> [Pad011]
  ExternalGeometry = -> [Binder001]
  FullyConstrained = true
  MakeInternals = false
  MapMode = 5
  Placement = pos=(0,-2,0) rot=(1,0,0;1.5708rad)
  sketch-geometry (8):
    g0: LineSegment StartX=-202.765 StartY=20.303 StartZ=0 EndX=-143.955 EndY=20.303 EndZ=0
    g1: ArcOfCircle CenterX=-184.801 CenterY=-67.3089 CenterZ=0 NormalX=0 NormalY=0 NormalZ=1 AngleXU=0 Radius=33.7833 StartAngle=2.70526 EndAngle=3.54053
    g2: LineSegment StartX=-176.685 StartY=-80.4316 StartZ=0 EndX=-215.932 EndY=-80.4316 EndZ=0
    g3: LineSegment StartX=-215.42 StartY=-53.0315 StartZ=0 EndX=-192.176 EndY=-3.18454 EndZ=0
    g4: ArcOfCircle CenterX=-207.583 CenterY=4 CenterZ=0 NormalX=0 NormalY=0 NormalZ=1 AngleXU=0 Radius=17 StartAngle=5.84685 EndAngle=7.56663
    g5: Circle CenterX=-213.443 CenterY=-76.8316 CenterZ=0 NormalX=0 NormalY=0 NormalZ=1 AngleXU=0 Radius=3
    g6: Circle CenterX=-179.305 CenterY=-76.8316 CenterZ=0 NormalX=0 NormalY=0 NormalZ=1 AngleXU=0 Radius=3
    g7: LineSegment StartX=-143.955 StartY=20.303 StartZ=0 EndX=-176.685 EndY=-80.4316 EndZ=0
  constraints (18):
    c: Coincident(g0,g-6)
    c: Coincident(g1,g-7)
    c: Coincident(g1,g-8)
    c: Coincident(g2,g1)
    c: Tangent(g3,g-5)
    c: Coincident(g4,g-6)
    c: Coincident(g4,g0)
    c: Coincident(g3,g4)
    c: Coincident(g1,g3)
    c: Diameter(g5) = 6
    c: Diameter(g6) = 6
    c: Coincident(g5,g-9)
    c: Coincident(g6,g-10)
    c: Horizontal(g0)
    c: Horizontal(g2)
    c: Coincident(g7,g0)
    c: Coincident(g7,g2)
    c: Tangent(g7,g-4)
FEATURE [Sketcher::SketchObject] Sketch123
  ArcFitTolerance = 1e-06
  AttachmentSupport = -> [Pad011]
  ExternalGeometry = -> [Binder001]
  FullyConstrained = true
  MakeInternals = false
  MapMode = 5
  Placement = pos=(0,-2,0) rot=(1,0,0;1.5708rad)
  sketch-geometry (4):
    g0: LineSegment StartX=-108 StartY=36.8 StartZ=0 EndX=-90 EndY=36.8 EndZ=0
    g1: LineSegment StartX=-108 StartY=36.8 StartZ=0 EndX=-108 EndY=26.8 EndZ=0
    g2: LineSegment StartX=-108 StartY=26.8 StartZ=0 EndX=-90 EndY=26.8 EndZ=0
    g3: ArcOfCircle CenterX=-94 CenterY=31.8 CenterZ=0 NormalX=0 NormalY=0 NormalZ=1 AngleXU=0 Radius=6.40312 StartAngle=5.38713 EndAngle=7.17924
  constraints (13):
    c: Horizontal(g0)
    c: Coincident(g1,g0)
    c: Vertical(g1)
    c: Coincident(g2,g1)
    c: Horizontal(g2)
    c: DistanceX(g0,g0) = 18
    c: DistanceY(g1,g1) = 10
    c: Equal(g0,g2)
    c: DistanceX(g0,g-3) = 90
    c: DistanceY(g0,g-3) = 2.4
    c: Coincident(g3,g0)
    c: Coincident(g3,g2)
    c: DistanceX(g3,g0) = 4
FEATURE [PartDesign::Chamfer] Chamfer014
  Angle = 45
  Base = -> Pad011 [Edge80,Edge4,Edge7]
  BaseFeature = -> Pad011
  ChamferType = 0
  FlipDirection = false
  Refine = true
  Size = 1.9
  Size2 = 1
  SupportTransform = false
  Suppressed = false
  UseAllEdges = false
FEATURE [PartDesign::Pocket] Pocket006
  BaseFeature = -> Chamfer014
  Direction = (0,-1,2e-16)
  Length = 1.2
  Length2 = 5
  Profile = -> Sketch115
  ReferenceAxis = -> Sketch115 [N_Axis]
  Refine = true
  Suppressed = false
  Type = 0
FEATURE [Sketcher::SketchObject] Sketch116  label="Sketch116 - pieno per inserto M3 x 3 x 4,5"
  ArcFitTolerance = 1e-06
  AttachmentSupport = -> [Pocket006]
  ExternalGeometry = -> [Binder001]
  FullyConstrained = true
  MakeInternals = false
  MapMode = 5
  Placement = pos=(0,1.7e-15,0) rot=(0,0.707107,0.707107;3.14159rad)
  sketch-geometry (4):
    g0: Circle CenterX=43.2 CenterY=30.3 CenterZ=0 NormalX=0 NormalY=0 NormalZ=1 AngleXU=0 Radius=3.4
    g1: Circle CenterX=43.2 CenterY=12.1 CenterZ=0 NormalX=0 NormalY=0 NormalZ=1 AngleXU=0 Radius=3.4
    g2: Circle CenterX=18.6 CenterY=30.3 CenterZ=0 NormalX=0 NormalY=0 NormalZ=1 AngleXU=0 Radius=3.4
    g3: Circle CenterX=18.6 CenterY=12.1 CenterZ=0 NormalX=0 NormalY=0 NormalZ=1 AngleXU=0 Radius=3.4
  constraints (8):
    c: Diameter(g0) = 6.8
    c: Diameter(g1) = 6.8
    c: Diameter(g2) = 6.8
    c: Diameter(g3) = 6.8
    c: Coincident(g2,g-3)
    c: Coincident(g0,g-4)
    c: Coincident(g3,g-6)
    c: Coincident(g1,g-5)
FEATURE [PartDesign::Pad] Pad012
  BaseFeature = -> Pocket006
  Direction = (0,1,-2e-16)
  Length = 2.4
  Length2 = 10
  Profile = -> Sketch116
  ReferenceAxis = -> Sketch116 [N_Axis]
  Refine = true
  Suppressed = false
  Type = 0
FEATURE [PartDesign::Pocket] Pocket007
  BaseFeature = -> Pad012
  Direction = (0,-1,2e-16)
  Length = 0.6
  Length2 = 2.4
  Profile = -> Sketch117
  ReferenceAxis = -> Sketch117 [N_Axis]
  Refine = true
  Suppressed = false
  Type = 4
FEATURE [PartDesign::Pad] Pad013
  BaseFeature = -> Pocket007
  Direction = (0,-1,2e-16)
  Length = 1.6
  Length2 = 10
  Profile = -> Sketch118
  ReferenceAxis = -> Sketch118 [N_Axis]
  Refine = true
  Suppressed = false
  Type = 0
FEATURE [Sketcher::SketchObject] Sketch119
  ArcFitTolerance = 1e-06
  AttachmentSupport = -> [Pad013]
  ExternalGeometry = -> [Binder001]
  FullyConstrained = true
  MakeInternals = false
  MapMode = 5
  Placement = pos=(0,-3.6,0) rot=(1,0,0;1.5708rad)
  sketch-geometry (21):
    g0: LineSegment [constr] StartX=-82.8 StartY=3.2 StartZ=0 EndX=-82.8 EndY=39.2 EndZ=0
    g1: ArcOfCircle CenterX=-78.51 CenterY=34.8 CenterZ=0 NormalX=0 NormalY=0 NormalZ=1 AngleXU=0 Radius=3.5 StartAngle=4.71239 EndAngle=6.28319
    g2: ArcOfCircle CenterX=-78.51 CenterY=7.6 CenterZ=0 NormalX=0 NormalY=0 NormalZ=1 AngleXU=0 Radius=3.5 StartAngle=0 EndAngle=1.5708
    g3: ArcOfCircle CenterX=-5.6 CenterY=34.8 CenterZ=0 NormalX=0 NormalY=0 NormalZ=1 AngleXU=0 Radius=3.5 StartAngle=3.14159 EndAngle=4.71239
    g4: ArcOfCircle CenterX=-5.6 CenterY=7.6 CenterZ=0 NormalX=0 NormalY=0 NormalZ=1 AngleXU=0 Radius=3.5 StartAngle=1.5708 EndAngle=3.14159
    g5: LineSegment StartX=0 StartY=39.2 StartZ=0 EndX=0 EndY=31.3 EndZ=0
    g6: LineSegment StartX=0 StartY=39.2 StartZ=0 EndX=-9.1 EndY=39.2 EndZ=0
    g7: LineSegment StartX=0 StartY=3.2 StartZ=0 EndX=0 EndY=11.1 EndZ=0
    g8: LineSegment StartX=0 StartY=3.2 StartZ=0 EndX=-9.1 EndY=3.2 EndZ=0
    g9: LineSegment StartX=-82.8 StartY=3.2 StartZ=0 EndX=-75.01 EndY=3.2 EndZ=0
    g10: LineSegment StartX=-82.8 StartY=3.2 StartZ=0 EndX=-82.8 EndY=11.1 EndZ=0
    g11: LineSegment StartX=-82.8 StartY=39.2 StartZ=0 EndX=-82.8 EndY=31.3 EndZ=0
    g12: LineSegment StartX=-82.8 StartY=39.2 StartZ=0 EndX=-75.01 EndY=39.2 EndZ=0
    g13: LineSegment StartX=-82.8 StartY=31.3 StartZ=0 EndX=-78.51 EndY=31.3 EndZ=0
    g14: LineSegment StartX=-75.01 StartY=39.2 StartZ=0 EndX=-75.01 EndY=34.8 EndZ=0
    g15: LineSegment StartX=-82.8 StartY=11.1 StartZ=0 EndX=-78.51 EndY=11.1 EndZ=0
    g16: LineSegment StartX=-75.01 StartY=3.2 StartZ=0 EndX=-75.01 EndY=7.6 EndZ=0
    g17: LineSegment StartX=-9.1 StartY=39.2 StartZ=0 EndX=-9.1 EndY=34.8 EndZ=0
    g18: LineSegment StartX=0 StartY=31.3 StartZ=0 EndX=-5.6 EndY=31.3 EndZ=0
    g19: LineSegment StartX=0 StartY=11.1 StartZ=0 EndX=-5.6 EndY=11.1 EndZ=0
    g20: LineSegment StartX=-9.1 StartY=3.2 StartZ=0 EndX=-9.1 EndY=7.6 EndZ=0
  constraints (51):
    c: Coincident(g0,g-10)
    c: PointOnObject(g0,g-8)
    c: Vertical(g0)
    c: Coincident(g1,g-3)
    c: Coincident(g2,g-4)
    c: Coincident(g3,g-5)
    c: Coincident(g4,g-6)
    c: Radius(g4) = 3.5
    c: Radius(g3) = 3.5
    c: Radius(g1) = 3.5
    c: Radius(g2) = 3.5
    c: Coincident(g5,g-9)
    c: PointOnObject(g5,g-9)
    c: Coincident(g6,g5)
    c: PointOnObject(g6,g-8)
    c: Coincident(g7,g-9)
    c: PointOnObject(g7,g-9)
    c: Coincident(g8,g7)
    c: PointOnObject(g8,g-7)
    c: Coincident(g9,g0)
    c: PointOnObject(g9,g-7)
    c: Coincident(g10,g0)
    c: PointOnObject(g10,g0)
    c: Coincident(g11,g0)
    c: PointOnObject(g11,g0)
    c: Coincident(g12,g0)
    c: PointOnObject(g12,g-8)
    c: Coincident(g13,g11)
    c: Horizontal(g13)
    c: Coincident(g14,g12)
    c: Vertical(g14)
    c: Coincident(g15,g10)
    c: Horizontal(g15)
    c: Coincident(g16,g9)
    c: Vertical(g16)
    c: Coincident(g17,g6)
    c: Vertical(g17)
    c: Coincident(g18,g5)
    c: Horizontal(g18)
    c: Coincident(g19,g7)
    c: Horizontal(g19)
    c: Coincident(g20,g8)
    c: Vertical(g20)
    c: Tangent(g20,g4) = 1.5708
    c: Tangent(g4,g19) = -1.5708
    c: Tangent(g18,g3) = 1.5708
    c: Tangent(g3,g17) = -1.5708
    c: Tangent(g13,g1) = -1.5708
    c: Tangent(g1,g14) = 1.5708
    c: Tangent(g16,g2) = -1.5708
    c: Tangent(g2,g15) = 1.5708
FEATURE [PartDesign::Pocket] Pocket008
  BaseFeature = -> Pad013
  Direction = (0,1,-2e-16)
  Length = 1.6
  Length2 = 5
  Profile = -> Sketch119
  ReferenceAxis = -> Sketch119 [N_Axis]
  Refine = true
  Suppressed = false
  Type = 0
FEATURE [PartDesign::Pad] Pad017
  BaseFeature = -> Pocket008
  Direction = (0,-1,2e-16)
  Length = 1.6
  Length2 = 10
  Profile = -> Sketch123
  ReferenceAxis = -> Sketch123 [N_Axis]
  Refine = true
  Suppressed = false
  Type = 0
FEATURE [Sketcher::SketchObject] Sketch125
  ArcFitTolerance = 1e-06
  AttachmentSupport = -> [Pad017]
  ExternalGeometry = -> [Pad017]
  FullyConstrained = true
  MakeInternals = false
  MapMode = 5
  Placement = pos=(0,-3.6,8e-16) rot=(1,0,0;1.5708rad)
  sketch-geometry (20):
    g0: LineSegment StartX=-108 StartY=35.8 StartZ=0 EndX=-108 EndY=35 EndZ=0
    g1: LineSegment StartX=-108 StartY=35 StartZ=0 EndX=-97 EndY=35 EndZ=0
    g2: LineSegment StartX=-97 StartY=35 StartZ=0 EndX=-97 EndY=35.8 EndZ=0
    g3: LineSegment StartX=-97 StartY=35.8 StartZ=0 EndX=-108 EndY=35.8 EndZ=0
    g4: LineSegment StartX=-108 StartY=28.6 StartZ=0 EndX=-108 EndY=27.8 EndZ=0
    g5: LineSegment StartX=-108 StartY=27.8 StartZ=0 EndX=-97 EndY=27.8 EndZ=0
    g6: LineSegment StartX=-97 StartY=27.8 StartZ=0 EndX=-97 EndY=28.6 EndZ=0
    g7: LineSegment StartX=-97 StartY=28.6 StartZ=0 EndX=-108 EndY=28.6 EndZ=0
    g8: LineSegment StartX=-108 StartY=30.4 StartZ=0 EndX=-108 EndY=29.6 EndZ=0
    g9: LineSegment StartX=-108 StartY=29.6 StartZ=0 EndX=-97 EndY=29.6 EndZ=0
    g10: LineSegment StartX=-97 StartY=29.6 StartZ=0 EndX=-97 EndY=30.4 EndZ=0
    g11: LineSegment StartX=-97 StartY=30.4 StartZ=0 EndX=-108 EndY=30.4 EndZ=0
    g12: LineSegment StartX=-108 StartY=32.2 StartZ=0 EndX=-108 EndY=31.4 EndZ=0
    g13: LineSegment StartX=-108 StartY=31.4 StartZ=0 EndX=-97 EndY=31.4 EndZ=0
    g14: LineSegment StartX=-97 StartY=31.4 StartZ=0 EndX=-97 EndY=32.2 EndZ=0
    g15: LineSegment StartX=-97 StartY=32.2 StartZ=0 EndX=-108 EndY=32.2 EndZ=0
    g16: LineSegment StartX=-108 StartY=34 StartZ=0 EndX=-108 EndY=33.2 EndZ=0
    g17: LineSegment StartX=-108 StartY=33.2 StartZ=0 EndX=-97 EndY=33.2 EndZ=0
    g18: LineSegment StartX=-97 StartY=33.2 StartZ=0 EndX=-97 EndY=34 EndZ=0
    g19: LineSegment StartX=-97 StartY=34 StartZ=0 EndX=-108 EndY=34 EndZ=0
  constraints (55):
    c: Coincident(g1,g0)
    c: Horizontal(g1)
    c: Coincident(g2,g1)
    c: Vertical(g2)
    c: Coincident(g3,g2)
    c: Horizontal(g3)
    c: Coincident(g3,g0)
    c: DistanceX(g1,g1) = 11
    c: DistanceY(g2,g2) = 0.8
    c: Coincident(g5,g4)
    c: Horizontal(g5)
    c: Coincident(g6,g5)
    c: Vertical(g6)
    c: Coincident(g7,g6)
    c: Horizontal(g7)
    c: Coincident(g7,g4)
    c: Coincident(g9,g8)
    c: Horizontal(g9)
    c: Coincident(g10,g9)
    c: Vertical(g10)
    c: Coincident(g11,g10)
    c: Horizontal(g11)
    c: Coincident(g11,g8)
    c: Coincident(g13,g12)
    c: Horizontal(g13)
    c: Coincident(g14,g13)
    c: Vertical(g14)
    c: Coincident(g15,g14)
    c: Horizontal(g15)
    c: Coincident(g15,g12)
    c: Coincident(g17,g16)
    c: Horizontal(g17)
    c: Coincident(g18,g17)
    c: Vertical(g18)
    c: Coincident(g19,g18)
    c: Horizontal(g19)
    c: Coincident(g19,g16)
    c: Equal(g3,g19)
    c: Equal(g3,g15)
    c: Equal(g3,g11)
    c: Equal(g3,g7)
    c: Equal(g2,g18)
    c: Equal(g2,g14)
    c: Equal(g2,g10)
    c: Equal(g2,g6)
    c: DistanceY(g-4,g4) = 1
    c: DistanceY(g4,g8) = 1
    c: DistanceY(g8,g12) = 1
    c: DistanceY(g12,g16) = 1
    c: DistanceY(g16,g0) = 1
    c: Tangent(g0,g-5)
    c: Tangent(g16,g-5)
    c: Tangent(g12,g-5)
    c: Tangent(g8,g-5)
    c: Tangent(g4,g-5)
FEATURE [PartDesign::Chamfer] Chamfer009
  Angle = 45
  Base = -> Pad017 [Edge151,Edge154]
  BaseFeature = -> Pad017
  ChamferType = 1
  FlipDirection = false
  Refine = true
  Size = 1.5
  Size2 = 2.8
  SupportTransform = false
  Suppressed = false
  UseAllEdges = false
FEATURE [PartDesign::Pocket] Pocket009
  BaseFeature = -> Chamfer009
  Direction = (0,1,-2e-16)
  Length = 1
  Length2 = 5
  Profile = -> Sketch125
  ReferenceAxis = -> Sketch125 [N_Axis]
  Refine = true
  Suppressed = false
  Type = 0
FEATURE [PartDesign::Pad] Pad014
  BaseFeature = -> Pocket009
  Direction = (0,-1,2e-16)
  Length = 0.8
  Length2 = 10
  Profile = -> Sketch120
  ReferenceAxis = -> Sketch120 [N_Axis]
  Refine = true
  Suppressed = false
  Type = 0
FEATURE [Sketcher::SketchObject] Sketch124
  ArcFitTolerance = 1e-06
  AttachmentSupport = -> [Pad014]
  ExternalGeometry = -> [Binder001]
  FullyConstrained = true
  MakeInternals = false
  MapMode = 5
  Placement = pos=(0,-2.8,6e-16) rot=(1,0,0;1.5708rad)
  sketch-geometry (4):
    g0: LineSegment StartX=-129 StartY=39.2 StartZ=0 EndX=-131.599 EndY=31.2 EndZ=0
    g1: LineSegment StartX=-118 StartY=39.2 StartZ=0 EndX=-120.599 EndY=31.2 EndZ=0
    g2: LineSegment StartX=-129 StartY=39.2 StartZ=0 EndX=-118 EndY=39.2 EndZ=0
    g3: LineSegment StartX=-120.599 StartY=31.2 StartZ=0 EndX=-131.599 EndY=31.2 EndZ=0
  constraints (12):
    c: PointOnObject(g0,g-3)
    c: PointOnObject(g1,g-3)
    c: Parallel(g-4,g0)
    c: Parallel(g-4,g1)
    c: Coincident(g2,g0)
    c: Coincident(g2,g1)
    c: DistanceX(g2,g2) = 11
    c: DistanceY(g1,g1) = 8
    c: Coincident(g3,g1)
    c: Horizontal(g3)
    c: Coincident(g3,g0)
    c: DistanceX(g1,g-3) = 118
FEATURE [PartDesign::Pad] Pad018
  BaseFeature = -> Pad014
  Direction = (0,-1,2e-16)
  Length = 1.2
  Length2 = 10
  Profile = -> Sketch124
  ReferenceAxis = -> Sketch124 [N_Axis]
  Refine = true
  Suppressed = false
  Type = 0
FEATURE [Sketcher::SketchObject] Sketch126
  ArcFitTolerance = 1e-06
  AttachmentSupport = -> [Pad018]
  ExternalGeometry = -> [Pad018]
  FullyConstrained = true
  MakeInternals = false
  MapMode = 5
  Placement = pos=(0,-4,0) rot=(1,0,0;1.5708rad)
  sketch-geometry (8):
    g0: LineSegment StartX=-129.877 StartY=36.5 StartZ=0 EndX=-130.137 EndY=35.7 EndZ=0
    g1: LineSegment StartX=-130.69 StartY=34 StartZ=0 EndX=-130.95 EndY=33.2 EndZ=0
    g2: LineSegment StartX=-129.877 StartY=36.5 StartZ=0 EndX=-118.877 EndY=36.5 EndZ=0
    g3: LineSegment StartX=-130.137 StartY=35.7 StartZ=0 EndX=-119.137 EndY=35.7 EndZ=0
    g4: LineSegment StartX=-130.69 StartY=34 StartZ=0 EndX=-119.69 EndY=34 EndZ=0
    g5: LineSegment StartX=-130.95 StartY=33.2 StartZ=0 EndX=-119.95 EndY=33.2 EndZ=0
    g6: LineSegment StartX=-118.877 StartY=36.5 StartZ=0 EndX=-119.137 EndY=35.7 EndZ=0
    g7: LineSegment StartX=-119.69 StartY=34 StartZ=0 EndX=-119.95 EndY=33.2 EndZ=0
  constraints (20):
    c: Coincident(g2,g0)
    c: Horizontal(g2)
    c: Coincident(g3,g0)
    c: Horizontal(g3)
    c: Coincident(g4,g1)
    c: Horizontal(g4)
    c: Coincident(g5,g1)
    c: Horizontal(g5)
    c: Coincident(g6,g2)
    c: Coincident(g6,g3)
    c: Coincident(g7,g4)
    c: Coincident(g7,g5)
    c: Tangent(g0,g-4)
    c: Tangent(g6,g-5)
    c: Tangent(g1,g-4)
    c: Tangent(g7,g-5)
    c: DistanceY(g3,g2) = 0.8
    c: DistanceY(g5,g4) = 0.8
    c: DistanceY(g-6,g1) = 2
    c: DistanceY(g-6,g0) = 4.5
FEATURE [PartDesign::Chamfer] Chamfer008
  Angle = 45
  Base = -> Pad018 [Edge257]
  BaseFeature = -> Pad018
  ChamferType = 1
  FlipDirection = false
  Refine = true
  Size = 1
  Size2 = 6
  SupportTransform = false
  Suppressed = false
  UseAllEdges = false
FEATURE [PartDesign::Pocket] Pocket010
  BaseFeature = -> Chamfer008
  Direction = (0,1,-2e-16)
  Length = 1
  Length2 = 5
  Profile = -> Sketch126
  ReferenceAxis = -> Sketch126 [N_Axis]
  Refine = true
  Suppressed = false
  Type = 0
FEATURE [PartDesign::Pad] Pad015
  BaseFeature = -> Pocket010
  Direction = (0,-1,2e-16)
  Length = 2
  Length2 = 10
  Profile = -> Sketch121
  ReferenceAxis = -> Sketch121 [N_Axis]
  Refine = true
  Suppressed = false
  Type = 0
FEATURE [PartDesign::Pad] Pad016
  BaseFeature = -> Pad015
  Direction = (0,-1,2e-16)
  Length = 1.6
  Length2 = 10
  Profile = -> Sketch122
  ReferenceAxis = -> Sketch122 [N_Axis]
  Refine = true
  Suppressed = false
  Type = 0
FEATURE [Sketcher::SketchObject] Sketch127
  ArcFitTolerance = 1e-06
  AttachmentSupport = -> [Pad016]
  ExternalGeometry = -> [Pad016]
  FullyConstrained = true
  MakeInternals = false
  MapMode = 5
  Placement = pos=(0,0,-80.4316) rot=(1,0,0;3.14159rad)
  sketch-geometry (8):
    g0: LineSegment StartX=-176.685 StartY=3.6 StartZ=0 EndX=-186.685 EndY=3.6 EndZ=0
    g1: LineSegment [constr] StartX=-186.685 StartY=3.6 StartZ=0 EndX=-186.685 EndY=-9e-16 EndZ=0
    g2: LineSegment StartX=-176.685 StartY=3.6 StartZ=0 EndX=-176.685 EndY=0 EndZ=0
    g3: ArcOfEllipse CenterX=-186.685 CenterY=-9e-16 CenterZ=0 NormalX=0 NormalY=0 NormalZ=1 MajorRadius=10 MinorRadius=3.6 AngleXU=1e-16 StartAngle=0 EndAngle=1.5708
    g4: LineSegment [constr] StartX=-176.685 StartY=-2e-15 StartZ=0 EndX=-196.685 EndY=-2e-15 EndZ=0
    g5: LineSegment [constr] StartX=-186.685 StartY=3.6 StartZ=0 EndX=-186.685 EndY=-3.6 EndZ=0
    g6: GeomPoint [constr] X=-177.356 Y=0 Z=0
    g7: GeomPoint [constr] X=-196.015 Y=-1.9e-15 Z=0
  constraints (13):
    c: Coincident(g0,g-4)
    c: PointOnObject(g0,g-4)
    c: DistanceX(g0,g0) = 10
    c: Coincident(g1,g0)
    c: PointOnObject(g1,g-5)
    c: Vertical(g1)
    c: Coincident(g2,g0)
    c: Coincident(g2,g-5)
    c: InternalAlignment(g4-g7 -> g3) x4
    c: Coincident(g3,g1)
    c: Coincident(g3,g0)
    c: Coincident(g3,g2)
    c: Horizontal(g4)
FEATURE [Sketcher::SketchObject] Sketch128
  ArcFitTolerance = 1e-06
  AttachmentSupport = -> [Pad016]
  ExternalGeometry = -> [Pad016]
  FullyConstrained = true
  MakeInternals = false
  MapMode = 5
  Placement = pos=(0,0,-80.4316) rot=(1,0,0;3.14159rad)
  sketch-geometry (8):
    g0: LineSegment StartX=-215.932 StartY=3.6 StartZ=0 EndX=-215.932 EndY=-1.3e-15 EndZ=0
    g1: LineSegment StartX=-215.932 StartY=3.6 StartZ=0 EndX=-205.932 EndY=3.6 EndZ=0
    g2: LineSegment [constr] StartX=-205.932 StartY=3.6 StartZ=0 EndX=-205.932 EndY=-9e-16 EndZ=0
    g3: ArcOfEllipse CenterX=-205.932 CenterY=-9e-16 CenterZ=0 NormalX=0 NormalY=0 NormalZ=1 MajorRadius=10 MinorRadius=3.6 AngleXU=-3.14159 StartAngle=4.71239 EndAngle=6.28319
    g4: LineSegment [constr] StartX=-215.932 StartY=-1e-15 StartZ=0 EndX=-195.932 EndY=-1e-15 EndZ=0
    g5: LineSegment [constr] StartX=-205.932 StartY=-3.6 StartZ=0 EndX=-205.932 EndY=3.6 EndZ=0
    g6: GeomPoint [constr] X=-215.262 Y=-2e-15 Z=0
    g7: GeomPoint [constr] X=-196.602 Y=-1e-15 Z=0
  constraints (13):
    c: Coincident(g0,g-4)
    c: Coincident(g0,g-5)
    c: Coincident(g1,g0)
    c: PointOnObject(g1,g-3)
    c: DistanceX(g1,g1) = 10
    c: Coincident(g2,g1)
    c: Vertical(g2)
    c: PointOnObject(g2,g-5)
    c: InternalAlignment(g4-g7 -> g3) x4
    c: Coincident(g3,g2)
    c: Coincident(g3,g1)
    c: Coincident(g3,g0)
    c: Horizontal(g4)
FEATURE [PartDesign::SubtractivePipe] SubtractivePipe002
  AuxilleryCurvelinear = true
  AuxillerySpineTangent = false
  BaseFeature = -> Pad016
  Binormal = (0,0,0)
  Mode = 0
  Profile = -> Sketch127
  Refine = true
  Spine = -> Pad016 [Edge254]
  SpineTangent = false
  Suppressed = false
  Transformation = 0
  Transition = 0
FEATURE [PartDesign::SubtractivePipe] SubtractivePipe003
  AuxilleryCurvelinear = true
  AuxillerySpineTangent = false
  BaseFeature = -> SubtractivePipe002
  Binormal = (0,0,0)
  Mode = 0
  Profile = -> Sketch128
  Refine = true
  Spine = -> Pad016 [Edge256,Edge251,Edge252]
  SpineTangent = false
  Suppressed = false
  Transformation = 0
  Transition = 0
FEATURE [Sketcher::SketchObject] Sketch129
  ArcFitTolerance = 1e-06
  AttachmentSupport = -> [Pad016]
  ExternalGeometry = -> [Binder001]
  FullyConstrained = true
  MakeInternals = false
  MapMode = 5
  Placement = pos=(0,-3.6,0) rot=(1,0,0;1.5708rad)
  sketch-geometry (12):
    g0: LineSegment [constr] StartX=-192.176 StartY=-3.18451 StartZ=0 EndX=-181.223 EndY=20.303 EndZ=0
    g1: LineSegment [constr] StartX=-202.765 StartY=20.303 StartZ=0 EndX=-181.223 EndY=20.303 EndZ=0
    g2: LineSegment StartX=-202.765 StartY=20.303 StartZ=0 EndX=-181.223 EndY=20.303 EndZ=0
    g3: LineSegment StartX=-192.176 StartY=-3.18451 StartZ=0 EndX=-196.804 EndY=-13.1107 EndZ=0
    g4: ArcOfCircle CenterX=-207.583 CenterY=4 CenterZ=0 NormalX=0 NormalY=0 NormalZ=1 AngleXU=0 Radius=17 StartAngle=5.84685 EndAngle=7.56663
    g5: ArcOfEllipse CenterX=-181.223 CenterY=8.55923 CenterZ=0 NormalX=0 NormalY=0 NormalZ=1 MajorRadius=23.4779 MinorRadius=11.7437 AngleXU=2e-16 StartAngle=4.71239 EndAngle=7.85398
    g6: LineSegment [constr] StartX=-157.745 StartY=8.55923 StartZ=0 EndX=-204.701 EndY=8.55923 EndZ=0
    g7: LineSegment [constr] StartX=-181.223 StartY=20.303 StartZ=0 EndX=-181.223 EndY=-3.18451 EndZ=0
    g8: GeomPoint [constr] X=-160.894 Y=8.55923 Z=0
    g9: GeomPoint [constr] X=-201.553 Y=8.55923 Z=0
    g10: ArcOfCircle CenterX=-181.223 CenterY=-20.3763 CenterZ=0 NormalX=0 NormalY=0 NormalZ=1 AngleXU=0 Radius=17.1918 StartAngle=1.57079 EndAngle=2.70526
    g11: GeomPoint [constr] X=-181.223 Y=-3.18451 Z=0
  constraints (23):
    c: Coincident(g0,g-5)
    c: Coincident(g1,g-6)
    c: Horizontal(g1)
    c: Coincident(g1,g0)
    c: Parallel(g0,g-4)
    c: Coincident(g2,g1)
    c: Coincident(g2,g0)
    c: Coincident(g3,g0)
    c: Equal(g4,g-5)
    c: Coincident(g4,g1)
    c: Coincident(g4,g0)
    c: InternalAlignment(g6-g9 -> g5) x4
    c: Vertical(g5,g0)
    c: Horizontal(g6)
    c: Coincident(g5,g0)
    c: DistanceX(g6,g-3) = 10.1
    c: Tangent(g10,g3) = -1.5708
    c: PointOnObject(g11,g10)
    c: Tangent(g5,g10,g11) = 1.5708
    c: Coincident(g10,g5)
    c: Coincident(g11,g7)
    c: Parallel(g3,g-4)
    c: Horizontal(g5,g0)
FEATURE [Sketcher::SketchObject] Sketch130
  ArcFitTolerance = 1e-06
  AttachmentOffset = pos=(0,0,-1.6) rot=(0,0,1;0rad)
  AttachmentSupport = -> [Pad016]
  ExternalGeometry = -> [Binder001]
  FullyConstrained = true
  MakeInternals = false
  MapMode = 5
  Placement = pos=(0,-2,-4e-16) rot=(1,0,0;1.5708rad)
  sketch-geometry (12):
    g0: LineSegment [constr] StartX=-192.176 StartY=-3.18451 StartZ=0 EndX=-181.223 EndY=20.303 EndZ=0
    g1: LineSegment [constr] StartX=-202.765 StartY=20.303 StartZ=0 EndX=-181.223 EndY=20.303 EndZ=0
    g2: LineSegment StartX=-202.765 StartY=20.303 StartZ=0 EndX=-181.223 EndY=20.303 EndZ=0
    g3: LineSegment StartX=-192.176 StartY=-3.18451 StartZ=0 EndX=-193.827 EndY=-6.72678 EndZ=0
    g4: ArcOfCircle CenterX=-207.583 CenterY=4 CenterZ=0 NormalX=0 NormalY=0 NormalZ=1 AngleXU=0 Radius=17 StartAngle=5.84685 EndAngle=7.56663
    g5: ArcOfEllipse CenterX=-181.223 CenterY=10.803 CenterZ=0 NormalX=0 NormalY=0 NormalZ=1 MajorRadius=14.4779 MinorRadius=9.5 AngleXU=0 StartAngle=4.71239 EndAngle=7.85398
    g6: LineSegment [constr] StartX=-166.745 StartY=10.803 StartZ=0 EndX=-195.701 EndY=10.803 EndZ=0
    g7: LineSegment [constr] StartX=-181.223 StartY=20.303 StartZ=0 EndX=-181.223 EndY=1.30297 EndZ=0
    g8: GeomPoint [constr] X=-170.298 Y=10.803 Z=0
    g9: GeomPoint [constr] X=-192.148 Y=10.803 Z=0
    g10: ArcOfCircle CenterX=-181.223 CenterY=-12.6042 CenterZ=0 NormalX=0 NormalY=0 NormalZ=1 AngleXU=0 Radius=13.9072 StartAngle=1.5708 EndAngle=2.70526
    g11: GeomPoint [constr] X=-181.223 Y=1.30297 Z=0
  constraints (23):
    c: Coincident(g0,g-5)
    c: Coincident(g1,g-6)
    c: Horizontal(g1)
    c: Coincident(g1,g0)
    c: Parallel(g0,g-4)
    c: Coincident(g2,g1)
    c: Coincident(g2,g0)
    c: Coincident(g3,g0)
    c: Equal(g4,g-5)
    c: Coincident(g4,g1)
    c: Coincident(g4,g0)
    c: InternalAlignment(g6-g9 -> g5) x4
    c: Vertical(g5,g0)
    c: Horizontal(g6)
    c: Coincident(g5,g0)
    c: DistanceX(g6,g-3) = 19.1
    c: Tangent(g10,g3) = -1.5708
    c: PointOnObject(g11,g10)
    c: Tangent(g5,g10,g11) = 1.5708
    c: Coincident(g10,g5)
    c: Coincident(g11,g7)
    c: Parallel(g3,g-4)
    c: DistanceY(g5,g0) = 19
FEATURE [Part::Part2DObjectPython] Clone2D001  label="Sketch130 (2D)"  # Draft 2D object (typed FeaturePython)
  Fuse = false
  Objects = -> [Sketch130]
  Placement = pos=(0,-2,-4e-16) rot=(1,0,0;1.5708rad)
  Scale = (1,1,1)
FEATURE [Sketcher::SketchObject] Sketch131
  ArcFitTolerance = 1e-06
  AttachmentOffset = pos=(0,0,-3.5) rot=(0,0,1;0rad)
  AttachmentSupport = -> [Pad016]
  ExternalGeometry = -> [Binder001]
  FullyConstrained = true
  MakeInternals = false
  MapMode = 5
  Placement = pos=(0,-0.1,-8e-16) rot=(1,0,0;1.5708rad)
  sketch-geometry (1):
    g0: GeomPoint X=-197.47 Y=8.55923 Z=0
  constraints (1):
    c: Symmetric(g-6,g-4,g0)
FEATURE [PartDesign::SubtractiveLoft] SubtractiveLoft002
  BaseFeature = -> SubtractivePipe003
  Closed = false
  Profile = -> Sketch129
  Refine = true
  Ruled = false
  Sections = -> [Sketch130]
  Suppressed = false
FEATURE [PartDesign::SubtractiveLoft] SubtractiveLoft003
  BaseFeature = -> SubtractiveLoft002
  Closed = false
  Profile = -> Clone2D001
  Refine = true
  Ruled = false
  Sections = -> [Sketch131]
  Suppressed = false
FEATURE [PartDesign::Chamfer] Chamfer010
  Angle = 45
  Base = -> SubtractiveLoft003 [Edge200,Edge201,Edge203,Edge202,Edge194]
  BaseFeature = -> SubtractiveLoft003
  ChamferType = 0
  FlipDirection = false
  Refine = true
  Size = 1.5
  Size2 = 1
  SupportTransform = false
  Suppressed = false
  UseAllEdges = false
FEATURE [PartDesign::Chamfer] Chamfer011
  Angle = 45
  Base = -> Chamfer010 [Edge15]
  BaseFeature = -> Chamfer010
  ChamferType = 0
  FlipDirection = false
  Refine = true
  Size = 3.5
  Size2 = 1
  SupportTransform = false
  Suppressed = false
  UseAllEdges = false
FEATURE [PartDesign::Chamfer] Chamfer012
  Angle = 45
  Base = -> Chamfer011 [Edge10]
  BaseFeature = -> Chamfer011
  ChamferType = 0
  FlipDirection = false
  Refine = true
  Size = 3.5
  Size2 = 1
  SupportTransform = false
  Suppressed = false
  UseAllEdges = false
FEATURE [PartDesign::Chamfer] Chamfer013
  Angle = 45
  Base = -> Chamfer012 [Edge146,Edge93]
  BaseFeature = -> Chamfer012
  ChamferType = 0
  FlipDirection = false
  Refine = true
  Size = 1.9
  Size2 = 1
  SupportTransform = false
  Suppressed = false
  UseAllEdges = false
FEATURE [Sketcher::SketchObject] Sketch132
  ArcFitTolerance = 1e-06
  AttachmentSupport = -> [Pad016]
  ExternalGeometry = -> [Binder001]
  FullyConstrained = true
  MakeInternals = false
  MapMode = 5
  Placement = pos=(0,-3.6,0) rot=(1,0,0;1.5708rad)
  sketch-geometry (3):
    g0: LineSegment [constr] StartX=-215.42 StartY=-53.0314 StartZ=0 EndX=-167.782 EndY=-53.0314 EndZ=0
    g1: Circle CenterX=-191.282 CenterY=-53.0314 CenterZ=0 NormalX=0 NormalY=0 NormalZ=1 AngleXU=0 Radius=11.5
    g2: Circle CenterX=-191.282 CenterY=-53.0314 CenterZ=0 NormalX=0 NormalY=0 NormalZ=1 AngleXU=0 Radius=10.7
  constraints (8):
    c: Coincident(g0,g-3)
    c: PointOnObject(g0,g-4)
    c: Horizontal(g0)
    c: Diameter(g1) = 23
    c: PointOnObject(g1,g0)
    c: DistanceX(g1,g0) = 23.5
    c: Diameter(g2) = 21.4
    c: Coincident(g2,g1)
FEATURE [PartDesign::Fillet] Fillet007
  Base = -> Chamfer013 [Edge84]
  BaseFeature = -> Chamfer013
  Radius = 1.1
  Refine = true
  SupportTransform = false
  Suppressed = false
  UseAllEdges = false
FEATURE [PartDesign::Fillet] Fillet008
  Base = -> Fillet007 [Edge77]
  BaseFeature = -> Fillet007
  Radius = 1.9
  Refine = true
  SupportTransform = false
  Suppressed = false
  UseAllEdges = false
FEATURE [PartDesign::Pocket] Pocket011
  BaseFeature = -> Fillet008
  Direction = (0,1,-2e-16)
  Length = 0.8
  Length2 = 5
  Profile = -> Sketch132
  ReferenceAxis = -> Sketch132 [N_Axis]
  Refine = true
  Suppressed = false
  Type = 0
FEATURE [Part::Part2DObjectPython] ShapeString  # Draft 2D object (typed FeaturePython)
  FontFile = <path>
  Fuse = false
  Justification = 6
  JustificationReference = 0
  KeepLeftMargin = false
  MakeFace = true
  ObliqueAngle = 0
  Placement = pos=(-199,-3.6,-57.5) rot=(1,0,0;1.5708rad)
  ScaleToSize = true
  Size = 10
  String = AS
  Tracking = 0
FEATURE [PartDesign::Pocket] Pocket012
  BaseFeature = -> Pocket011
  Direction = (0,1,0)
  Length = 1
  Length2 = 5
  Profile = -> ShapeString
  ReferenceAxis = -> ShapeString [N_Axis]
  Refine = true
  Suppressed = false
  Type = 0
FEATURE [PartDesign::Body] Body007  label="lato DX"
  AllowCompound = false
  Group = -> [Binder001,Sketch114,Pad011,Chamfer014,Sketch115,Pocket006,Sketch116,Pad012,Sketch117,Pocket007,Sketch118,Pad013,Sketch119,Pocket008,Pad017,Chamfer009,Pocket009,Sketch123,Sketch120,Pad014,Pad018,Chamfer008,Pocket010,Sketch121,Pad015,Sketch122,Pad016,Sketch124,Sketch125,Sketch126,Sketch127,Sketch128,SubtractivePipe002,SubtractivePipe003,Sketch129,Sketch130,Clone2D001,Sketch131,SubtractiveLoft002,+11 more]
  Origin = -> Origin007
  Tip = -> Pocket012
FEATURE [Sketcher::SketchObject] Sketch133
  ArcFitTolerance = 1e-06
  AttachmentSupport = -> [Binder]
  ExternalGeometry = -> [Binder]
  FullyConstrained = true
  MakeInternals = false
  MapMode = 5
  Placement = pos=(0,9e-16,0) rot=(0,0.707107,0.707107;3.14159rad)
  sketch-geometry (30):
    g0: LineSegment StartX=0 StartY=39.2 StartZ=0 EndX=0 EndY=3.2 EndZ=0
    g1: LineSegment StartX=0 StartY=3.2 StartZ=0 EndX=82.8 EndY=3.2 EndZ=0
    g2: LineSegment StartX=82.8 StartY=3.2 StartZ=0 EndX=82.8 EndY=6.2 EndZ=0
    g3: LineSegment StartX=82.8 StartY=6.2 StartZ=0 EndX=91.752 EndY=6.2 EndZ=0
    g4: LineSegment StartX=0 StartY=39.2 StartZ=0 EndX=195.887 EndY=39.2 EndZ=0
    g5: LineSegment StartX=195.887 StartY=39.2 StartZ=0 EndX=202.765 EndY=20.303 EndZ=0
    g6: LineSegment StartX=192.333 StartY=24.9893 StartZ=0 EndX=196.467 EndY=26.4942 EndZ=0
    g7: LineSegment StartX=196.467 StartY=26.4942 StartZ=0 EndX=194.073 EndY=33.0721 EndZ=0
    g8: LineSegment StartX=194.073 StartY=33.0721 StartZ=0 EndX=189.939 EndY=31.5672 EndZ=0
    g9: LineSegment StartX=189.939 StartY=31.5672 StartZ=0 EndX=192.333 EndY=24.9893 EndZ=0
    g10: ArcOfCircle CenterX=107.6 CenterY=4 CenterZ=0 NormalX=0 NormalY=0 NormalZ=1 AngleXU=0 Radius=16 StartAngle=1.5708 EndAngle=3.00366
    g11: LineSegment StartX=107.6 StartY=20 StartZ=0 EndX=132.428 EndY=20 EndZ=0
    g12: ArcOfCircle [constr] CenterX=132.428 CenterY=4 CenterZ=0 NormalX=0 NormalY=0 NormalZ=1 AngleXU=0 Radius=16 StartAngle=0.314159 EndAngle=1.5708
    g13: LineSegment StartX=147.645 StartY=8.94427 StartZ=0 EndX=176.685 EndY=-80.4316 EndZ=0
    g14: LineSegment StartX=176.685 StartY=-80.4316 StartZ=0 EndX=215.932 EndY=-80.4316 EndZ=0
    g15: ArcOfCircle CenterX=207.583 CenterY=4 CenterZ=0 NormalX=0 NormalY=0 NormalZ=1 AngleXU=0 Radius=17 StartAngle=1.85815 EndAngle=3.57792
    g16: ArcOfCircle CenterX=184.801 CenterY=-67.3089 CenterZ=0 NormalX=0 NormalY=0 NormalZ=1 AngleXU=0 Radius=33.7833 StartAngle=5.88425 EndAngle=6.71952
    g17: LineSegment StartX=192.176 StartY=-3.18451 StartZ=0 EndX=215.42 EndY=-53.0314 EndZ=0
    g18: Circle CenterX=5.6 CenterY=34.8 CenterZ=0 NormalX=0 NormalY=0 NormalZ=1 AngleXU=0 Radius=1.8
    g19: Circle CenterX=5.6 CenterY=7.6 CenterZ=0 NormalX=0 NormalY=0 NormalZ=1 AngleXU=0 Radius=1.8
    g20: Circle CenterX=78.51 CenterY=34.8 CenterZ=0 NormalX=0 NormalY=0 NormalZ=1 AngleXU=0 Radius=1.8
    g21: Circle CenterX=78.51 CenterY=7.6 CenterZ=0 NormalX=0 NormalY=0 NormalZ=1 AngleXU=0 Radius=1.8
    g22: Circle CenterX=184.08 CenterY=34.8 CenterZ=0 NormalX=0 NormalY=0 NormalZ=1 AngleXU=0 Radius=1.8
    g23: Circle CenterX=179.305 CenterY=-76.8316 CenterZ=0 NormalX=0 NormalY=0 NormalZ=1 AngleXU=0 Radius=1.8
    g24: Circle CenterX=213.443 CenterY=-76.8316 CenterZ=0 NormalX=0 NormalY=0 NormalZ=1 AngleXU=0 Radius=1.8
    g25: Circle CenterX=19 CenterY=21.2 CenterZ=0 NormalX=0 NormalY=0 NormalZ=1 AngleXU=0 Radius=6.3
    g26: Circle CenterX=42 CenterY=21.2 CenterZ=0 NormalX=0 NormalY=0 NormalZ=1 AngleXU=0 Radius=6.3
    g27: Circle CenterX=65 CenterY=21.2 CenterZ=0 NormalX=0 NormalY=0 NormalZ=1 AngleXU=0 Radius=6.3
    g28: LineSegment StartX=132.428 StartY=20 StartZ=0 EndX=144.053 EndY=20 EndZ=0
    g29: LineSegment StartX=147.645 StartY=8.94427 StartZ=0 EndX=144.053 EndY=20 EndZ=0
  constraints (65):
    c: Coincident(g0,g-4)
    c: Coincident(g0,g-5)
    c: Coincident(g1,g0)
    c: Coincident(g1,g-6)
    c: Coincident(g2,g1)
    c: Coincident(g2,g-7)
    c: Coincident(g3,g2)
    c: Coincident(g3,g-8)
    c: Coincident(g4,g0)
    c: Coincident(g4,g-16)
    c: Coincident(g5,g4)
    c: Coincident(g5,g-16)
    c: Coincident(g6,g-20)
    c: Coincident(g6,g-21)
    c: Coincident(g7,g6)
    c: Coincident(g7,g-23)
    c: Coincident(g8,g7)
    c: Coincident(g8,g-22)
    c: Coincident(g9,g8)
    c: Coincident(g9,g6)
    c: Equal(g10,g-8)
    c: Coincident(g10,g3)
    c: Coincident(g10,g-9)
    c: Coincident(g11,g10)
    c: Coincident(g11,g-10)
    c: Equal(g12,g-10)
    c: Coincident(g12,g11)
    c: Coincident(g12,g-11)
    c: Coincident(g13,g12)
    c: Coincident(g13,g-12)
    c: Coincident(g14,g13)
    c: Coincident(g14,g-13)
    c: Equal(g15,g-15)
    c: Coincident(g15,g5)
    c: Coincident(g15,g-15)
    c: Equal(g16,g-13)
    c: Coincident(g16,g14)
    c: Coincident(g16,g-14)
    c: Coincident(g17,g15)
    c: Coincident(g17,g16)
    c: Equal(g18,g-28)
    c: Equal(g19,g-29)
    c: Equal(g20,g-26)
    c: Equal(g21,g-27)
    c: Equal(g22,g-17)
    c: Equal(g24,g-25)
    c: Equal(g23,g-24)
    c: Coincident(g23,g-24)
    c: Coincident(g24,g-25)
    c: Coincident(g22,g-17)
    c: Coincident(g20,g-26)
    c: Coincident(g21,g-27)
    c: Coincident(g18,g-28)
    c: Coincident(g19,g-29)
    c: Equal(g25,g-30)
    c: Equal(g26,g-31)
    c: Equal(g27,g-32)
    c: Coincident(g25,g-30)
    c: Coincident(g26,g-31)
    c: Coincident(g27,g-32)
    c: Parallel(g28,g11)
    c: Parallel(g29,g13)
    c: Coincident(g28,g11)
    c: Coincident(g29,g12)
    c: Coincident(g29,g28)
FEATURE [PartDesign::Pad] Pad019
  Direction = (0,1,-2e-16)
  Length = 2
  Length2 = 10
  Profile = -> Sketch133
  ReferenceAxis = -> Sketch133 [N_Axis]
  Refine = true
  Suppressed = false
  Type = 0
FEATURE [Sketcher::SketchObject] Sketch091  label="Sketch091 - forma anteriore"
  ArcFitTolerance = 1e-06
  AttachmentSupport = -> [Pad019]
  ExternalGeometry = -> [Binder]
  FullyConstrained = true
  MakeInternals = false
  MapMode = 5
  Placement = pos=(0,2,0) rot=(0,0.707107,0.707107;3.14159rad)
  sketch-geometry (12):
    g0: Circle CenterX=5.6 CenterY=34.8 CenterZ=0 NormalX=0 NormalY=0 NormalZ=1 AngleXU=0 Radius=1.8
    g1: Circle CenterX=5.6 CenterY=7.6 CenterZ=0 NormalX=0 NormalY=0 NormalZ=1 AngleXU=0 Radius=1.8
    g2: Circle CenterX=78.51 CenterY=34.8 CenterZ=0 NormalX=0 NormalY=0 NormalZ=1 AngleXU=0 Radius=1.8
    g3: Circle CenterX=78.51 CenterY=7.6 CenterZ=0 NormalX=0 NormalY=0 NormalZ=1 AngleXU=0 Radius=1.8
    g4: LineSegment StartX=0 StartY=39.2 StartZ=0 EndX=0 EndY=3.2 EndZ=0
    g5: LineSegment StartX=0 StartY=3.2 StartZ=0 EndX=82.8 EndY=3.2 EndZ=0
    g6: LineSegment StartX=82.8 StartY=3.2 StartZ=0 EndX=82.8 EndY=39.2 EndZ=0
    g7: LineSegment StartX=82.8 StartY=39.2 StartZ=0 EndX=0 EndY=39.2 EndZ=0
    g8: ArcOfCircle CenterX=19 CenterY=21.2 CenterZ=0 NormalX=0 NormalY=0 NormalZ=1 AngleXU=0 Radius=10 StartAngle=1.5708 EndAngle=4.71239
    g9: ArcOfCircle CenterX=65 CenterY=21.2 CenterZ=0 NormalX=0 NormalY=0 NormalZ=1 AngleXU=0 Radius=10 StartAngle=4.71239 EndAngle=7.85398
    g10: LineSegment StartX=19 StartY=31.2 StartZ=0 EndX=65 EndY=31.2 EndZ=0
    g11: LineSegment StartX=19 StartY=11.2 StartZ=0 EndX=65 EndY=11.2 EndZ=0
  constraints (25):
    c: Equal(g2,g-7)
    c: Equal(g3,g-8)
    c: Equal(g1,g-13)
    c: Equal(g0,g-12)
    c: Coincident(g0,g-12)
    c: Coincident(g1,g-13)
    c: Coincident(g3,g-8)
    c: Coincident(g2,g-7)
    c: Coincident(g4,g-4)
    c: Coincident(g4,g-5)
    c: Coincident(g5,g4)
    c: Coincident(g5,g-6)
    c: Coincident(g6,g5)
    c: PointOnObject(g6,g-3)
    c: Vertical(g6)
    c: Coincident(g7,g6)
    c: Coincident(g7,g4)
    c: Tangent(g8,g10) = 1.5708
    c: Tangent(g8,g11) = -1.5708
    c: Tangent(g9,g10) = 1.5708
    c: Tangent(g9,g11) = -1.5708
    c: Equal(g8,g9)
    c: Radius(g8) = 10
    c: Coincident(g8,g-11)
    c: Coincident(g9,g-9)
FEATURE [Sketcher::SketchObject] Sketch093  label="Sketch093 - scavi interni pulsanti"
  ArcFitTolerance = 1e-06
  AttachmentSupport = -> [Pad019]
  ExternalGeometry = -> [Binder]
  FullyConstrained = true
  MakeInternals = false
  MapMode = 5
  Placement = pos=(0,1.8e-15,0) rot=(1,0,0;1.5708rad)
  sketch-geometry (3):
    g0: Circle CenterX=-65 CenterY=21.2 CenterZ=0 NormalX=0 NormalY=0 NormalZ=1 AngleXU=0 Radius=7.3
    g1: Circle CenterX=-42 CenterY=21.2 CenterZ=0 NormalX=0 NormalY=0 NormalZ=1 AngleXU=0 Radius=7.3
    g2: Circle CenterX=-19 CenterY=21.2 CenterZ=0 NormalX=0 NormalY=0 NormalZ=1 AngleXU=0 Radius=7.3
  constraints (6):
    c: Coincident(g0,g-3)
    c: Coincident(g1,g-4)
    c: Coincident(g2,g-5)
    c: Diameter(g0) = 14.6
    c: Diameter(g1) = 14.6
    c: Diameter(g2) = 14.6
FEATURE [Sketcher::SketchObject] Sketch094  label="Sketch094 - forma centrale"
  ArcFitTolerance = 1e-06
  AttachmentSupport = -> [Pad019]
  ExternalGeometry = -> [Binder]
  FullyConstrained = true
  MakeInternals = false
  MapMode = 5
  Placement = pos=(0,2,0) rot=(0,0.707107,0.707107;3.14159rad)
  sketch-geometry (4):
    g0: LineSegment StartX=137.815 StartY=39.2 StartZ=0 EndX=142.655 EndY=24.303 EndZ=0
    g1: LineSegment StartX=110.815 StartY=24.303 StartZ=0 EndX=142.655 EndY=24.303 EndZ=0
    g2: LineSegment StartX=137.815 StartY=39.2 StartZ=0 EndX=110.815 EndY=39.2 EndZ=0
    g3: ArcOfCircle CenterX=92.2534 CenterY=31.7515 CenterZ=0 NormalX=0 NormalY=0 NormalZ=1 AngleXU=0 Radius=20 StartAngle=5.90156 EndAngle=6.66481
  constraints (12):
    c: PointOnObject(g0,g-3)
    c: Tangent(g0,g-5)
    c: Horizontal(g1)
    c: Coincident(g1,g0)
    c: Coincident(g2,g0)
    c: PointOnObject(g2,g-3)
    c: DistanceX(g2,g2) = 27
    c: Vertical(g1,g2)
    c: Coincident(g3,g2)
    c: Radius(g3) = 20
    c: Coincident(g3,g1)
    c: DistanceY(g-6,g0) = 4
FEATURE [Sketcher::SketchObject] Sketch095  label="Sketch095 - forma posteriore"
  ArcFitTolerance = 1e-06
  AttachmentSupport = -> [Pad019]
  ExternalGeometry = -> [Binder]
  FullyConstrained = true
  MakeInternals = false
  MapMode = 5
  Placement = pos=(0,2,0) rot=(0,0.707107,0.707107;3.14159rad)
  sketch-geometry (15):
    g0: LineSegment StartX=137.815 StartY=39.2 StartZ=0 EndX=143.955 EndY=20.303 EndZ=0
    g1: LineSegment StartX=143.955 StartY=20.303 StartZ=0 EndX=190.141 EndY=20.303 EndZ=0
    g2: ArcOfCircle CenterX=184.08 CenterY=34.8 CenterZ=0 NormalX=0 NormalY=0 NormalZ=1 AngleXU=0 Radius=3.5 StartAngle=3.49066 EndAngle=4.71239
    g3: LineSegment StartX=180.791 StartY=33.6029 StartZ=0 EndX=178.754 EndY=39.2 EndZ=0
    g4: LineSegment StartX=184.08 StartY=31.3 StartZ=0 EndX=186.139 EndY=31.3 EndZ=0
    g5: LineSegment StartX=190.141 StartY=20.303 StartZ=0 EndX=186.139 EndY=31.3 EndZ=0
    g6: LineSegment StartX=137.815 StartY=39.2 StartZ=0 EndX=156.815 EndY=39.2 EndZ=0
    g7: LineSegment StartX=178.754 StartY=39.2 StartZ=0 EndX=168.815 EndY=39.2 EndZ=0
    g8: LineSegment StartX=156.815 StartY=31.2 StartZ=0 EndX=168.815 EndY=31.2 EndZ=0
    g9: ArcOfCircle CenterX=176.411 CenterY=35.2 CenterZ=0 NormalX=0 NormalY=0 NormalZ=1 AngleXU=0 Radius=20 StartAngle=2.94023 EndAngle=3.34295
    g10: ArcOfCircle CenterX=188.411 CenterY=35.2 CenterZ=0 NormalX=0 NormalY=0 NormalZ=1 AngleXU=0 Radius=20 StartAngle=2.94023 EndAngle=3.34295
    g11: LineSegment StartX=157.815 StartY=39.2 StartZ=0 EndX=167.815 EndY=39.2 EndZ=0
    g12: LineSegment StartX=157.436 StartY=36.2 StartZ=0 EndX=167.436 EndY=36.2 EndZ=0
    g13: ArcOfCircle CenterX=177.411 CenterY=35.2 CenterZ=0 NormalX=0 NormalY=0 NormalZ=1 AngleXU=0 Radius=20 StartAngle=2.94023 EndAngle=3.09157
    g14: ArcOfCircle CenterX=187.411 CenterY=35.2 CenterZ=0 NormalX=0 NormalY=0 NormalZ=1 AngleXU=0 Radius=20 StartAngle=2.94023 EndAngle=3.09157
  constraints (46):
    c: PointOnObject(g0,g-3)
    c: Tangent(g0,g-6)
    c: Coincident(g1,g0)
    c: Horizontal(g1)
    c: Radius(g2) = 3.5
    c: Coincident(g2,g-5)
    c: PointOnObject(g3,g-3)
    c: Parallel(g3,g-4)
    c: Tangent(g3,g2) = 1.5708
    c: Horizontal(g4)
    c: Tangent(g4,g2) = -1.5708
    c: Coincident(g5,g1)
    c: Parallel(g5,g-4)
    c: Coincident(g5,g4)
    c: DistanceX(g4,g-8) = 3.8
    c: Coincident(g6,g0)
    c: PointOnObject(g6,g-3)
    c: Coincident(g7,g3)
    c: PointOnObject(g7,g-3)
    c: Horizontal(g8)
    c: DistanceX(g6,g7) = 12
    c: Vertical(g8,g6)
    c: Vertical(g7,g8)
    c: DistanceY(g8,g6) = 8
    c: Coincident(g9,g8)
    c: Coincident(g9,g6)
    c: Coincident(g10,g7)
    c: Coincident(g10,g8)
    c: Radius(g9) = 20
    c: Radius(g10) = 20
    c: PointOnObject(g11,g-3)
    c: PointOnObject(g11,g-3)
    c: DistanceX(g11,g11) = 10
    c: DistanceX(g6,g11) = 1
    c: Horizontal(g12)
    c: Equal(g12,g11)
    c: DistanceY(g12,g11) = 3
    c: Coincident(g13,g11)
    c: Coincident(g13,g12)
    c: Radius(g13) = 20
    c: Coincident(g14,g11)
    c: Coincident(g14,g12)
    c: Radius(g14) = 20
    c: DistanceX(g0,g6) = 19
    c: Horizontal(g9,g13)
    c: Horizontal(g0,g-4)
FEATURE [Sketcher::SketchObject] Sketch096  label="Sketch096 - forma impugnatura"
  ArcFitTolerance = 1e-06
  AttachmentSupport = -> [Pad019]
  ExternalGeometry = -> [Binder]
  FullyConstrained = true
  MakeInternals = false
  MapMode = 5
  Placement = pos=(0,2,0) rot=(0,0.707107,0.707107;3.14159rad)
  sketch-geometry (8):
    g0: LineSegment StartX=176.685 StartY=-80.4316 StartZ=0 EndX=143.955 EndY=20.303 EndZ=0
    g1: LineSegment StartX=176.685 StartY=-80.4316 StartZ=0 EndX=215.932 EndY=-80.4316 EndZ=0
    g2: Circle CenterX=179.305 CenterY=-76.8316 CenterZ=0 NormalX=0 NormalY=0 NormalZ=1 AngleXU=0 Radius=3
    g3: Circle CenterX=213.443 CenterY=-76.8316 CenterZ=0 NormalX=0 NormalY=0 NormalZ=1 AngleXU=0 Radius=3
    g4: LineSegment StartX=143.955 StartY=20.303 StartZ=0 EndX=202.765 EndY=20.303 EndZ=0
    g5: LineSegment StartX=215.42 StartY=-53.0314 StartZ=0 EndX=192.176 EndY=-3.18451 EndZ=0
    g6: ArcOfCircle CenterX=184.801 CenterY=-67.3089 CenterZ=0 NormalX=0 NormalY=0 NormalZ=1 AngleXU=0 Radius=33.7833 StartAngle=5.88425 EndAngle=6.71952
    g7: ArcOfCircle CenterX=207.583 CenterY=4 CenterZ=0 NormalX=0 NormalY=0 NormalZ=1 AngleXU=0 Radius=17 StartAngle=1.85815 EndAngle=3.57792
  constraints (19):
    c: Coincident(g0,g-4)
    c: PointOnObject(g0,g-3)
    c: Horizontal(g0,g-7)
    c: Coincident(g1,g0)
    c: Coincident(g1,g-5)
    c: Diameter(g2) = 6
    c: Diameter(g3) = 6
    c: Coincident(g2,g-9)
    c: Coincident(g3,g-10)
    c: Coincident(g4,g0)
    c: Coincident(g5,g-6)
    c: Coincident(g6,g1)
    c: Coincident(g6,g5)
    c: Equal(g-5,g6)
    c: Coincident(g5,g-7)
    c: Coincident(g4,g-7)
    c: Tangent(g7,g-7)
    c: Coincident(g7,g4)
    c: Coincident(g7,g5)
FEATURE [Sketcher::SketchObject] Sketch097
  ArcFitTolerance = 1e-06
  AttachmentSupport = -> [Pad019]
  ExternalGeometry = -> [Binder]
  FullyConstrained = true
  MakeInternals = false
  MapMode = 5
  Placement = pos=(0,2,0) rot=(0,0.707107,0.707107;3.14159rad)
  sketch-geometry (4):
    g0: LineSegment StartX=90 StartY=36.8 StartZ=0 EndX=108 EndY=36.8 EndZ=0
    g1: LineSegment StartX=108 StartY=36.8 StartZ=0 EndX=108 EndY=26.8 EndZ=0
    g2: LineSegment StartX=108 StartY=26.8 StartZ=0 EndX=90 EndY=26.8 EndZ=0
    g3: ArcOfCircle CenterX=94 CenterY=31.8 CenterZ=0 NormalX=0 NormalY=0 NormalZ=1 AngleXU=0 Radius=6.40312 StartAngle=2.24554 EndAngle=4.03765
  constraints (13):
    c: Horizontal(g0)
    c: Coincident(g1,g0)
    c: Vertical(g1)
    c: DistanceX(g0,g0) = 18
    c: DistanceY(g1,g1) = 10
    c: Coincident(g2,g1)
    c: Horizontal(g2)
    c: Equal(g2,g0)
    c: DistanceY(g0,g-3) = 2.4
    c: Coincident(g3,g0)
    c: Coincident(g3,g2)
    c: DistanceX(g2,g3) = 4
    c: DistanceX(g-3,g0) = 90
FEATURE [PartDesign::Chamfer] Chamfer015
  Angle = 45
  Base = -> Pad019 [Edge19,Edge22,Edge79]
  BaseFeature = -> Pad019
  ChamferType = 0
  FlipDirection = false
  Refine = true
  Size = 1.9
  Size2 = 1
  SupportTransform = false
  Suppressed = false
  UseAllEdges = false
FEATURE [PartDesign::Pocket] Pocket002
  BaseFeature = -> Chamfer015
  Direction = (0,1,-2e-16)
  Length = 1.2
  Length2 = 5
  Profile = -> Sketch093
  ReferenceAxis = -> Sketch093 [N_Axis]
  Refine = true
  Suppressed = false
  Type = 0
FEATURE [PartDesign::Pad] Pad005
  BaseFeature = -> Pocket002
  Direction = (0,1,-2e-16)
  Length = 1.6
  Length2 = 10
  Profile = -> Sketch091
  ReferenceAxis = -> Sketch091 [N_Axis]
  Refine = true
  Suppressed = false
  Type = 0
FEATURE [Sketcher::SketchObject] Sketch092  label="Sketch092 - scavi per viti anteriori"
  ArcFitTolerance = 1e-06
  AttachmentSupport = -> [Pad005]
  ExternalGeometry = -> [Binder]
  FullyConstrained = true
  MakeInternals = false
  MapMode = 5
  Placement = pos=(0,3.6,0) rot=(0,0.707107,0.707107;3.14159rad)
  sketch-geometry (20):
    g0: ArcOfCircle CenterX=5.6 CenterY=7.6 CenterZ=0 NormalX=0 NormalY=0 NormalZ=1 AngleXU=0 Radius=3.5 StartAngle=0 EndAngle=1.5708
    g1: ArcOfCircle CenterX=5.6 CenterY=34.8 CenterZ=0 NormalX=0 NormalY=0 NormalZ=1 AngleXU=0 Radius=3.5 StartAngle=4.71239 EndAngle=6.28319
    g2: ArcOfCircle CenterX=78.51 CenterY=34.8 CenterZ=0 NormalX=0 NormalY=0 NormalZ=1 AngleXU=0 Radius=3.5 StartAngle=3.14159 EndAngle=4.71239
    g3: ArcOfCircle CenterX=78.51 CenterY=7.6 CenterZ=0 NormalX=0 NormalY=0 NormalZ=1 AngleXU=0 Radius=3.5 StartAngle=1.5708 EndAngle=3.14159
    g4: LineSegment StartX=0 StartY=3.2 StartZ=0 EndX=0 EndY=11.1 EndZ=0
    g5: LineSegment StartX=0 StartY=11.1 StartZ=0 EndX=5.6 EndY=11.1 EndZ=0
    g6: LineSegment StartX=0 StartY=3.2 StartZ=0 EndX=9.1 EndY=3.2 EndZ=0
    g7: LineSegment StartX=9.1 StartY=3.2 StartZ=0 EndX=9.1 EndY=7.6 EndZ=0
    g8: LineSegment StartX=0 StartY=39.2 StartZ=0 EndX=0 EndY=31.3 EndZ=0
    g9: LineSegment StartX=0 StartY=31.3 StartZ=0 EndX=5.6 EndY=31.3 EndZ=0
    g10: LineSegment StartX=0 StartY=39.2 StartZ=0 EndX=9.1 EndY=39.2 EndZ=0
    g11: LineSegment StartX=9.1 StartY=39.2 StartZ=0 EndX=9.1 EndY=34.8 EndZ=0
    g12: LineSegment StartX=82.8 StartY=39.2 StartZ=0 EndX=75.01 EndY=39.2 EndZ=0
    g13: LineSegment StartX=82.8 StartY=39.2 StartZ=0 EndX=82.8 EndY=31.3 EndZ=0
    g14: LineSegment StartX=82.8 StartY=31.3 StartZ=0 EndX=78.51 EndY=31.3 EndZ=0
    g15: LineSegment StartX=82.8 StartY=3.2 StartZ=0 EndX=75.01 EndY=3.2 EndZ=0
    g16: LineSegment StartX=75.01 StartY=3.2 StartZ=0 EndX=75.01 EndY=7.6 EndZ=0
    g17: LineSegment StartX=82.8 StartY=3.2 StartZ=0 EndX=82.8 EndY=11.1 EndZ=0
    g18: LineSegment StartX=82.8 StartY=11.1 StartZ=0 EndX=78.51 EndY=11.1 EndZ=0
    g19: LineSegment StartX=75.01 StartY=39.2 StartZ=0 EndX=75.01 EndY=34.8 EndZ=0
  constraints (48):
    c: Radius(g0) = 3.5
    c: Coincident(g0,g-10)
    c: Radius(g1) = 3.5
    c: Coincident(g1,g-9)
    c: Radius(g2) = 3.5
    c: Coincident(g2,g-8)
    c: Radius(g3) = 3.5
    c: Coincident(g3,g-7)
    c: Coincident(g4,g-5)
    c: PointOnObject(g4,g-4)
    c: Coincident(g5,g4)
    c: Horizontal(g5)
    c: Coincident(g6,g4)
    c: PointOnObject(g6,g-5)
    c: Coincident(g7,g6)
    c: Vertical(g7)
    c: Coincident(g8,g-4)
    c: PointOnObject(g8,g-4)
    c: Coincident(g9,g8)
    c: Horizontal(g9)
    c: Coincident(g10,g8)
    c: PointOnObject(g10,g-3)
    c: Coincident(g11,g10)
    c: Vertical(g11)
    c: PointOnObject(g12,g-3)
    c: PointOnObject(g12,g-3)
    c: Coincident(g13,g12)
    c: Vertical(g13)
    c: Coincident(g14,g13)
    c: Horizontal(g14)
    c: Coincident(g15,g-6)
    c: PointOnObject(g15,g-5)
    c: Coincident(g16,g15)
    c: Vertical(g16)
    c: Coincident(g17,g15)
    c: Coincident(g18,g17)
    c: Horizontal(g18)
    c: Tangent(g3,g18) = -1.5708
    c: Tangent(g16,g3) = 1.5708
    c: Coincident(g19,g12)
    c: Vertical(g19)
    c: Tangent(g2,g19) = -1.5708
    c: Tangent(g2,g14) = 1.5708
    c: Tangent(g0,g7) = -1.5708
    c: Tangent(g0,g5) = 1.5708
    c: Tangent(g9,g1) = -1.5708
    c: Tangent(g1,g11) = 1.5708
    c: Tangent(g17,g13)
FEATURE [PartDesign::Pocket] Pocket001
  BaseFeature = -> Pad005
  Direction = (0,-1,2e-16)
  Length = 1.6
  Length2 = 5
  Profile = -> Sketch092
  ReferenceAxis = -> Sketch092 [N_Axis]
  Refine = true
  Suppressed = false
  Type = 0
FEATURE [PartDesign::Pad] Pad006
  BaseFeature = -> Pocket001
  Direction = (0,1,-2e-16)
  Length = 0.8
  Length2 = 10
  Profile = -> Sketch094
  ReferenceAxis = -> Sketch094 [N_Axis]
  Refine = true
  Suppressed = false
  Type = 0
FEATURE [PartDesign::Pad] Pad007
  BaseFeature = -> Pad006
  Direction = (0,1,-2e-16)
  Length = 2
  Length2 = 10
  Profile = -> Sketch095
  ReferenceAxis = -> Sketch095 [N_Axis]
  Refine = true
  Suppressed = false
  Type = 0
FEATURE [PartDesign::Pad] Pad008  label="Pad008 - forma impugnatura"
  BaseFeature = -> Pad007
  Direction = (0,1,-2e-16)
  Length = 1.6
  Length2 = 10
  Profile = -> Sketch096
  ReferenceAxis = -> Sketch096 [N_Axis]
  Refine = true
  Suppressed = false
  Type = 0
FEATURE [PartDesign::Pad] Pad009
  BaseFeature = -> Pad008
  Direction = (0,1,-2e-16)
  Length = 1.6
  Length2 = 10
  Profile = -> Sketch097
  ReferenceAxis = -> Sketch097 [N_Axis]
  Refine = true
  Suppressed = false
  Type = 0
FEATURE [Sketcher::SketchObject] Sketch098
  ArcFitTolerance = 1e-06
  AttachmentSupport = -> [Pad006]
  ExternalGeometry = -> [Binder]
  FullyConstrained = true
  MakeInternals = false
  MapMode = 5
  Placement = pos=(0,2.8,-7e-16) rot=(0,0.707107,0.707107;3.14159rad)
  sketch-geometry (4):
    g0: LineSegment StartX=118 StartY=39.2 StartZ=0 EndX=129 EndY=39.2 EndZ=0
    g1: LineSegment StartX=120.599 StartY=31.2 StartZ=0 EndX=131.599 EndY=31.2 EndZ=0
    g2: LineSegment StartX=129 StartY=39.2 StartZ=0 EndX=131.599 EndY=31.2 EndZ=0
    g3: LineSegment StartX=118 StartY=39.2 StartZ=0 EndX=120.599 EndY=31.2 EndZ=0
  constraints (12):
    c: PointOnObject(g0,g-3)
    c: PointOnObject(g0,g-3)
    c: DistanceX(g0,g0) = 11
    c: Horizontal(g1)
    c: Equal(g1,g0)
    c: Coincident(g2,g0)
    c: Coincident(g3,g0)
    c: Parallel(g-4,g2)
    c: Coincident(g1,g2)
    c: Coincident(g1,g3)
    c: DistanceY(g1,g0) = 8
    c: DistanceX(g-3,g0) = 118
FEATURE [Sketcher::SketchObject] Sketch099
  ArcFitTolerance = 1e-06
  AttachmentSupport = -> [Pad008]
  ExternalGeometry = -> [Binder]
  FullyConstrained = true
  MakeInternals = false
  MapMode = 5
  Placement = pos=(0,3.6,0) rot=(0,0.707107,0.707107;3.14159rad)
  sketch-geometry (13):
    g0: LineSegment StartX=192.176 StartY=-3.18451 StartZ=0 EndX=196.804 EndY=-13.1108 EndZ=0
    g1: LineSegment [constr] StartX=202.765 StartY=20.303 StartZ=0 EndX=181.223 EndY=20.303 EndZ=0
    g2: LineSegment [constr] StartX=181.223 StartY=20.303 StartZ=0 EndX=181.223 EndY=-3.18451 EndZ=0
    g3: ArcOfCircle CenterX=181.223 CenterY=-20.3764 CenterZ=0 NormalX=0 NormalY=0 NormalZ=1 AngleXU=0 Radius=17.1918 StartAngle=0.436332 EndAngle=1.57079
    g4: ArcOfEllipse CenterX=181.223 CenterY=8.55923 CenterZ=0 NormalX=0 NormalY=0 NormalZ=1 MajorRadius=23.4779 MinorRadius=11.7437 AngleXU=0 StartAngle=1.5708 EndAngle=4.71239
    g5: LineSegment [constr] StartX=204.701 StartY=8.55923 StartZ=0 EndX=157.745 EndY=8.55923 EndZ=0
    g6: LineSegment [constr] StartX=181.223 StartY=20.303 StartZ=0 EndX=181.223 EndY=-3.18451 EndZ=0
    g7: GeomPoint [constr] X=201.553 Y=8.55923 Z=0
    g8: GeomPoint [constr] X=160.894 Y=8.55923 Z=0
    g9: GeomPoint [constr] X=181.223 Y=-3.18451 Z=0
    g10: LineSegment StartX=181.223 StartY=20.303 StartZ=0 EndX=202.765 EndY=20.303 EndZ=0
    g11: ArcOfCircle CenterX=207.583 CenterY=4 CenterZ=0 NormalX=0 NormalY=0 NormalZ=1 AngleXU=0 Radius=17 StartAngle=1.85815 EndAngle=3.57792
    g12: LineSegment [constr] StartX=172.411 StartY=39.2 StartZ=0 EndX=192.176 EndY=-3.18451 EndZ=0
  constraints (27):
    c: Coincident(g1,g-7)
    c: Horizontal(g1)
    c: Coincident(g2,g1)
    c: Vertical(g2)
    c: Horizontal(g2,g0)
    c: Coincident(g3,g0)
    c: Coincident(g3,g2)
    c: InternalAlignment(g5-g8 -> g4) x4
    c: Horizontal(g5)
    c: PointOnObject(g4,g2)
    c: Coincident(g4,g1)
    c: DistanceX(g-3,g5) = 10.1
    c: Coincident(g4,g2)
    c: Tangent(g3,g-5)
    c: PointOnObject(g9,g4)
    c: PointOnObject(g9,g3)
    c: Tangent(g4,g3,g9) = 1.5708
    c: Coincident(g10,g1)
    c: Coincident(g10,g1)
    c: Equal(g11,g-4)
    c: Coincident(g11,g1)
    c: Coincident(g11,g0)
    c: PointOnObject(g12,g-6)
    c: PointOnObject(g1,g12)
    c: Tangent(g12,g-5) = -1.5708
    c: Tangent(g0,g-5) = -1.5708
    c: Horizontal(g9,g12)
FEATURE [Sketcher::SketchObject] Sketch106  label="Sketch106 - smusso impuniatura interno"
  ArcFitTolerance = 1e-06
  AttachmentSupport = -> [Pad008]
  ExternalGeometry = -> [Pad008]
  FullyConstrained = true
  MakeInternals = false
  MapMode = 5
  Placement = pos=(0,-1.585e-13,-80.4316) rot=(1,0,0;3.14159rad)
  sketch-geometry (9):
    g0: LineSegment StartX=-176.685 StartY=-3.6 StartZ=0 EndX=-176.685 EndY=2.12528e-11 EndZ=0
    g1: LineSegment [constr] StartX=-176.685 StartY=1.79e-14 StartZ=0 EndX=-176.685 EndY=2.12527e-11 EndZ=0
    g2: LineSegment [constr] StartX=-186.685 StartY=-3.6 StartZ=0 EndX=-186.685 EndY=2.12528e-11 EndZ=0
    g3: ArcOfEllipse CenterX=-186.685 CenterY=2.12527e-11 CenterZ=0 NormalX=0 NormalY=0 NormalZ=1 MajorRadius=10 MinorRadius=3.6 AngleXU=-3.14159 StartAngle=1.5708 EndAngle=3.14159
    g4: LineSegment [constr] StartX=-196.685 StartY=1.79e-14 StartZ=0 EndX=-176.685 EndY=1.79e-14 EndZ=0
    g5: LineSegment [constr] StartX=-186.685 StartY=-3.6 StartZ=0 EndX=-186.685 EndY=3.6 EndZ=0
    g6: GeomPoint [constr] X=-196.015 Y=1.55e-14 Z=0
    g7: GeomPoint [constr] X=-177.356 Y=1.85e-14 Z=0
    g8: LineSegment StartX=-176.685 StartY=-3.6 StartZ=0 EndX=-186.685 EndY=-3.6 EndZ=0
  constraints (15):
    c: PointOnObject(g2,g-3)
    c: Coincident(g1,g-5)
    c: DistanceY(g1,g1) = 0
    c: Coincident(g0,g1)
    c: DistanceX(g2,g-5) = 10
    c: Vertical(g2)
    c: Horizontal(g2,g0)
    c: InternalAlignment(g4-g7 -> g3) x4
    c: Coincident(g3,g2)
    c: Horizontal(g4)
    c: Coincident(g3,g0)
    c: Tangent(g0,g-5) = 1.5708
    c: Coincident(g3,g2)
    c: Coincident(g8,g0)
    c: Coincident(g8,g2)
FEATURE [Sketcher::SketchObject] Sketch107  label="Sketch107 - smusso impugnatura esterno"
  ArcFitTolerance = 1e-06
  AttachmentSupport = -> [Pad008]
  ExternalGeometry = -> [Pad008]
  FullyConstrained = true
  MakeInternals = false
  MapMode = 5
  Placement = pos=(0,-1.585e-13,-80.4316) rot=(1,0,0;3.14159rad)
  sketch-geometry (9):
    g0: LineSegment [constr] StartX=-215.932 StartY=1.79e-14 StartZ=0 EndX=-215.932 EndY=2.09e-14 EndZ=0
    g1: LineSegment StartX=-215.932 StartY=-3.6 StartZ=0 EndX=-215.932 EndY=2.09e-14 EndZ=0
    g2: LineSegment StartX=-215.932 StartY=-3.6 StartZ=0 EndX=-205.932 EndY=-3.6 EndZ=0
    g3: LineSegment [constr] StartX=-205.932 StartY=-3.6 StartZ=0 EndX=-205.932 EndY=2.09e-14 EndZ=0
    g4: ArcOfEllipse CenterX=-205.932 CenterY=2.09e-14 CenterZ=0 NormalX=0 NormalY=0 NormalZ=1 MajorRadius=10 MinorRadius=3.6 AngleXU=3.14159 StartAngle=1e-16 EndAngle=1.5708
    g5: LineSegment [constr] StartX=-215.932 StartY=1.79e-14 StartZ=0 EndX=-195.932 EndY=1.79e-14 EndZ=0
    g6: LineSegment [constr] StartX=-205.932 StartY=-3.6 StartZ=0 EndX=-205.932 EndY=3.6 EndZ=0
    g7: GeomPoint [constr] X=-215.262 Y=2.14e-14 Z=0
    g8: GeomPoint [constr] X=-196.602 Y=1.78e-14 Z=0
  constraints (16):
    c: Coincident(g0,g-6)
    c: PointOnObject(g0,g-6)
    c: DistanceY(g0,g0) = 0
    c: Coincident(g1,g-6)
    c: Coincident(g1,g0)
    c: Tangent(g2,g-3)
    c: DistanceX(g2,g2) = 10
    c: Coincident(g3,g2)
    c: Vertical(g3)
    c: Horizontal(g3,g0)
    c: InternalAlignment(g5-g8 -> g4) x4
    c: Coincident(g4,g3)
    c: Horizontal(g5)
    c: Coincident(g4,g0)
    c: Coincident(g4,g2)
    c: PointOnObject(g2,g1)
FEATURE [Sketcher::SketchObject] Sketch108
  ArcFitTolerance = 1e-06
  AttachmentOffset = pos=(0,0,-1.6) rot=(0,0,1;0rad)
  AttachmentSupport = -> [Pad008]
  ExternalGeometry = -> [Binder]
  FullyConstrained = true
  MakeInternals = false
  MapMode = 5
  Placement = pos=(0,2,4e-16) rot=(0,0.707107,0.707107;3.14159rad)
  sketch-geometry (14):
    g0: LineSegment StartX=192.176 StartY=-3.18451 StartZ=0 EndX=193.827 EndY=-6.72678 EndZ=0
    g1: LineSegment [constr] StartX=202.765 StartY=20.303 StartZ=0 EndX=181.223 EndY=20.303 EndZ=0
    g2: LineSegment [constr] StartX=181.223 StartY=20.303 StartZ=0 EndX=181.223 EndY=1.30297 EndZ=0
    g3: ArcOfCircle CenterX=181.223 CenterY=-12.6042 CenterZ=0 NormalX=0 NormalY=0 NormalZ=1 AngleXU=0 Radius=13.9072 StartAngle=0.436332 EndAngle=1.5708
    g4: ArcOfEllipse CenterX=181.223 CenterY=10.803 CenterZ=0 NormalX=0 NormalY=0 NormalZ=1 MajorRadius=14.4779 MinorRadius=9.5 AngleXU=0 StartAngle=1.5708 EndAngle=4.71239
    g5: LineSegment [constr] StartX=195.701 StartY=10.803 StartZ=0 EndX=166.745 EndY=10.803 EndZ=0
    g6: LineSegment [constr] StartX=181.223 StartY=20.303 StartZ=0 EndX=181.223 EndY=1.30297 EndZ=0
    g7: GeomPoint [constr] X=192.148 Y=10.803 Z=0
    g8: GeomPoint [constr] X=170.298 Y=10.803 Z=0
    g9: LineSegment StartX=181.223 StartY=20.303 StartZ=0 EndX=202.765 EndY=20.303 EndZ=0
    g10: ArcOfCircle CenterX=207.583 CenterY=4 CenterZ=0 NormalX=0 NormalY=0 NormalZ=1 AngleXU=0 Radius=17 StartAngle=1.85815 EndAngle=3.57792
    g11: LineSegment [constr] StartX=172.411 StartY=39.2 StartZ=0 EndX=192.176 EndY=-3.18451 EndZ=0
    g12: GeomPoint [constr] X=181.223 Y=1.30297 Z=0
    g13: GeomPoint [constr] X=181.223 Y=1.30297 Z=0
  constraints (28):
    c: Coincident(g1,g-7)
    c: Horizontal(g1)
    c: Coincident(g2,g1)
    c: Vertical(g2)
    c: Coincident(g3,g2)
    c: InternalAlignment(g5-g8 -> g4) x4
    c: Horizontal(g5)
    c: PointOnObject(g4,g2)
    c: Coincident(g4,g1)
    c: DistanceX(g-3,g5) = 19.1
    c: Coincident(g4,g2)
    c: Coincident(g9,g1)
    c: Coincident(g9,g1)
    c: Coincident(g10,g1)
    c: Coincident(g10,g0)
    c: PointOnObject(g11,g-6)
    c: PointOnObject(g1,g11)
    c: DistanceY(g2,g1) = 19
    c: Coincident(g10,g-4)
    c: PointOnObject(g12,g4)
    c: PointOnObject(g12,g3)
    c: Tangent(g11,g-5) = -1.5708
    c: Tangent(g0,g-5) = -1.5708
    c: Tangent(g3,g0) = 1.5708
    c: PointOnObject(g13,g4)
    c: PointOnObject(g13,g3)
    c: Tangent(g4,g3,g13) = 1.5708
    c: Horizontal(g11,g0)
FEATURE [Part::Part2DObjectPython] Clone2D  label="Sketch108 (2D)"  # Draft 2D object (typed FeaturePython)
  Fuse = false
  Objects = -> [Sketch108]
  Placement = pos=(0,2,4e-16) rot=(0,0.707107,0.707107;3.14159rad)
  Scale = (1,1,1)
FEATURE [Sketcher::SketchObject] Sketch109
  ArcFitTolerance = 1e-06
  AttachmentOffset = pos=(0,0,-3.5) rot=(0,0,1;0rad)
  AttachmentSupport = -> [Pad008]
  ExternalGeometry = -> [Binder]
  FullyConstrained = true
  MakeInternals = false
  MapMode = 5
  Placement = pos=(0,0.1,8e-16) rot=(0,0.707107,0.707107;3.14159rad)
  sketch-geometry (1):
    g0: GeomPoint X=197.47 Y=8.55923 Z=0
  constraints (1):
    c: Symmetric(g-7,g-5,g0)
FEATURE [PartDesign::Chamfer] Chamfer005
  Angle = 45
  Base = -> Pad009 [Edge215,Edge212]
  BaseFeature = -> Pad009
  ChamferType = 1
  FlipDirection = false
  Refine = true
  Size = 1.5
  Size2 = 2.8
  SupportTransform = false
  Suppressed = false
  UseAllEdges = false
FEATURE [Sketcher::SketchObject] Sketch111
  ArcFitTolerance = 1e-06
  AttachmentSupport = -> [Pad009]
  ExternalGeometry = -> [Pad009]
  FullyConstrained = true
  MakeInternals = false
  MapMode = 5
  Placement = pos=(0,3.6,-8e-16) rot=(0,0.707107,0.707107;3.14159rad)
  sketch-geometry (21):
    g0: LineSegment [constr] StartX=97 StartY=36.8 StartZ=0 EndX=97 EndY=26.8 EndZ=0
    g1: LineSegment StartX=97 StartY=28.6 StartZ=0 EndX=97 EndY=27.8 EndZ=0
    g2: LineSegment StartX=97 StartY=27.8 StartZ=0 EndX=108 EndY=27.8 EndZ=0
    g3: LineSegment StartX=108 StartY=27.8 StartZ=0 EndX=108 EndY=28.6 EndZ=0
    g4: LineSegment StartX=108 StartY=28.6 StartZ=0 EndX=97 EndY=28.6 EndZ=0
    g5: LineSegment StartX=97 StartY=35.8 StartZ=0 EndX=97 EndY=35 EndZ=0
    g6: LineSegment StartX=97 StartY=35 StartZ=0 EndX=108 EndY=35 EndZ=0
    g7: LineSegment StartX=108 StartY=35 StartZ=0 EndX=108 EndY=35.8 EndZ=0
    g8: LineSegment StartX=108 StartY=35.8 StartZ=0 EndX=97 EndY=35.8 EndZ=0
    g9: LineSegment StartX=97 StartY=30.4 StartZ=0 EndX=97 EndY=29.6 EndZ=0
    g10: LineSegment StartX=97 StartY=29.6 StartZ=0 EndX=108 EndY=29.6 EndZ=0
    g11: LineSegment StartX=108 StartY=29.6 StartZ=0 EndX=108 EndY=30.4 EndZ=0
    g12: LineSegment StartX=108 StartY=30.4 StartZ=0 EndX=97 EndY=30.4 EndZ=0
    g13: LineSegment StartX=97 StartY=34 StartZ=0 EndX=97 EndY=33.2 EndZ=0
    g14: LineSegment StartX=97 StartY=33.2 StartZ=0 EndX=108 EndY=33.2 EndZ=0
    g15: LineSegment StartX=108 StartY=33.2 StartZ=0 EndX=108 EndY=34 EndZ=0
    g16: LineSegment StartX=108 StartY=34 StartZ=0 EndX=97 EndY=34 EndZ=0
    g17: LineSegment StartX=97 StartY=32.2 StartZ=0 EndX=97 EndY=31.4 EndZ=0
    g18: LineSegment StartX=97 StartY=31.4 StartZ=0 EndX=108 EndY=31.4 EndZ=0
    g19: LineSegment StartX=108 StartY=31.4 StartZ=0 EndX=108 EndY=32.2 EndZ=0
    g20: LineSegment StartX=108 StartY=32.2 StartZ=0 EndX=97 EndY=32.2 EndZ=0
  constraints (54):
    c: Vertical(g0)
    c: PointOnObject(g0,g-3)
    c: PointOnObject(g0,g-4)
    c: DistanceX(g0,g-5) = 11
    c: Coincident(g1,g2)
    c: Coincident(g2,g3)
    c: Coincident(g3,g4)
    c: Coincident(g4,g1)
    c: Horizontal(g2)
    c: Horizontal(g4)
    c: Tangent(g1,g0)
    c: Tangent(g3,g-5)
    c: DistanceY(g2,g3) = 0.8
    c: Coincident(g5,g6)
    c: Coincident(g6,g7)
    c: Coincident(g7,g8)
    c: Coincident(g8,g5)
    c: Horizontal(g6)
    c: Horizontal(g8)
    c: DistanceY(g6,g7) = 0.8
    c: Coincident(g9,g10)
    c: Coincident(g10,g11)
    c: Coincident(g11,g12)
    c: Coincident(g12,g9)
    c: Horizontal(g10)
    c: Horizontal(g12)
    c: DistanceY(g10,g11) = 0.8
    c: Tangent(g5,g0)
    c: Tangent(g7,g-5)
    c: Tangent(g9,g0)
    c: Tangent(g11,g-5)
    c: Coincident(g13,g14)
    c: Coincident(g14,g15)
    c: Coincident(g15,g16)
    c: Coincident(g16,g13)
    c: Horizontal(g14)
    c: Horizontal(g16)
    c: DistanceY(g14,g15) = 0.8
    c: Tangent(g13,g0)
    c: Tangent(g15,g-5)
    c: Coincident(g17,g18)
    c: Coincident(g18,g19)
    c: Coincident(g19,g20)
    c: Coincident(g20,g17)
    c: Horizontal(g18)
    c: Horizontal(g20)
    c: DistanceY(g18,g19) = 0.8
    c: Tangent(g17,g0)
    c: Tangent(g19,g-5)
    c: DistanceY(g1,g9) = 1
    c: DistanceY(g9,g17) = 1
    c: DistanceY(g17,g13) = 1
    c: DistanceY(g13,g5) = 1
    c: DistanceY(g0,g1) = 1
FEATURE [PartDesign::Pocket] Pocket004
  BaseFeature = -> Chamfer005
  Direction = (0,-1,2e-16)
  Length = 1
  Length2 = 5
  Profile = -> Sketch111
  ReferenceAxis = -> Sketch111 [N_Axis]
  Refine = true
  Suppressed = false
  Type = 0
FEATURE [PartDesign::Pad] Pad010
  BaseFeature = -> Pocket004
  Direction = (0,1,-2e-16)
  Length = 1.2
  Length2 = 10
  Profile = -> Sketch098
  ReferenceAxis = -> Sketch098 [N_Axis]
  Refine = true
  Suppressed = false
  Type = 0
FEATURE [PartDesign::Chamfer] Chamfer006
  Angle = 45
  Base = -> Pad010 [Edge291]
  BaseFeature = -> Pad010
  ChamferType = 1
  FlipDirection = false
  Refine = true
  Size = 1
  Size2 = 6
  SupportTransform = false
  Suppressed = false
  UseAllEdges = false
FEATURE [Sketcher::SketchObject] Sketch110
  ArcFitTolerance = 1e-06
  AttachmentSupport = -> [Pad010]
  ExternalGeometry = -> [Sketch098]
  FullyConstrained = true
  MakeInternals = false
  MapMode = 5
  Placement = pos=(0,4,-9e-16) rot=(0,0.707107,0.707107;3.14159rad)
  sketch-geometry (8):
    g0: LineSegment StartX=119.69 StartY=34 StartZ=0 EndX=130.69 EndY=34 EndZ=0
    g1: LineSegment StartX=119.95 StartY=33.2 StartZ=0 EndX=130.95 EndY=33.2 EndZ=0
    g2: LineSegment StartX=119.137 StartY=35.7 StartZ=0 EndX=130.137 EndY=35.7 EndZ=0
    g3: LineSegment StartX=118.877 StartY=36.5 StartZ=0 EndX=129.877 EndY=36.5 EndZ=0
    g4: LineSegment StartX=118.877 StartY=36.5 StartZ=0 EndX=119.137 EndY=35.7 EndZ=0
    g5: LineSegment StartX=129.877 StartY=36.5 StartZ=0 EndX=130.137 EndY=35.7 EndZ=0
    g6: LineSegment StartX=119.69 StartY=34 StartZ=0 EndX=119.95 EndY=33.2 EndZ=0
    g7: LineSegment StartX=130.69 StartY=34 StartZ=0 EndX=130.95 EndY=33.2 EndZ=0
  constraints (24):
    c: Horizontal(g0)
    c: Horizontal(g1)
    c: Horizontal(g2)
    c: Horizontal(g3)
    c: Equal(g1,g-5)
    c: Equal(g0,g-5)
    c: Equal(g2,g-5)
    c: Equal(g3,g-5)
    c: PointOnObject(g0,g-3)
    c: PointOnObject(g1,g-3)
    c: PointOnObject(g2,g-3)
    c: PointOnObject(g3,g-3)
    c: Coincident(g4,g3)
    c: Coincident(g4,g2)
    c: Coincident(g5,g3)
    c: Coincident(g5,g2)
    c: Coincident(g6,g0)
    c: Coincident(g6,g1)
    c: Coincident(g7,g0)
    c: Coincident(g7,g1)
    c: DistanceY(g1,g0) = 0.8
    c: DistanceY(g2,g3) = 0.8
    c: DistanceY(g-5,g1) = 2
    c: DistanceY(g-5,g2) = 4.5
FEATURE [PartDesign::Pocket] Pocket003
  BaseFeature = -> Chamfer006
  Direction = (0,-1,2e-16)
  Length = 1
  Length2 = 5
  Profile = -> Sketch110
  ReferenceAxis = -> Sketch110 [N_Axis]
  Refine = true
  Suppressed = false
  Type = 0
FEATURE [PartDesign::SubtractivePipe] SubtractivePipe
  AuxilleryCurvelinear = true
  AuxillerySpineTangent = false
  BaseFeature = -> Pocket003
  Binormal = (0,0,0)
  Mode = 0
  Profile = -> Sketch106
  Refine = true
  Spine = -> Pad008 [Edge215]
  SpineTangent = false
  Suppressed = false
  Transformation = 0
  Transition = 0
FEATURE [PartDesign::SubtractivePipe] SubtractivePipe001
  AuxilleryCurvelinear = true
  AuxillerySpineTangent = false
  BaseFeature = -> SubtractivePipe
  Binormal = (0,0,0)
  Mode = 0
  Profile = -> Sketch107
  Refine = true
  Spine = -> Pad008 [Edge213,Edge216,Edge210]
  SpineTangent = false
  Suppressed = false
  Transformation = 0
  Transition = 0
FEATURE [PartDesign::SubtractiveLoft] SubtractiveLoft
  BaseFeature = -> SubtractivePipe001
  Closed = false
  Profile = -> Sketch099
  Refine = true
  Ruled = false
  Sections = -> [Sketch108]
  Suppressed = false
FEATURE [PartDesign::SubtractiveLoft] SubtractiveLoft001
  BaseFeature = -> SubtractiveLoft
  Closed = false
  Profile = -> Clone2D
  Refine = true
  Ruled = false
  Sections = -> [Sketch109]
  Suppressed = false
FEATURE [Sketcher::SketchObject] Sketch112
  ArcFitTolerance = 1e-06
  AttachmentSupport = -> [Pad008]
  ExternalGeometry = -> [Binder]
  FullyConstrained = true
  MakeInternals = false
  MapMode = 5
  Placement = pos=(0,3.6,0) rot=(0,0.707107,0.707107;3.14159rad)
  sketch-geometry (4):
    g0: LineSegment [constr] StartX=167.782 StartY=-53.0314 StartZ=0 EndX=215.42 EndY=-53.0314 EndZ=0
    g1: GeomPoint [constr] X=191.282 Y=-53.0314 Z=0
    g2: Circle CenterX=191.282 CenterY=-53.0314 CenterZ=0 NormalX=0 NormalY=0 NormalZ=1 AngleXU=0 Radius=11.5
    g3: Circle CenterX=191.282 CenterY=-53.0314 CenterZ=0 NormalX=0 NormalY=0 NormalZ=1 AngleXU=0 Radius=10.7
  constraints (9):
    c: Horizontal(g0)
    c: PointOnObject(g0,g-3)
    c: Diameter(g2) = 23
    c: Coincident(g2,g1)
    c: Diameter(g3) = 21.4
    c: Coincident(g3,g1)
    c: DistanceX(g0,g1) = 23.5
    c: PointOnObject(g1,g0)
    c: Coincident(g0,g-4)
FEATURE [PartDesign::Chamfer] Chamfer016
  Angle = 45
  Base = -> SubtractiveLoft001 [Edge118,Edge117,Edge119,Edge120,Edge109]
  BaseFeature = -> SubtractiveLoft001
  ChamferType = 0
  FlipDirection = false
  Refine = true
  Size = 1.5
  Size2 = 1
  SupportTransform = false
  Suppressed = false
  UseAllEdges = false
FEATURE [PartDesign::Chamfer] Chamfer017
  Angle = 45
  Base = -> Chamfer016 [Edge15]
  BaseFeature = -> Chamfer016
  ChamferType = 0
  FlipDirection = false
  Refine = true
  Size = 3.5
  Size2 = 1
  SupportTransform = false
  Suppressed = false
  UseAllEdges = false
FEATURE [PartDesign::Chamfer] Chamfer018
  Angle = 45
  Base = -> Chamfer017 [Edge10]
  BaseFeature = -> Chamfer017
  ChamferType = 0
  FlipDirection = false
  Refine = true
  Size = 3.5
  Size2 = 1
  SupportTransform = false
  Suppressed = false
  UseAllEdges = false
FEATURE [PartDesign::Chamfer] Chamfer019
  Angle = 45
  Base = -> Chamfer018 [Edge93,Edge140]
  BaseFeature = -> Chamfer018
  ChamferType = 0
  FlipDirection = false
  Refine = true
  Size = 1.9
  Size2 = 1
  SupportTransform = false
  Suppressed = false
  UseAllEdges = false
FEATURE [PartDesign::Fillet] Fillet009
  Base = -> Chamfer019 [Edge84]
  BaseFeature = -> Chamfer019
  Radius = 1.1
  Refine = true
  SupportTransform = false
  Suppressed = false
  UseAllEdges = false
FEATURE [PartDesign::Fillet] Fillet010
  Base = -> Fillet009 [Edge78]
  BaseFeature = -> Fillet009
  Radius = 1.9
  Refine = true
  SupportTransform = false
  Suppressed = false
  UseAllEdges = false
FEATURE [PartDesign::Pocket] Pocket005
  BaseFeature = -> Fillet010
  Direction = (0,-1,2e-16)
  Length = 0.8
  Length2 = 5
  Profile = -> Sketch112
  ReferenceAxis = -> Sketch112 [N_Axis]
  Refine = true
  Suppressed = false
  Type = 0
FEATURE [Part::Part2DObjectPython] ShapeString001  # Draft 2D object (typed FeaturePython)
  FontFile = <path>
  Fuse = false
  Justification = 6
  JustificationReference = 0
  KeepLeftMargin = false
  MakeFace = true
  ObliqueAngle = 0
  Placement = pos=(-183.5,3.6,-57.5) rot=(0,0.707107,0.707107;3.14159rad)
  ScaleToSize = true
  Size = 10
  String = AS
  Tracking = 0
FEATURE [PartDesign::Pocket] Pocket013
  BaseFeature = -> Pocket005
  Direction = (-1e-16,-1,2e-16)
  Length = 1
  Length2 = 5
  Profile = -> ShapeString001
  ReferenceAxis = -> ShapeString001 [N_Axis]
  Refine = true
  Suppressed = false
  Type = 0
FEATURE [PartDesign::Body] Body006  label="lato SX"
  AllowCompound = false
  Group = -> [Binder,Pad019,Chamfer015,Pocket002,Sketch133,Sketch091,Pad005,Sketch092,Pocket001,Sketch093,Sketch094,Pad006,Sketch095,Pad007,Sketch096,Pad008,Sketch097,Pad009,Chamfer005,Pocket004,Sketch098,Pad010,Chamfer006,Pocket003,SubtractivePipe,SubtractivePipe001,Sketch099,Sketch106,Sketch107,Sketch108,Clone2D,Sketch109,SubtractiveLoft,SubtractiveLoft001,Sketch110,Sketch111,Sketch112,Chamfer016,Chamfer017,+7 more]
  Origin = -> Origin006
  Tip = -> Pocket013
FEATURE [PartDesign::Pad] Pad020
  Direction = (0,-1,2e-16)
  Length = 25.2
  Length2 = 10
  Midplane = true
  Placement = pos=(0,0,0) rot=(1,0,0;1.5708rad)
  Profile = -> Sketch021
  ReferenceAxis = -> Sketch021 [N_Axis]
  Refine = true
  Suppressed = false
  Type = 0
FEATURE [PartDesign::Body] Body001  label="perno fermo rumble e driver solenoide"
  AllowCompound = false
  Group = -> [Sketch021,Pad020]
  Origin = -> Origin001
  Tip = -> Pad020
FEATURE [PartDesign::Pad] Pad021
  Direction = (0,-1,2e-16)
  Length = 16.8
  Length2 = 10
  Midplane = true
  Placement = pos=(0,0,0) rot=(1,0,0;1.5708rad)
  Profile = -> Sketch061
  ReferenceAxis = -> Sketch061 [N_Axis]
  Refine = true
  Suppressed = false
  Type = 0
FEATURE [PartDesign::Pocket] Pocket014
  BaseFeature = -> Pad021
  Direction = (0,1,-2e-16)
  Length = 12.8
  Length2 = 5
  Midplane = true
  Placement = pos=(0,0,0) rot=(1,0,0;1.5708rad)
  Profile = -> Sketch062
  ReferenceAxis = -> Sketch062 [N_Axis]
  Refine = true
  Suppressed = false
  Type = 0
FEATURE [PartDesign::Pad] Pad022
  BaseFeature = -> Pocket014
  Direction = (0,-1,2e-16)
  Length = 7.6
  Length2 = 10
  Midplane = true
  Placement = pos=(0,0,0) rot=(1,0,0;1.5708rad)
  Profile = -> Sketch063
  ReferenceAxis = -> Sketch063 [N_Axis]
  Refine = true
  Suppressed = false
  Type = 0
FEATURE [PartDesign::Body] Body003  label="blocco switch"
  AllowCompound = false
  Group = -> [Sketch061,Sketch062,Sketch063,Pad021,Pocket014,Pad022]
  Origin = -> Origin003
  Tip = -> Pad022
FEATURE [PartDesign::Pad] Pad024
  Direction = (0,-1,2e-16)
  Length = 17
  Length2 = 10
  Midplane = true
  Placement = pos=(0,0,0) rot=(1,0,0;1.5708rad)
  Profile = -> Sketch045
  ReferenceAxis = -> Sketch045 [N_Axis]
  Refine = true
  Suppressed = false
  Type = 0
FEATURE [PartDesign::Pocket] Pocket015
  BaseFeature = -> Pad024
  Direction = (-1,0,0)
  Length = 8
  Length2 = 5
  Placement = pos=(0,0,0) rot=(1,0,0;1.5708rad)
  Profile = -> Sketch047
  ReferenceAxis = -> Sketch047 [N_Axis]
  Refine = true
  Reversed = true
  Suppressed = false
  Type = 0
FEATURE [PartDesign::Pocket] Pocket016
  BaseFeature = -> Pocket015
  Direction = (-1,0,0)
  Length = 1
  Length2 = 5
  Placement = pos=(0,0,0) rot=(1,0,0;1.5708rad)
  Profile = -> Sketch046
  ReferenceAxis = -> Sketch046 [N_Axis]
  Refine = true
  Reversed = true
  Suppressed = false
  Type = 0
FEATURE [PartDesign::Pocket] Pocket017
  BaseFeature = -> Pocket016
  Direction = (0,1,-2e-16)
  Length = 17
  Length2 = 5
  Midplane = true
  Placement = pos=(0,0,0) rot=(1,0,0;1.5708rad)
  Profile = -> Sketch048
  ReferenceAxis = -> Sketch048 [N_Axis]
  Refine = true
  Suppressed = false
  Type = 0
FEATURE [PartDesign::Pad] Pad025
  BaseFeature = -> Pocket017
  Direction = (0,-1,2e-16)
  Length = 17
  Length2 = 10
  Midplane = true
  Placement = pos=(0,0,0) rot=(1,0,0;1.5708rad)
  Profile = -> Sketch049
  ReferenceAxis = -> Sketch049 [N_Axis]
  Refine = true
  Suppressed = false
  Type = 0
FEATURE [PartDesign::Pad] Pad026
  BaseFeature = -> Pad025
  Direction = (0,-1,2e-16)
  Length = 17
  Length2 = 10
  Midplane = true
  Placement = pos=(0,0,0) rot=(1,0,0;1.5708rad)
  Profile = -> Sketch066
  ReferenceAxis = -> Sketch066 [N_Axis]
  Refine = true
  Suppressed = false
  Type = 0
FEATURE [PartDesign::Pad] Pad027
  BaseFeature = -> Pad026
  Direction = (0,-1,2e-16)
  Length = 5
  Length2 = 10
  Midplane = true
  Placement = pos=(0,0,0) rot=(1,0,0;1.5708rad)
  Profile = -> Sketch064
  ReferenceAxis = -> Sketch064 [N_Axis]
  Refine = true
  Suppressed = false
  Type = 0
FEATURE [PartDesign::Pad] Pad028
  BaseFeature = -> Pad027
  Direction = (1,0,0)
  Length = 1
  Length2 = 10
  Placement = pos=(0,0,0) rot=(1,0,0;1.5708rad)
  Profile = -> Sketch068
  ReferenceAxis = -> Sketch068 [N_Axis]
  Refine = true
  Reversed = true
  Suppressed = false
  Type = 0
FEATURE [PartDesign::Chamfer] Chamfer020
  Angle = 45
  Base = -> Pad028 [Edge73,Edge75,Edge78,Edge77]
  BaseFeature = -> Pad028
  ChamferType = 0
  FlipDirection = false
  Placement = pos=(0,0,0) rot=(1,0,0;1.5708rad)
  Refine = true
  Size = 0.5
  Size2 = 1
  SupportTransform = false
  Suppressed = false
  UseAllEdges = false
FEATURE [PartDesign::Body] Body002  label="supporto per neopixel"
  AllowCompound = false
  Group = -> [Sketch045,Sketch047,Sketch046,Sketch048,Sketch049,Sketch066,Sketch064,Sketch068,Pad024,Pocket015,Pocket016,Pocket017,Pad025,Pad026,Pad027,Pad028,Chamfer020]
  Origin = -> Origin002
  Tip = -> Chamfer020
FEATURE [Sketcher::SketchObject] Sketch134  label="perno fermo rumble002"
  ArcFitTolerance = 1e-06
  AttachmentSupport = -> [XZ_Plane008]
  FullyConstrained = true
  MakeInternals = false
  MapMode = 5
  Placement = pos=(0,0,0) rot=(1,0,0;1.5708rad)
  sketch-geometry (16):
    g0: LineSegment StartX=0 StartY=0.45 StartZ=0 EndX=0 EndY=1.55 EndZ=0
    g1: LineSegment StartX=0.45 StartY=2 StartZ=0 EndX=1.55 EndY=2 EndZ=0
    g2: LineSegment StartX=2 StartY=1.55 StartZ=0 EndX=2 EndY=0.45 EndZ=0
    g3: LineSegment StartX=1.55 StartY=0 StartZ=0 EndX=0.45 EndY=0 EndZ=0
    g4: ArcOfCircle [constr] CenterX=0.45 CenterY=1.55 CenterZ=0 NormalX=0 NormalY=0 NormalZ=1 AngleXU=0 Radius=0.45 StartAngle=1.5708 EndAngle=3.14159
    g5: GeomPoint [constr] X=0 Y=2 Z=0
    g6: LineSegment StartX=0.45 StartY=2 StartZ=0 EndX=0 EndY=1.55 EndZ=0
    g7: ArcOfCircle [constr] CenterX=1.55 CenterY=1.55 CenterZ=0 NormalX=0 NormalY=0 NormalZ=1 AngleXU=0 Radius=0.45 StartAngle=0 EndAngle=1.5708
    g8: GeomPoint [constr] X=2 Y=2 Z=0
    g9: LineSegment StartX=2 StartY=1.55 StartZ=0 EndX=1.55 EndY=2 EndZ=0
    g10: ArcOfCircle [constr] CenterX=1.55 CenterY=0.45 CenterZ=0 NormalX=0 NormalY=0 NormalZ=1 AngleXU=0 Radius=0.45 StartAngle=4.71239 EndAngle=6.28319
    g11: GeomPoint [constr] X=2 Y=0 Z=0
    g12: LineSegment StartX=1.55 StartY=0 StartZ=0 EndX=2 EndY=0.45 EndZ=0
    g13: ArcOfCircle [constr] CenterX=0.45 CenterY=0.45 CenterZ=0 NormalX=0 NormalY=0 NormalZ=1 AngleXU=0 Radius=0.45 StartAngle=3.14159 EndAngle=4.71239
    g14: GeomPoint [constr] X=0 Y=0 Z=0
    g15: LineSegment StartX=0 StartY=0.45 StartZ=0 EndX=0.45 EndY=0 EndZ=0
  constraints (35):
    c: Coincident(g14,g-1)
    c: PointOnObject(g5,g-2)
    c: Horizontal(g1)
    c: Vertical(g2)
    c: Horizontal(g3)
    c: DistanceX(g5,g8) = 2
    c: DistanceY(g11,g8) = 2
    c: PointOnObject(g5,g0)
    c: PointOnObject(g5,g1)
    c: Tangent(g0,g4) = 1.5708
    c: Tangent(g1,g4) = 1.5708
    c: Coincident(g6,g0)
    c: Coincident(g6,g1)
    c: PointOnObject(g8,g2)
    c: PointOnObject(g8,g1)
    c: Tangent(g2,g7) = 1.5708
    c: Tangent(g1,g7) = 1.5708
    c: Coincident(g9,g2)
    c: Coincident(g9,g1)
    c: PointOnObject(g11,g2)
    c: PointOnObject(g11,g3)
    c: Tangent(g2,g10) = 1.5708
    c: Tangent(g3,g10) = 1.5708
    c: Coincident(g12,g2)
    c: Coincident(g12,g3)
    c: PointOnObject(g14,g0)
    c: PointOnObject(g14,g3)
    c: Tangent(g0,g13) = 1.5708
    c: Tangent(g3,g13) = 1.5708
    c: Coincident(g15,g0)
    c: Coincident(g15,g3)
    c: Equal(g6,g9)
    c: Equal(g9,g12)
    c: Equal(g12,g15)
    c: DistanceX(g14,g3) = 0.45
FEATURE [PartDesign::Pad] Pad029
  Direction = (0,-1,2e-16)
  Length = 17
  Length2 = 10
  Midplane = true
  Placement = pos=(0,0,0) rot=(1,0,0;1.5708rad)
  Profile = -> Sketch134
  ReferenceAxis = -> Sketch134 [N_Axis]
  Refine = true
  Suppressed = false
  Type = 0
FEATURE [PartDesign::Body] Body008  label="perno fermo neopixel"
  AllowCompound = false
  Group = -> [Sketch134,Pad029]
  Origin = -> Origin008
  Tip = -> Pad029
FEATURE [Sketcher::SketchObject] Sketch135  label="perno fermo rumble003"
  ArcFitTolerance = 1e-06
  AttachmentSupport = -> [XZ_Plane009]
  FullyConstrained = true
  MakeInternals = false
  MapMode = 5
  Placement = pos=(0,0,0) rot=(1,0,0;1.5708rad)
  sketch-geometry (16):
    g0: LineSegment StartX=4.69e-14 StartY=0.8 StartZ=0 EndX=-3.04e-14 EndY=3.1 EndZ=0
    g1: LineSegment StartX=0.8 StartY=3.9 StartZ=0 EndX=3.1 EndY=3.9 EndZ=0
    g2: LineSegment StartX=3.9 StartY=3.1 StartZ=0 EndX=3.9 EndY=0.8 EndZ=0
    g3: LineSegment StartX=3.1 StartY=0 StartZ=0 EndX=0.8 EndY=0 EndZ=0
    g4: ArcOfCircle [constr] CenterX=0.8 CenterY=3.1 CenterZ=0 NormalX=0 NormalY=0 NormalZ=1 AngleXU=0 Radius=0.8 StartAngle=1.5708 EndAngle=3.14159
    g5: GeomPoint [constr] X=0 Y=3.9 Z=0
    g6: LineSegment StartX=0.8 StartY=3.9 StartZ=0 EndX=-3.04e-14 EndY=3.1 EndZ=0
    g7: ArcOfCircle [constr] CenterX=3.1 CenterY=3.1 CenterZ=0 NormalX=0 NormalY=0 NormalZ=1 AngleXU=0 Radius=0.8 StartAngle=-2.4e-14 EndAngle=1.5708
    g8: GeomPoint [constr] X=3.9 Y=3.9 Z=0
    g9: LineSegment StartX=3.9 StartY=3.1 StartZ=0 EndX=3.1 EndY=3.9 EndZ=0
    g10: ArcOfCircle [constr] CenterX=3.1 CenterY=0.8 CenterZ=0 NormalX=0 NormalY=0 NormalZ=1 AngleXU=0 Radius=0.8 StartAngle=4.71239 EndAngle=6.28319
    g11: GeomPoint [constr] X=3.9 Y=0 Z=0
    g12: LineSegment StartX=3.1 StartY=0 StartZ=0 EndX=3.9 EndY=0.8 EndZ=0
    g13: ArcOfCircle [constr] CenterX=0.8 CenterY=0.8 CenterZ=0 NormalX=0 NormalY=0 NormalZ=1 AngleXU=0 Radius=0.8 StartAngle=3.14159 EndAngle=4.71239
    g14: GeomPoint [constr] X=0 Y=0 Z=0
    g15: LineSegment StartX=4.69e-14 StartY=0.8 StartZ=0 EndX=0.8 EndY=0 EndZ=0
  constraints (35):
    c: Coincident(g14,g-1)
    c: PointOnObject(g5,g-2)
    c: Horizontal(g1)
    c: Vertical(g2)
    c: Horizontal(g3)
    c: DistanceX(g5,g8) = 3.9
    c: DistanceY(g11,g8) = 3.9
    c: PointOnObject(g5,g0)
    c: PointOnObject(g5,g1)
    c: Tangent(g0,g4) = 1.5708
    c: Tangent(g1,g4) = 1.5708
    c: Coincident(g6,g0)
    c: Coincident(g6,g1)
    c: PointOnObject(g8,g2)
    c: PointOnObject(g8,g1)
    c: Tangent(g2,g7) = 1.5708
    c: Tangent(g1,g7) = 1.5708
    c: Coincident(g9,g2)
    c: Coincident(g9,g1)
    c: PointOnObject(g11,g2)
    c: PointOnObject(g11,g3)
    c: Tangent(g2,g10) = 1.5708
    c: Tangent(g3,g10) = 1.5708
    c: Coincident(g12,g2)
    c: Coincident(g12,g3)
    c: PointOnObject(g14,g0)
    c: PointOnObject(g14,g3)
    c: Tangent(g0,g13) = 1.5708
    c: Tangent(g3,g13) = 1.5708
    c: Coincident(g15,g0)
    c: Coincident(g15,g3)
    c: Equal(g6,g9)
    c: Equal(g9,g12)
    c: Equal(g12,g15)
    c: DistanceX(g14,g3) = 0.8
FEATURE [PartDesign::Pad] Pad030
  Direction = (0,-1,2e-16)
  Length = 25.2
  Length2 = 10
  Midplane = true
  Placement = pos=(0,0,0) rot=(1,0,0;1.5708rad)
  Profile = -> Sketch135
  ReferenceAxis = -> Sketch135 [N_Axis]
  Refine = true
  Suppressed = false
  Type = 0
FEATURE [PartDesign::Body] Body009  label="perno fermo switch - caricabatterie - grilletto"
  AllowCompound = false
  Group = -> [Sketch135,Pad030]
  Origin = -> Origin009
  Tip = -> Pad030
note: 2 file-system paths scrubbed to <path> (originals preserved in the JSON sidecar)
